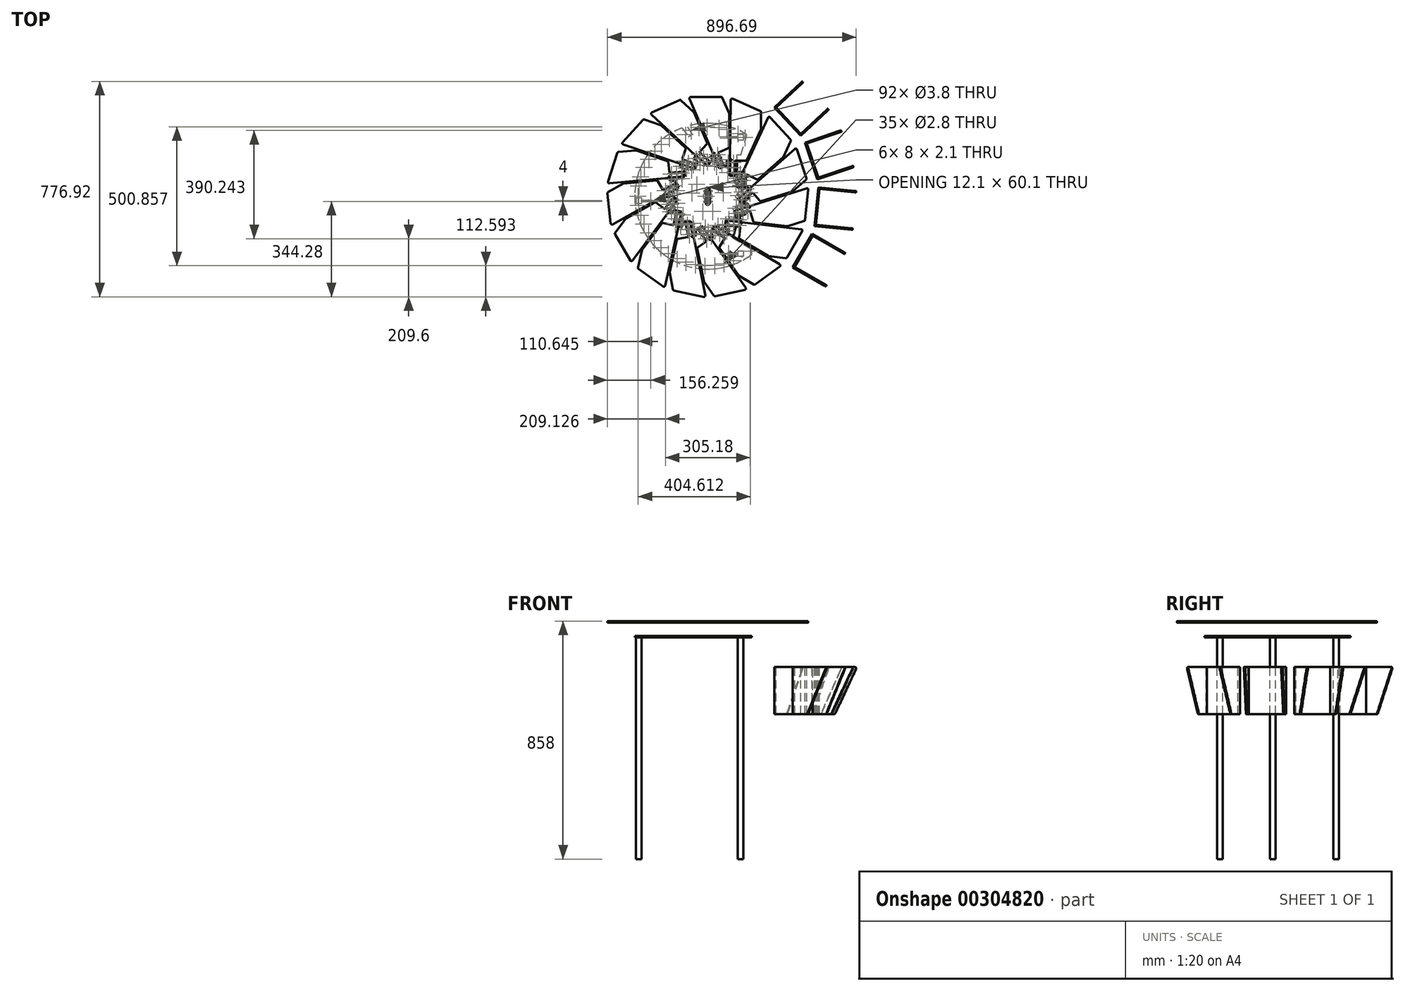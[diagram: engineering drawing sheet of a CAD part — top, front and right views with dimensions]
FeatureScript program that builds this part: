
annotation { "Feature Type Name" : "Feature", "Feature Type Description" : "" }
export const myFeature = defineFeature(function(context is Context, id is Id, definition is map)
    precondition{}
    {
        {
            var Q0;
            Q0=qCreatedBy(makeId("Top.planeOp"),FACE);
            var sketch = newSketch(context, id + "F0", { "sketchPlane" : qUnion([Q0])});
            skLineSegment(sketch, "E0", {"start": v(-97.83, 116.22) * mm, "end": v(-45.75, 98.54) * mm});
            skLineSegment(sketch, "E1", {"start": v(-80.98, 175.1) * mm, "end": v(-168.37, 255.87) * mm});
            skLineSegment(sketch, "E2", {"start": v(-101.62, 117.5) * mm, "end": v(-304.66, 186.43) * mm});
            skLineSegment(sketch, "E3", {"start": v(-306.77, 194.5) * mm, "end": v(-234.03, 275.42) * mm});
            skLineSegment(sketch, "E4", {"start": v(-43.7, 117.06) * mm, "end": v(-89.14, 132.49) * mm});
            skLineSegment(sketch, "E5", {"start": v(-91.02, 136.3) * mm, "end": v(-79.64, 169.81) * mm});
            skLineSegment(sketch, "E6.bottom", {"start": v(4.05, -30.05) * mm, "end": v(-4.05, -30.05) * mm});
            skLineSegment(sketch, "E6.top", {"start": v(4.05, 30.05) * mm, "end": v(-4.05, 30.05) * mm});
            skLineSegment(sketch, "E6.left", {"start": v(6.05, -28.05) * mm, "end": v(6.05, 28.05) * mm});
            skLineSegment(sketch, "E6.right", {"start": v(-6.05, -28.05) * mm, "end": v(-6.05, 28.05) * mm});
            skPoint(sketch, "E6.middle", {"position": v(0, 0) * mm});
            skPoint(sketch, "E7.visualSharp", {"position": v(-6.05, 30.05) * mm});
            skArc(sketch, "E7.filletArc", {"start": v(-4.05, 30.05) * mm, "mid": v(-5.46, 29.46) * mm, "end": v(-6.05, 28.05) * mm});
            skPoint(sketch, "E8.visualSharp", {"position": v(6.05, 30.05) * mm});
            skArc(sketch, "E8.filletArc", {"start": v(6.05, 28.05) * mm, "mid": v(5.46, 29.46) * mm, "end": v(4.05, 30.05) * mm});
            skPoint(sketch, "E9.visualSharp", {"position": v(-6.05, -30.05) * mm});
            skArc(sketch, "E9.filletArc", {"start": v(-6.05, -28.05) * mm, "mid": v(-5.46, -29.46) * mm, "end": v(-4.05, -30.05) * mm});
            skPoint(sketch, "E10.visualSharp", {"position": v(6.05, -30.05) * mm});
            skArc(sketch, "E10.filletArc", {"start": v(4.05, -30.05) * mm, "mid": v(5.46, -29.46) * mm, "end": v(6.05, -28.05) * mm});
            skLineSegment(sketch, "E11.bottom", {"start": v(-101.63, 105.04) * mm, "end": v(-91.98, 133.45) * mm});
            skLineSegment(sketch, "E11.top", {"start": v(-53.33, 88.65) * mm, "end": v(-43.7, 117.06) * mm});
            skLineSegment(sketch, "E11.left", {"start": v(-101.63, 105.04) * mm, "end": v(-53.33, 88.65) * mm});
            skLineSegment(sketch, "E11.right", {"start": v(-91.98, 133.45) * mm, "end": v(-43.7, 117.06) * mm});
            skCircle(sketch, "E12", {"center": v(-51.93, 114.57) * mm, "radius": 1.9 * mm});
            skCircle(sketch, "E13", {"center": v(-86.96, 126.47) * mm, "radius": 1.9 * mm});
            skCircle(sketch, "E14", {"center": v(-93.4, 107.53) * mm, "radius": 1.9 * mm});
            skCircle(sketch, "E15", {"center": v(-58.36, 95.64) * mm, "radius": 1.9 * mm});
            skPoint(sketch, "E16", {"position": v(-77.48, 96.85) * mm});
            skLineSegment(sketch, "E17.left", {"start": v(-97.51, 117.17) * mm, "end": v(-49.22, 100.77) * mm});
            skLineSegment(sketch, "E17.right", {"start": v(-96.1, 121.33) * mm, "end": v(-47.8, 104.94) * mm});
            skLineSegment(sketch, "E18.0", {"start": v(-58.36, 95.64) * mm, "end": v(-51.93, 114.57) * mm, "construction": true});
            skLineSegment(sketch, "E19.0", {"start": v(-93.4, 107.53) * mm, "end": v(-86.96, 126.47) * mm, "construction": true});
            skLineSegment(sketch, "E20.0", {"start": v(-58.36, 95.64) * mm, "end": v(-93.4, 107.53) * mm, "construction": true});
            skLineSegment(sketch, "E21.0", {"start": v(-51.93, 114.57) * mm, "end": v(-86.96, 126.47) * mm, "construction": true});
            skPoint(sketch, "E22", {"position": v(-96.8, 119.25) * mm});
            skCircle(sketch, "E23", {"center": v(-75.87, 101.58) * mm, "radius": 1.9 * mm});
            skCircle(sketch, "E24", {"center": v(-69.45, 120.52) * mm, "radius": 1.9 * mm});
            skCircle(sketch, "E25.1.0", {"center": v(-130.88, 80.16) * mm, "radius": 1.9 * mm});
            skLineSegment(sketch, "E25.1.1", {"start": v(-92.2, 63.63) * mm, "end": v(-94.04, 83.55) * mm, "construction": true});
            skCircle(sketch, "E25.1.2", {"center": v(-112.46, 81.86) * mm, "radius": 1.9 * mm});
            skLineSegment(sketch, "E25.1.3", {"start": v(-92.2, 63.63) * mm, "end": v(-129.05, 60.25) * mm, "construction": true});
            skCircle(sketch, "E25.1.4", {"center": v(-110.63, 61.94) * mm, "radius": 1.9 * mm});
            skCircle(sketch, "E25.1.5", {"center": v(-92.2, 63.63) * mm, "radius": 1.9 * mm});
            skLineSegment(sketch, "E25.1.6", {"start": v(-135.57, 54.63) * mm, "end": v(-84.78, 59.3) * mm});
            skLineSegment(sketch, "E25.1.7", {"start": v(-135.57, 54.63) * mm, "end": v(-138.31, 84.5) * mm});
            skPoint(sketch, "E25.1.8", {"position": v(-136.94, 69.56) * mm});
            skLineSegment(sketch, "E25.1.9", {"start": v(-94.04, 83.55) * mm, "end": v(-130.88, 80.16) * mm, "construction": true});
            skLineSegment(sketch, "E25.1.10", {"start": v(-84.78, 59.3) * mm, "end": v(-87.53, 89.17) * mm});
            skCircle(sketch, "E25.1.11", {"center": v(-129.05, 60.25) * mm, "radius": 1.9 * mm});
            skLineSegment(sketch, "E25.1.12", {"start": v(-129.05, 60.25) * mm, "end": v(-130.88, 80.16) * mm, "construction": true});
            skPoint(sketch, "E25.1.13", {"position": v(-110.17, 56.96) * mm});
            skCircle(sketch, "E25.1.14", {"center": v(-94.04, 83.55) * mm, "radius": 1.9 * mm});
            skLineSegment(sketch, "E25.1.16", {"start": v(-136.74, 67.37) * mm, "end": v(-85.95, 72.04) * mm});
            skLineSegment(sketch, "E25.1.17", {"start": v(-137.14, 71.75) * mm, "end": v(-86.35, 76.42) * mm});
            skCircle(sketch, "E25.2.0", {"center": v(-152.17, 20) * mm, "radius": 1.9 * mm});
            skLineSegment(sketch, "E25.2.1", {"start": v(-110.12, 20.63) * mm, "end": v(-119.9, 38.08) * mm, "construction": true});
            skCircle(sketch, "E25.2.2", {"center": v(-136.03, 29.04) * mm, "radius": 1.9 * mm});
            skLineSegment(sketch, "E25.2.3", {"start": v(-110.12, 20.63) * mm, "end": v(-142.4, 2.55) * mm, "construction": true});
            skCircle(sketch, "E25.2.4", {"center": v(-126.26, 11.59) * mm, "radius": 1.9 * mm});
            skCircle(sketch, "E25.2.5", {"center": v(-110.12, 20.63) * mm, "radius": 1.9 * mm});
            skLineSegment(sketch, "E25.2.6", {"start": v(-146.07, -5.24) * mm, "end": v(-101.57, 19.68) * mm});
            skLineSegment(sketch, "E25.2.7", {"start": v(-146.07, -5.24) * mm, "end": v(-160.72, 20.94) * mm});
            skPoint(sketch, "E25.2.8", {"position": v(-153.4, 7.85) * mm});
            skLineSegment(sketch, "E25.2.9", {"start": v(-119.9, 38.08) * mm, "end": v(-152.17, 20) * mm, "construction": true});
            skLineSegment(sketch, "E25.2.10", {"start": v(-101.57, 19.68) * mm, "end": v(-116.23, 45.86) * mm});
            skCircle(sketch, "E25.2.11", {"center": v(-142.4, 2.55) * mm, "radius": 1.9 * mm});
            skLineSegment(sketch, "E25.2.12", {"start": v(-142.4, 2.55) * mm, "end": v(-152.17, 20) * mm, "construction": true});
            skPoint(sketch, "E25.2.13", {"position": v(-123.82, 7.22) * mm});
            skCircle(sketch, "E25.2.14", {"center": v(-119.9, 38.08) * mm, "radius": 1.9 * mm});
            skLineSegment(sketch, "E25.2.16", {"start": v(-152.32, 5.93) * mm, "end": v(-107.82, 30.85) * mm});
            skLineSegment(sketch, "E25.2.17", {"start": v(-154.47, 9.77) * mm, "end": v(-109.97, 34.7) * mm});
            skCircle(sketch, "E25.3.0", {"center": v(-147.15, -43.63) * mm, "radius": 1.9 * mm});
            skLineSegment(sketch, "E25.3.1", {"start": v(-108.99, -25.95) * mm, "end": v(-125.01, -13.98) * mm, "construction": true});
            skCircle(sketch, "E25.3.2", {"center": v(-136.08, -28.8) * mm, "radius": 1.9 * mm});
            skLineSegment(sketch, "E25.3.3", {"start": v(-108.99, -25.95) * mm, "end": v(-131.13, -55.6) * mm, "construction": true});
            skCircle(sketch, "E25.3.4", {"center": v(-120.06, -40.77) * mm, "radius": 1.9 * mm});
            skCircle(sketch, "E25.3.5", {"center": v(-108.99, -25.95) * mm, "radius": 1.9 * mm});
            skLineSegment(sketch, "E25.3.6", {"start": v(-131.3, -64.2) * mm, "end": v(-100.8, -23.33) * mm});
            skLineSegment(sketch, "E25.3.7", {"start": v(-131.3, -64.2) * mm, "end": v(-155.35, -46.24) * mm});
            skPoint(sketch, "E25.3.8", {"position": v(-143.33, -55.22) * mm});
            skLineSegment(sketch, "E25.3.9", {"start": v(-125.01, -13.98) * mm, "end": v(-147.15, -43.63) * mm, "construction": true});
            skLineSegment(sketch, "E25.3.10", {"start": v(-100.8, -23.33) * mm, "end": v(-124.83, -5.38) * mm});
            skCircle(sketch, "E25.3.11", {"center": v(-131.13, -55.6) * mm, "radius": 1.9 * mm});
            skLineSegment(sketch, "E25.3.12", {"start": v(-131.13, -55.6) * mm, "end": v(-147.15, -43.63) * mm, "construction": true});
            skPoint(sketch, "E25.3.13", {"position": v(-116.05, -43.76) * mm});
            skCircle(sketch, "E25.3.14", {"center": v(-125.01, -13.98) * mm, "radius": 1.9 * mm});
            skLineSegment(sketch, "E25.3.16", {"start": v(-141.56, -56.53) * mm, "end": v(-111.05, -15.67) * mm});
            skLineSegment(sketch, "E25.3.17", {"start": v(-145.09, -53.9) * mm, "end": v(-114.57, -13.04) * mm});
            skCircle(sketch, "E25.4.0", {"center": v(-116.68, -99.7) * mm, "radius": 1.9 * mm});
            skLineSegment(sketch, "E25.4.1", {"start": v(-89.01, -68.03) * mm, "end": v(-108.52, -63.62) * mm, "construction": true});
            skCircle(sketch, "E25.4.2", {"center": v(-112.6, -81.66) * mm, "radius": 1.9 * mm});
            skLineSegment(sketch, "E25.4.3", {"start": v(-89.01, -68.03) * mm, "end": v(-97.18, -104.12) * mm, "construction": true});
            skCircle(sketch, "E25.4.4", {"center": v(-93.1, -86.08) * mm, "radius": 1.9 * mm});
            skCircle(sketch, "E25.4.5", {"center": v(-89.01, -68.03) * mm, "radius": 1.9 * mm});
            skLineSegment(sketch, "E25.4.6", {"start": v(-93.85, -112.05) * mm, "end": v(-82.6, -62.3) * mm});
            skLineSegment(sketch, "E25.4.7", {"start": v(-93.85, -112.05) * mm, "end": v(-123.1, -105.43) * mm});
            skPoint(sketch, "E25.4.8", {"position": v(-108.48, -108.74) * mm});
            skLineSegment(sketch, "E25.4.9", {"start": v(-108.52, -63.62) * mm, "end": v(-116.68, -99.7) * mm, "construction": true});
            skLineSegment(sketch, "E25.4.10", {"start": v(-82.6, -62.3) * mm, "end": v(-111.85, -55.69) * mm});
            skCircle(sketch, "E25.4.11", {"center": v(-97.18, -104.12) * mm, "radius": 1.9 * mm});
            skLineSegment(sketch, "E25.4.12", {"start": v(-97.18, -104.12) * mm, "end": v(-116.68, -99.7) * mm, "construction": true});
            skPoint(sketch, "E25.4.13", {"position": v(-88.22, -87.18) * mm});
            skCircle(sketch, "E25.4.14", {"center": v(-108.52, -63.62) * mm, "radius": 1.9 * mm});
            skLineSegment(sketch, "E25.4.16", {"start": v(-106.33, -109.23) * mm, "end": v(-95.07, -59.48) * mm});
            skLineSegment(sketch, "E25.4.17", {"start": v(-110.62, -108.26) * mm, "end": v(-99.37, -58.51) * mm});
            skCircle(sketch, "E25.5.0", {"center": v(-66.04, -138.55) * mm, "radius": 1.9 * mm});
            skLineSegment(sketch, "E25.5.1", {"start": v(-53.65, -98.36) * mm, "end": v(-73.26, -102.26) * mm, "construction": true});
            skCircle(sketch, "E25.5.2", {"center": v(-69.65, -120.4) * mm, "radius": 1.9 * mm});
            skLineSegment(sketch, "E25.5.3", {"start": v(-53.65, -98.36) * mm, "end": v(-46.43, -134.64) * mm, "construction": true});
            skCircle(sketch, "E25.5.4", {"center": v(-50.04, -116.5) * mm, "radius": 1.9 * mm});
            skCircle(sketch, "E25.5.5", {"center": v(-53.65, -98.36) * mm, "radius": 1.9 * mm});
            skLineSegment(sketch, "E25.5.6", {"start": v(-40.16, -140.53) * mm, "end": v(-50.1, -90.51) * mm});
            skLineSegment(sketch, "E25.5.7", {"start": v(-40.16, -140.53) * mm, "end": v(-69.58, -146.39) * mm});
            skPoint(sketch, "E25.5.8", {"position": v(-54.87, -143.46) * mm});
            skLineSegment(sketch, "E25.5.9", {"start": v(-73.26, -102.26) * mm, "end": v(-66.04, -138.55) * mm, "construction": true});
            skLineSegment(sketch, "E25.5.10", {"start": v(-50.1, -90.51) * mm, "end": v(-79.53, -96.37) * mm});
            skCircle(sketch, "E25.5.11", {"center": v(-46.43, -134.64) * mm, "radius": 1.9 * mm});
            skLineSegment(sketch, "E25.5.12", {"start": v(-46.43, -134.64) * mm, "end": v(-66.04, -138.55) * mm, "construction": true});
            skPoint(sketch, "E25.5.13", {"position": v(-45.13, -115.52) * mm});
            skCircle(sketch, "E25.5.14", {"center": v(-73.26, -102.26) * mm, "radius": 1.9 * mm});
            skLineSegment(sketch, "E25.5.16", {"start": v(-52.71, -143.03) * mm, "end": v(-62.66, -93.01) * mm});
            skLineSegment(sketch, "E25.5.17", {"start": v(-57.03, -143.9) * mm, "end": v(-66.98, -93.87) * mm});
            skCircle(sketch, "E25.6.0", {"center": v(-3.98, -153.43) * mm, "radius": 1.9 * mm});
            skLineSegment(sketch, "E25.6.1", {"start": v(-9, -111.67) * mm, "end": v(-25.34, -123.21) * mm, "construction": true});
            skCircle(sketch, "E25.6.2", {"center": v(-14.66, -138.32) * mm, "radius": 1.9 * mm});
            skLineSegment(sketch, "E25.6.3", {"start": v(-9, -111.67) * mm, "end": v(12.35, -141.89) * mm, "construction": true});
            skCircle(sketch, "E25.6.4", {"center": v(1.67, -126.78) * mm, "radius": 1.9 * mm});
            skCircle(sketch, "E25.6.5", {"center": v(-9, -111.67) * mm, "radius": 1.9 * mm});
            skLineSegment(sketch, "E25.6.6", {"start": v(20.48, -144.72) * mm, "end": v(-8.96, -103.07) * mm});
            skLineSegment(sketch, "E25.6.7", {"start": v(20.48, -144.72) * mm, "end": v(-4.02, -162.03) * mm});
            skPoint(sketch, "E25.6.8", {"position": v(8.23, -153.38) * mm});
            skLineSegment(sketch, "E25.6.9", {"start": v(-25.34, -123.21) * mm, "end": v(-3.98, -153.43) * mm, "construction": true});
            skLineSegment(sketch, "E25.6.10", {"start": v(-8.96, -103.07) * mm, "end": v(-33.46, -120.38) * mm});
            skCircle(sketch, "E25.6.11", {"center": v(12.35, -141.89) * mm, "radius": 1.9 * mm});
            skLineSegment(sketch, "E25.6.12", {"start": v(12.35, -141.89) * mm, "end": v(-3.98, -153.43) * mm, "construction": true});
            skPoint(sketch, "E25.6.13", {"position": v(5.76, -123.9) * mm});
            skCircle(sketch, "E25.6.14", {"center": v(-25.34, -123.21) * mm, "radius": 1.9 * mm});
            skLineSegment(sketch, "E25.6.15", {"start": v(-4.02, -162.03) * mm, "end": v(-33.46, -120.38) * mm});
            skLineSegment(sketch, "E25.6.16", {"start": v(10.02, -152.1) * mm, "end": v(-19.41, -110.46) * mm});
            skLineSegment(sketch, "E25.6.17", {"start": v(6.43, -154.65) * mm, "end": v(-23, -113) * mm});
            skCircle(sketch, "E25.7.0", {"center": v(58.77, -141.78) * mm, "radius": 1.9 * mm});
            skLineSegment(sketch, "E25.7.1", {"start": v(37.2, -105.68) * mm, "end": v(26.97, -122.87) * mm, "construction": true});
            skCircle(sketch, "E25.7.2", {"center": v(42.87, -132.33) * mm, "radius": 1.9 * mm});
            skLineSegment(sketch, "E25.7.3", {"start": v(37.2, -105.68) * mm, "end": v(69, -124.6) * mm, "construction": true});
            skCircle(sketch, "E25.7.4", {"center": v(53.1, -115.14) * mm, "radius": 1.9 * mm});
            skCircle(sketch, "E25.7.5", {"center": v(37.2, -105.68) * mm, "radius": 1.9 * mm});
            skLineSegment(sketch, "E25.7.6", {"start": v(77.57, -123.88) * mm, "end": v(33.74, -97.8) * mm});
            skLineSegment(sketch, "E25.7.7", {"start": v(77.57, -123.88) * mm, "end": v(62.23, -149.66) * mm});
            skPoint(sketch, "E25.7.8", {"position": v(69.9, -136.77) * mm});
            skLineSegment(sketch, "E25.7.9", {"start": v(26.97, -122.87) * mm, "end": v(58.77, -141.78) * mm, "construction": true});
            skLineSegment(sketch, "E25.7.10", {"start": v(33.74, -97.8) * mm, "end": v(18.4, -123.58) * mm});
            skCircle(sketch, "E25.7.11", {"center": v(69, -124.6) * mm, "radius": 1.9 * mm});
            skLineSegment(sketch, "E25.7.12", {"start": v(69, -124.6) * mm, "end": v(58.77, -141.78) * mm, "construction": true});
            skPoint(sketch, "E25.7.13", {"position": v(55.65, -110.84) * mm});
            skCircle(sketch, "E25.7.14", {"center": v(26.97, -122.87) * mm, "radius": 1.9 * mm});
            skLineSegment(sketch, "E25.7.16", {"start": v(71.02, -134.88) * mm, "end": v(27.2, -108.8) * mm});
            skLineSegment(sketch, "E25.7.17", {"start": v(68.77, -138.66) * mm, "end": v(24.94, -112.58) * mm});
            skCircle(sketch, "E25.8.0", {"center": v(111.36, -105.62) * mm, "radius": 1.9 * mm});
            skLineSegment(sketch, "E25.8.1", {"start": v(76.96, -81.41) * mm, "end": v(74.61, -101.27) * mm, "construction": true});
            skCircle(sketch, "E25.8.2", {"center": v(92.99, -103.45) * mm, "radius": 1.9 * mm});
            skLineSegment(sketch, "E25.8.3", {"start": v(76.96, -81.41) * mm, "end": v(113.7, -85.76) * mm, "construction": true});
            skCircle(sketch, "E25.8.4", {"center": v(95.34, -83.59) * mm, "radius": 1.9 * mm});
            skCircle(sketch, "E25.8.5", {"center": v(76.96, -81.41) * mm, "radius": 1.9 * mm});
            skLineSegment(sketch, "E25.8.6", {"start": v(121.25, -81.62) * mm, "end": v(70.6, -75.62) * mm});
            skLineSegment(sketch, "E25.8.7", {"start": v(121.25, -81.62) * mm, "end": v(117.72, -111.41) * mm});
            skPoint(sketch, "E25.8.8", {"position": v(119.48, -96.52) * mm});
            skLineSegment(sketch, "E25.8.9", {"start": v(74.61, -101.27) * mm, "end": v(111.36, -105.62) * mm, "construction": true});
            skLineSegment(sketch, "E25.8.10", {"start": v(70.6, -75.62) * mm, "end": v(67.07, -105.42) * mm});
            skCircle(sketch, "E25.8.11", {"center": v(113.7, -85.76) * mm, "radius": 1.9 * mm});
            skLineSegment(sketch, "E25.8.12", {"start": v(113.7, -85.76) * mm, "end": v(111.36, -105.62) * mm, "construction": true});
            skPoint(sketch, "E25.8.13", {"position": v(95.92, -78.62) * mm});
            skCircle(sketch, "E25.8.14", {"center": v(74.61, -101.27) * mm, "radius": 1.9 * mm});
            skLineSegment(sketch, "E25.8.16", {"start": v(119.74, -94.33) * mm, "end": v(69.1, -88.34) * mm});
            skLineSegment(sketch, "E25.8.17", {"start": v(119.23, -98.7) * mm, "end": v(68.58, -92.7) * mm});
            skCircle(sketch, "E25.9.0", {"center": v(144.7, -51.2) * mm, "radius": 1.9 * mm});
            skLineSegment(sketch, "E25.9.1", {"start": v(103.42, -43.07) * mm, "end": v(109.35, -62.17) * mm, "construction": true});
            skCircle(sketch, "E25.9.2", {"center": v(127.02, -56.68) * mm, "radius": 1.9 * mm});
            skLineSegment(sketch, "E25.9.3", {"start": v(103.42, -43.07) * mm, "end": v(138.76, -32.1) * mm, "construction": true});
            skCircle(sketch, "E25.9.4", {"center": v(121.1, -37.58) * mm, "radius": 1.9 * mm});
            skCircle(sketch, "E25.9.5", {"center": v(103.42, -43.07) * mm, "radius": 1.9 * mm});
            skLineSegment(sketch, "E25.9.6", {"start": v(143.96, -25.25) * mm, "end": v(95.26, -40.37) * mm});
            skLineSegment(sketch, "E25.9.7", {"start": v(143.96, -25.25) * mm, "end": v(152.86, -53.9) * mm});
            skPoint(sketch, "E25.9.8", {"position": v(148.41, -39.57) * mm});
            skLineSegment(sketch, "E25.9.9", {"start": v(109.35, -62.17) * mm, "end": v(144.7, -51.2) * mm, "construction": true});
            skLineSegment(sketch, "E25.9.10", {"start": v(95.26, -40.37) * mm, "end": v(104.15, -69.02) * mm});
            skCircle(sketch, "E25.9.11", {"center": v(138.76, -32.1) * mm, "radius": 1.9 * mm});
            skLineSegment(sketch, "E25.9.12", {"start": v(138.76, -32.1) * mm, "end": v(144.7, -51.2) * mm, "construction": true});
            skPoint(sketch, "E25.9.13", {"position": v(119.6, -32.8) * mm});
            skCircle(sketch, "E25.9.14", {"center": v(109.35, -62.17) * mm, "radius": 1.9 * mm});
            skLineSegment(sketch, "E25.9.15", {"start": v(152.86, -53.9) * mm, "end": v(104.15, -69.02) * mm});
            skLineSegment(sketch, "E25.9.16", {"start": v(147.76, -37.47) * mm, "end": v(99.05, -52.6) * mm});
            skLineSegment(sketch, "E25.9.17", {"start": v(149.06, -41.67) * mm, "end": v(100.36, -56.8) * mm});
            skCircle(sketch, "E25.10.0", {"center": v(153, 12.08) * mm, "radius": 1.9 * mm});
            skLineSegment(sketch, "E25.10.1", {"start": v(112, 2.72) * mm, "end": v(125.19, -12.32) * mm, "construction": true});
            skCircle(sketch, "E25.10.2", {"center": v(139.1, -0.12) * mm, "radius": 1.9 * mm});
            skLineSegment(sketch, "E25.10.3", {"start": v(112, 2.72) * mm, "end": v(139.82, 27.12) * mm, "construction": true});
            skCircle(sketch, "E25.10.4", {"center": v(125.9, 14.92) * mm, "radius": 1.9 * mm});
            skCircle(sketch, "E25.10.5", {"center": v(112, 2.72) * mm, "radius": 1.9 * mm});
            skLineSegment(sketch, "E25.10.6", {"start": v(141.79, 35.5) * mm, "end": v(103.44, 1.86) * mm});
            skLineSegment(sketch, "E25.10.7", {"start": v(141.79, 35.5) * mm, "end": v(161.57, 12.93) * mm});
            skLineSegment(sketch, "E25.10.9", {"start": v(125.19, -12.32) * mm, "end": v(153, 12.08) * mm, "construction": true});
            skLineSegment(sketch, "E25.10.10", {"start": v(103.44, 1.86) * mm, "end": v(123.22, -20.7) * mm});
            skCircle(sketch, "E25.10.11", {"center": v(139.82, 27.12) * mm, "radius": 1.9 * mm});
            skLineSegment(sketch, "E25.10.12", {"start": v(139.82, 27.12) * mm, "end": v(153, 12.08) * mm, "construction": true});
            skPoint(sketch, "E25.10.13", {"position": v(122.61, 18.68) * mm});
            skCircle(sketch, "E25.10.14", {"center": v(125.19, -12.32) * mm, "radius": 1.9 * mm});
            skLineSegment(sketch, "E25.10.16", {"start": v(150.22, 25.87) * mm, "end": v(111.88, -7.76) * mm});
            skLineSegment(sketch, "E25.10.17", {"start": v(153.13, 22.56) * mm, "end": v(114.78, -11.07) * mm});
            skCircle(sketch, "E25.11.0", {"center": v(134.86, 73.27) * mm, "radius": 1.9 * mm});
            skLineSegment(sketch, "E25.11.1", {"start": v(101.21, 48.04) * mm, "end": v(119.37, 39.67) * mm, "construction": true});
            skCircle(sketch, "E25.11.2", {"center": v(127.12, 56.47) * mm, "radius": 1.9 * mm});
            skLineSegment(sketch, "E25.11.3", {"start": v(101.21, 48.04) * mm, "end": v(116.7, 81.64) * mm, "construction": true});
            skCircle(sketch, "E25.11.4", {"center": v(108.96, 64.84) * mm, "radius": 1.9 * mm});
            skCircle(sketch, "E25.11.5", {"center": v(101.21, 48.04) * mm, "radius": 1.9 * mm});
            skLineSegment(sketch, "E25.11.6", {"start": v(115.1, 90.1) * mm, "end": v(93.74, 43.78) * mm});
            skLineSegment(sketch, "E25.11.7", {"start": v(115.1, 90.1) * mm, "end": v(142.34, 77.53) * mm});
            skPoint(sketch, "E25.11.8", {"position": v(128.71, 83.81) * mm});
            skLineSegment(sketch, "E25.11.9", {"start": v(119.37, 39.67) * mm, "end": v(134.86, 73.27) * mm, "construction": true});
            skLineSegment(sketch, "E25.11.10", {"start": v(93.74, 43.78) * mm, "end": v(120.98, 31.22) * mm});
            skCircle(sketch, "E25.11.11", {"center": v(116.7, 81.64) * mm, "radius": 1.9 * mm});
            skLineSegment(sketch, "E25.11.12", {"start": v(116.7, 81.64) * mm, "end": v(134.86, 73.27) * mm, "construction": true});
            skPoint(sketch, "E25.11.13", {"position": v(104.42, 66.93) * mm});
            skCircle(sketch, "E25.11.14", {"center": v(119.37, 39.67) * mm, "radius": 1.9 * mm});
            skLineSegment(sketch, "E25.11.16", {"start": v(126.72, 84.73) * mm, "end": v(105.36, 38.42) * mm});
            skLineSegment(sketch, "E25.11.17", {"start": v(130.71, 82.9) * mm, "end": v(109.36, 36.57) * mm});
            skCircle(sketch, "E25.12.0", {"center": v(93.4, 121.79) * mm, "radius": 1.9 * mm});
            skLineSegment(sketch, "E25.12.1", {"start": v(72.92, 85.05) * mm, "end": v(92.92, 84.8) * mm, "construction": true});
            skCircle(sketch, "E25.12.2", {"center": v(93.16, 103.29) * mm, "radius": 1.9 * mm});
            skLineSegment(sketch, "E25.12.3", {"start": v(72.92, 85.05) * mm, "end": v(73.4, 122.05) * mm, "construction": true});
            skCircle(sketch, "E25.12.4", {"center": v(73.16, 103.55) * mm, "radius": 1.9 * mm});
            skCircle(sketch, "E25.12.5", {"center": v(72.92, 85.05) * mm, "radius": 1.9 * mm});
            skLineSegment(sketch, "E25.12.6", {"start": v(68.5, 129.11) * mm, "end": v(67.83, 78.12) * mm});
            skLineSegment(sketch, "E25.12.7", {"start": v(68.5, 129.11) * mm, "end": v(98.5, 128.72) * mm});
            skPoint(sketch, "E25.12.8", {"position": v(83.5, 128.92) * mm});
            skLineSegment(sketch, "E25.12.9", {"start": v(92.92, 84.8) * mm, "end": v(93.4, 121.79) * mm, "construction": true});
            skLineSegment(sketch, "E25.12.10", {"start": v(67.83, 78.12) * mm, "end": v(97.83, 77.73) * mm});
            skCircle(sketch, "E25.12.11", {"center": v(73.4, 122.05) * mm, "radius": 1.9 * mm});
            skLineSegment(sketch, "E25.12.12", {"start": v(73.4, 122.05) * mm, "end": v(93.4, 121.79) * mm, "construction": true});
            skPoint(sketch, "E25.12.13", {"position": v(68.16, 103.62) * mm});
            skCircle(sketch, "E25.12.14", {"center": v(92.92, 84.8) * mm, "radius": 1.9 * mm});
            skLineSegment(sketch, "E25.12.15", {"start": v(98.5, 128.72) * mm, "end": v(97.83, 77.73) * mm});
            skLineSegment(sketch, "E25.12.16", {"start": v(81.3, 128.95) * mm, "end": v(80.63, 77.95) * mm});
            skLineSegment(sketch, "E25.12.17", {"start": v(85.7, 128.89) * mm, "end": v(85.03, 77.9) * mm});
            skCircle(sketch, "E25.13.0", {"center": v(35.8, 149.25) * mm, "radius": 1.9 * mm});
            skLineSegment(sketch, "E25.13.1", {"start": v(32.02, 107.36) * mm, "end": v(50.4, 115.25) * mm, "construction": true});
            skCircle(sketch, "E25.13.2", {"center": v(43.1, 132.25) * mm, "radius": 1.9 * mm});
            skLineSegment(sketch, "E25.13.3", {"start": v(32.02, 107.36) * mm, "end": v(17.42, 141.35) * mm, "construction": true});
            skCircle(sketch, "E25.13.4", {"center": v(24.72, 124.36) * mm, "radius": 1.9 * mm});
            skCircle(sketch, "E25.13.5", {"center": v(32.02, 107.36) * mm, "radius": 1.9 * mm});
            skLineSegment(sketch, "E25.13.6", {"start": v(10.06, 145.81) * mm, "end": v(30.2, 98.95) * mm});
            skLineSegment(sketch, "E25.13.7", {"start": v(10.06, 145.81) * mm, "end": v(37.62, 157.66) * mm});
            skPoint(sketch, "E25.13.8", {"position": v(23.84, 151.73) * mm});
            skLineSegment(sketch, "E25.13.9", {"start": v(50.4, 115.25) * mm, "end": v(35.8, 149.25) * mm, "construction": true});
            skLineSegment(sketch, "E25.13.10", {"start": v(30.2, 98.95) * mm, "end": v(57.76, 110.8) * mm});
            skCircle(sketch, "E25.13.11", {"center": v(17.42, 141.35) * mm, "radius": 1.9 * mm});
            skLineSegment(sketch, "E25.13.12", {"start": v(17.42, 141.35) * mm, "end": v(35.8, 149.25) * mm, "construction": true});
            skPoint(sketch, "E25.13.13", {"position": v(20.13, 122.38) * mm});
            skCircle(sketch, "E25.13.14", {"center": v(50.4, 115.25) * mm, "radius": 1.9 * mm});
            skLineSegment(sketch, "E25.13.15", {"start": v(37.62, 157.66) * mm, "end": v(57.76, 110.8) * mm});
            skLineSegment(sketch, "E25.13.16", {"start": v(21.82, 150.87) * mm, "end": v(41.95, 104) * mm});
            skLineSegment(sketch, "E25.13.17", {"start": v(25.86, 152.6) * mm, "end": v(46, 105.74) * mm});
            skCircle(sketch, "E25.14.0", {"center": v(-28, 150.9) * mm, "radius": 1.9 * mm});
            skLineSegment(sketch, "E25.14.1", {"start": v(-14.41, 111.1) * mm, "end": v(-0.84, 125.79) * mm, "construction": true});
            skCircle(sketch, "E25.14.2", {"center": v(-14.42, 138.35) * mm, "radius": 1.9 * mm});
            skLineSegment(sketch, "E25.14.3", {"start": v(-14.41, 111.1) * mm, "end": v(-41.58, 136.22) * mm, "construction": true});
            skCircle(sketch, "E25.14.4", {"center": v(-28, 123.66) * mm, "radius": 1.9 * mm});
            skCircle(sketch, "E25.14.5", {"center": v(-14.41, 111.1) * mm, "radius": 1.9 * mm});
            skLineSegment(sketch, "E25.14.6", {"start": v(-50.12, 137.3) * mm, "end": v(-12.67, 102.68) * mm});
            skLineSegment(sketch, "E25.14.7", {"start": v(-50.12, 137.3) * mm, "end": v(-29.75, 159.33) * mm});
            skPoint(sketch, "E25.14.8", {"position": v(-39.93, 148.31) * mm});
            skLineSegment(sketch, "E25.14.9", {"start": v(-0.84, 125.79) * mm, "end": v(-28, 150.9) * mm, "construction": true});
            skLineSegment(sketch, "E25.14.10", {"start": v(-12.67, 102.68) * mm, "end": v(7.7, 124.7) * mm});
            skCircle(sketch, "E25.14.11", {"center": v(-41.58, 136.22) * mm, "radius": 1.9 * mm});
            skLineSegment(sketch, "E25.14.12", {"start": v(-41.58, 136.22) * mm, "end": v(-28, 150.9) * mm, "construction": true});
            skPoint(sketch, "E25.14.13", {"position": v(-31.4, 119.99) * mm});
            skCircle(sketch, "E25.14.14", {"center": v(-0.84, 125.79) * mm, "radius": 1.9 * mm});
            skLineSegment(sketch, "E25.14.16", {"start": v(-41.43, 146.7) * mm, "end": v(-3.98, 112.08) * mm});
            skLineSegment(sketch, "E25.14.17", {"start": v(-38.44, 149.93) * mm, "end": v(-1, 115.31) * mm});
            skLineSegment(sketch, "E26", {"start": v(-101.62, 117.5) * mm, "end": v(-100.53, 120.72) * mm});
            skLineSegment(sketch, "E27", {"start": v(-96.72, 122.6) * mm, "end": v(-47.48, 105.89) * mm});
            skLineSegment(sketch, "E28", {"start": v(-47.48, 105.89) * mm, "end": v(-43.7, 117.06) * mm});
            skLineSegment(sketch, "E29", {"start": v(-43.7, 117.06) * mm, "end": v(-47.48, 105.89) * mm});
            skLineSegment(sketch, "E30", {"start": v(-97.83, 116.22) * mm, "end": v(-101.63, 105.04) * mm});
            skLineSegment(sketch, "E31", {"start": v(-45.75, 98.54) * mm, "end": v(-36.78, 124.97) * mm});
            skLineSegment(sketch, "E32", {"start": v(-36.78, 124.97) * mm, "end": v(-50.12, 137.3) * mm});
            skLineSegment(sketch, "E33.1.0", {"start": v(-81.88, 71.41) * mm, "end": v(-84.43, 99.2) * mm});
            skLineSegment(sketch, "E33.1.1", {"start": v(-136.65, 66.38) * mm, "end": v(-81.88, 71.41) * mm});
            skLineSegment(sketch, "E33.1.2", {"start": v(-136.65, 66.38) * mm, "end": v(-135.57, 54.63) * mm});
            skLineSegment(sketch, "E33.1.3", {"start": v(-84.43, 99.2) * mm, "end": v(-101.63, 105.04) * mm});
            skLineSegment(sketch, "E33.1.12", {"start": v(-87.53, 89.17) * mm, "end": v(-138.31, 84.5) * mm});
            skLineSegment(sketch, "E33.1.13", {"start": v(-87.53, 89.17) * mm, "end": v(-86.45, 77.42) * mm});
            skLineSegment(sketch, "E33.2.0", {"start": v(-103.84, 31.93) * mm, "end": v(-117.48, 56.29) * mm});
            skLineSegment(sketch, "E33.2.1", {"start": v(-151.83, 5.06) * mm, "end": v(-103.84, 31.93) * mm});
            skLineSegment(sketch, "E33.2.2", {"start": v(-151.83, 5.06) * mm, "end": v(-146.07, -5.24) * mm});
            skLineSegment(sketch, "E33.2.3", {"start": v(-117.48, 56.29) * mm, "end": v(-135.57, 54.63) * mm});
            skLineSegment(sketch, "E33.2.12", {"start": v(-116.23, 45.86) * mm, "end": v(-160.72, 20.94) * mm});
            skLineSegment(sketch, "E33.2.13", {"start": v(-116.23, 45.86) * mm, "end": v(-110.46, 35.56) * mm});
            skLineSegment(sketch, "E33.3.0", {"start": v(-107.85, -13.06) * mm, "end": v(-130.22, 3.64) * mm});
            skLineSegment(sketch, "E33.3.1", {"start": v(-140.76, -57.13) * mm, "end": v(-107.85, -13.06) * mm});
            skLineSegment(sketch, "E33.3.2", {"start": v(-140.76, -57.13) * mm, "end": v(-131.3, -64.2) * mm});
            skLineSegment(sketch, "E33.3.3", {"start": v(-130.22, 3.64) * mm, "end": v(-146.07, -5.24) * mm});
            skLineSegment(sketch, "E33.3.12", {"start": v(-124.83, -5.38) * mm, "end": v(-155.35, -46.24) * mm});
            skLineSegment(sketch, "E33.3.13", {"start": v(-124.83, -5.38) * mm, "end": v(-115.38, -12.44) * mm});
            skLineSegment(sketch, "E33.4.0", {"start": v(-93.22, -55.8) * mm, "end": v(-120.44, -49.64) * mm});
            skLineSegment(sketch, "E33.4.1", {"start": v(-105.36, -109.45) * mm, "end": v(-93.22, -55.8) * mm});
            skLineSegment(sketch, "E33.4.2", {"start": v(-105.36, -109.45) * mm, "end": v(-93.85, -112.05) * mm});
            skLineSegment(sketch, "E33.4.3", {"start": v(-120.44, -49.64) * mm, "end": v(-131.3, -64.2) * mm});
            skLineSegment(sketch, "E33.4.12", {"start": v(-111.85, -55.69) * mm, "end": v(-123.1, -105.43) * mm});
            skLineSegment(sketch, "E33.4.13", {"start": v(-111.85, -55.69) * mm, "end": v(-100.34, -58.3) * mm});
            skLineSegment(sketch, "E33.5.0", {"start": v(-62.46, -88.9) * mm, "end": v(-89.84, -94.34) * mm});
            skLineSegment(sketch, "E33.5.1", {"start": v(-51.73, -142.84) * mm, "end": v(-62.46, -88.9) * mm});
            skLineSegment(sketch, "E33.5.2", {"start": v(-51.73, -142.84) * mm, "end": v(-40.16, -140.53) * mm});
            skLineSegment(sketch, "E33.5.3", {"start": v(-89.84, -94.34) * mm, "end": v(-93.85, -112.05) * mm});
            skLineSegment(sketch, "E33.5.12", {"start": v(-79.53, -96.37) * mm, "end": v(-69.58, -146.39) * mm});
            skLineSegment(sketch, "E33.5.13", {"start": v(-79.53, -96.37) * mm, "end": v(-67.96, -94.07) * mm});
            skLineSegment(sketch, "E33.6.0", {"start": v(-20.9, -106.61) * mm, "end": v(-43.7, -122.72) * mm});
            skLineSegment(sketch, "E33.6.1", {"start": v(10.84, -151.53) * mm, "end": v(-20.9, -106.61) * mm});
            skLineSegment(sketch, "E33.6.2", {"start": v(10.84, -151.53) * mm, "end": v(20.48, -144.72) * mm});
            skLineSegment(sketch, "E33.6.3", {"start": v(-43.7, -122.72) * mm, "end": v(-40.16, -140.53) * mm});
            skLineSegment(sketch, "E33.6.13", {"start": v(-33.46, -120.38) * mm, "end": v(-23.82, -113.57) * mm});
            skLineSegment(sketch, "E33.7.0", {"start": v(24.27, -105.9) * mm, "end": v(10, -129.89) * mm});
            skLineSegment(sketch, "E33.7.1", {"start": v(71.53, -134.02) * mm, "end": v(24.27, -105.9) * mm});
            skLineSegment(sketch, "E33.7.2", {"start": v(71.53, -134.02) * mm, "end": v(77.57, -123.88) * mm});
            skLineSegment(sketch, "E33.7.3", {"start": v(10, -129.89) * mm, "end": v(20.48, -144.72) * mm});
            skLineSegment(sketch, "E33.7.12", {"start": v(18.4, -123.58) * mm, "end": v(62.23, -149.66) * mm});
            skLineSegment(sketch, "E33.7.13", {"start": v(18.4, -123.58) * mm, "end": v(24.43, -113.44) * mm});
            skLineSegment(sketch, "E33.8.0", {"start": v(65.24, -86.87) * mm, "end": v(61.96, -114.6) * mm});
            skLineSegment(sketch, "E33.8.1", {"start": v(119.86, -93.34) * mm, "end": v(65.24, -86.87) * mm});
            skLineSegment(sketch, "E33.8.2", {"start": v(119.86, -93.34) * mm, "end": v(121.25, -81.62) * mm});
            skLineSegment(sketch, "E33.8.3", {"start": v(61.96, -114.6) * mm, "end": v(77.57, -123.88) * mm});
            skLineSegment(sketch, "E33.8.12", {"start": v(67.07, -105.42) * mm, "end": v(117.72, -111.41) * mm});
            skLineSegment(sketch, "E33.8.13", {"start": v(67.07, -105.42) * mm, "end": v(68.46, -93.7) * mm});
            skLineSegment(sketch, "E33.9.0", {"start": v(94.94, -52.83) * mm, "end": v(103.21, -79.48) * mm});
            skLineSegment(sketch, "E33.9.1", {"start": v(147.46, -36.52) * mm, "end": v(94.94, -52.83) * mm});
            skLineSegment(sketch, "E33.9.2", {"start": v(147.46, -36.52) * mm, "end": v(143.96, -25.25) * mm});
            skLineSegment(sketch, "E33.9.3", {"start": v(103.21, -79.48) * mm, "end": v(121.25, -81.62) * mm});
            skLineSegment(sketch, "E33.9.13", {"start": v(104.15, -69.02) * mm, "end": v(100.65, -57.75) * mm});
            skLineSegment(sketch, "E33.10.0", {"start": v(108.21, -9.65) * mm, "end": v(126.62, -30.63) * mm});
            skLineSegment(sketch, "E33.10.1", {"start": v(149.57, 26.62) * mm, "end": v(108.21, -9.65) * mm});
            skLineSegment(sketch, "E33.10.2", {"start": v(149.57, 26.62) * mm, "end": v(141.79, 35.5) * mm});
            skLineSegment(sketch, "E33.10.3", {"start": v(126.62, -30.63) * mm, "end": v(143.96, -25.25) * mm});
            skLineSegment(sketch, "E33.10.12", {"start": v(123.22, -20.7) * mm, "end": v(161.57, 12.93) * mm});
            skLineSegment(sketch, "E33.10.13", {"start": v(123.22, -20.7) * mm, "end": v(115.44, -11.82) * mm});
            skLineSegment(sketch, "E33.11.0", {"start": v(102.78, 35.2) * mm, "end": v(128.13, 23.52) * mm});
            skLineSegment(sketch, "E33.11.1", {"start": v(125.8, 85.15) * mm, "end": v(102.78, 35.2) * mm});
            skLineSegment(sketch, "E33.11.2", {"start": v(125.8, 85.15) * mm, "end": v(115.1, 90.1) * mm});
            skLineSegment(sketch, "E33.11.3", {"start": v(128.13, 23.52) * mm, "end": v(141.79, 35.5) * mm});
            skLineSegment(sketch, "E33.11.12", {"start": v(120.98, 31.22) * mm, "end": v(142.34, 77.53) * mm});
            skLineSegment(sketch, "E33.11.13", {"start": v(120.98, 31.22) * mm, "end": v(110.27, 36.16) * mm});
            skLineSegment(sketch, "E33.12.0", {"start": v(79.58, 73.96) * mm, "end": v(107.49, 73.6) * mm});
            skLineSegment(sketch, "E33.12.1", {"start": v(80.3, 128.96) * mm, "end": v(79.58, 73.96) * mm});
            skLineSegment(sketch, "E33.12.2", {"start": v(80.3, 128.96) * mm, "end": v(68.5, 129.11) * mm});
            skLineSegment(sketch, "E33.12.3", {"start": v(107.49, 73.6) * mm, "end": v(115.1, 90.1) * mm});
            skLineSegment(sketch, "E33.12.13", {"start": v(97.83, 77.73) * mm, "end": v(86.03, 77.88) * mm});
            skLineSegment(sketch, "E33.13.0", {"start": v(42.61, 99.94) * mm, "end": v(68.26, 110.96) * mm});
            skLineSegment(sketch, "E33.13.1", {"start": v(20.9, 150.47) * mm, "end": v(42.61, 99.94) * mm});
            skLineSegment(sketch, "E33.13.2", {"start": v(20.9, 150.47) * mm, "end": v(10.06, 145.81) * mm});
            skLineSegment(sketch, "E33.13.3", {"start": v(68.26, 110.96) * mm, "end": v(68.5, 129.11) * mm});
            skLineSegment(sketch, "E33.13.13", {"start": v(57.76, 110.8) * mm, "end": v(46.91, 106.14) * mm});
            skLineSegment(sketch, "E33.14.0", {"start": v(-1.72, 108.63) * mm, "end": v(17.23, 129.13) * mm});
            skLineSegment(sketch, "E33.14.1", {"start": v(-42.1, 145.96) * mm, "end": v(-1.72, 108.63) * mm});
            skLineSegment(sketch, "E33.14.2", {"start": v(-42.1, 145.96) * mm, "end": v(-50.12, 137.3) * mm});
            skLineSegment(sketch, "E33.14.3", {"start": v(17.23, 129.13) * mm, "end": v(10.06, 145.81) * mm});
            skLineSegment(sketch, "E33.14.12", {"start": v(7.7, 124.7) * mm, "end": v(-29.75, 159.33) * mm});
            skLineSegment(sketch, "E33.14.13", {"start": v(7.7, 124.7) * mm, "end": v(-0.31, 116.04) * mm});
            skPoint(sketch, "E34", {"position": v(-165.85, 186.8) * mm});
            skLineSegment(sketch, "E35", {"start": v(-228.7, 276.8) * mm, "end": v(-170.15, 256.93) * mm});
            skPoint(sketch, "E36.visualSharp", {"position": v(-311.84, 188.86) * mm});
            skArc(sketch, "E36.filletArc", {"start": v(-306.77, 194.5) * mm, "mid": v(-307.9, 189.9) * mm, "end": v(-304.66, 186.43) * mm});
            skPoint(sketch, "E37.visualSharp", {"position": v(-231.83, 277.87) * mm});
            skArc(sketch, "E37.filletArc", {"start": v(-228.7, 276.8) * mm, "mid": v(-231.58, 276.91) * mm, "end": v(-234.03, 275.42) * mm});
            skPoint(sketch, "E38.visualSharp", {"position": v(-169.15, 256.6) * mm});
            skArc(sketch, "E38.filletArc", {"start": v(-168.37, 255.87) * mm, "mid": v(-169.2, 256.5) * mm, "end": v(-170.15, 256.93) * mm});
            skPoint(sketch, "E39.visualSharp", {"position": v(-78.6, 172.89) * mm});
            skArc(sketch, "E39.filletArc", {"start": v(-79.64, 169.81) * mm, "mid": v(-79.53, 172.65) * mm, "end": v(-80.98, 175.1) * mm});
            skPoint(sketch, "E40.visualSharp", {"position": v(-99.57, 123.56) * mm});
            skArc(sketch, "E40.filletArc", {"start": v(-96.72, 122.6) * mm, "mid": v(-99.02, 122.45) * mm, "end": v(-100.53, 120.72) * mm});
            skPoint(sketch, "E41.visualSharp", {"position": v(-91.98, 133.45) * mm});
            skArc(sketch, "E41.filletArc", {"start": v(-91.02, 136.3) * mm, "mid": v(-90.87, 134) * mm, "end": v(-89.14, 132.49) * mm});
            skLineSegment(sketch, "E42.1.0", {"start": v(-359.36, 52.91) * mm, "end": v(-325.82, 156.42) * mm});
            skLineSegment(sketch, "E42.1.1", {"start": v(-140.63, 66.01) * mm, "end": v(-354.15, 46.4) * mm});
            skLineSegment(sketch, "E42.1.2", {"start": v(-321.52, 159.85) * mm, "end": v(-259.95, 165.51) * mm});
            skPoint(sketch, "E42.1.3", {"position": v(-258.89, 165.6) * mm});
            skPoint(sketch, "E42.1.4", {"position": v(-324.8, 159.55) * mm});
            skLineSegment(sketch, "E42.1.5", {"start": v(-145.2, 127.02) * mm, "end": v(-257.88, 165.27) * mm});
            skPoint(sketch, "E42.1.6", {"position": v(-361.7, 45.7) * mm});
            skPoint(sketch, "E42.1.7", {"position": v(-227.5, 103.2) * mm});
            skArc(sketch, "E42.1.8", {"start": v(-359.36, 52.91) * mm, "mid": v(-358.5, 48.25) * mm, "end": v(-354.15, 46.4) * mm});
            skArc(sketch, "E42.1.9", {"start": v(-321.52, 159.85) * mm, "mid": v(-324.19, 158.78) * mm, "end": v(-325.82, 156.42) * mm});
            skArc(sketch, "E42.1.10", {"start": v(-257.88, 165.27) * mm, "mid": v(-258.9, 165.5) * mm, "end": v(-259.95, 165.51) * mm});
            skLineSegment(sketch, "E42.1.11", {"start": v(-138.59, 87.49) * mm, "end": v(-141.83, 122.74) * mm});
            skPoint(sketch, "E42.1.12", {"position": v(-142.12, 125.97) * mm});
            skArc(sketch, "E42.1.13", {"start": v(-141.83, 122.74) * mm, "mid": v(-142.88, 125.38) * mm, "end": v(-145.2, 127.02) * mm});
            skArc(sketch, "E42.1.14", {"start": v(-138.59, 87.49) * mm, "mid": v(-137.52, 85.46) * mm, "end": v(-135.32, 84.78) * mm});
            skLineSegment(sketch, "E42.1.15", {"start": v(-87.53, 89.17) * mm, "end": v(-135.32, 84.78) * mm});
            skLineSegment(sketch, "E42.1.16", {"start": v(-140.63, 66.01) * mm, "end": v(-140.94, 69.4) * mm});
            skArc(sketch, "E42.1.17", {"start": v(-138.23, 72.66) * mm, "mid": v(-140.26, 71.6) * mm, "end": v(-140.94, 69.4) * mm});
            skLineSegment(sketch, "E42.1.18", {"start": v(-138.23, 72.66) * mm, "end": v(-86.45, 77.42) * mm});
            skLineSegment(sketch, "E42.2.0", {"start": v(-349.81, -97.83) * mm, "end": v(-361.27, 10.37) * mm});
            skLineSegment(sketch, "E42.2.1", {"start": v(-155.32, 3.1) * mm, "end": v(-342.4, -101.66) * mm});
            skLineSegment(sketch, "E42.2.2", {"start": v(-358.74, 15.26) * mm, "end": v(-304.8, 45.47) * mm});
            skPoint(sketch, "E42.2.3", {"position": v(-303.87, 46) * mm});
            skPoint(sketch, "E42.2.4", {"position": v(-361.62, 13.65) * mm});
            skLineSegment(sketch, "E42.2.5", {"start": v(-184.3, 56.98) * mm, "end": v(-302.8, 46.09) * mm});
            skPoint(sketch, "E42.2.6", {"position": v(-349.02, -105.37) * mm});
            skPoint(sketch, "E42.2.7", {"position": v(-249.8, 1.75) * mm});
            skArc(sketch, "E42.2.8", {"start": v(-349.81, -97.83) * mm, "mid": v(-347.14, -101.74) * mm, "end": v(-342.4, -101.66) * mm});
            skArc(sketch, "E42.2.9", {"start": v(-358.74, 15.26) * mm, "mid": v(-360.74, 13.2) * mm, "end": v(-361.27, 10.37) * mm});
            skArc(sketch, "E42.2.10", {"start": v(-302.8, 46.09) * mm, "mid": v(-303.83, 45.88) * mm, "end": v(-304.8, 45.47) * mm});
            skLineSegment(sketch, "E42.2.11", {"start": v(-162.2, 23.56) * mm, "end": v(-179.49, 54.44) * mm});
            skPoint(sketch, "E42.2.12", {"position": v(-181.07, 57.27) * mm});
            skArc(sketch, "E42.2.13", {"start": v(-179.49, 54.44) * mm, "mid": v(-181.52, 56.42) * mm, "end": v(-184.3, 56.98) * mm});
            skArc(sketch, "E42.2.14", {"start": v(-162.2, 23.56) * mm, "mid": v(-160.39, 22.14) * mm, "end": v(-158.1, 22.4) * mm});
            skLineSegment(sketch, "E42.2.15", {"start": v(-116.23, 45.86) * mm, "end": v(-158.1, 22.4) * mm});
            skLineSegment(sketch, "E42.2.16", {"start": v(-155.32, 3.1) * mm, "end": v(-156.98, 6.07) * mm});
            skArc(sketch, "E42.2.17", {"start": v(-155.83, 10.15) * mm, "mid": v(-157.25, 8.35) * mm, "end": v(-156.98, 6.07) * mm});
            skLineSegment(sketch, "E42.2.18", {"start": v(-155.83, 10.15) * mm, "end": v(-110.46, 35.56) * mm});
            skLineSegment(sketch, "E42.3.0", {"start": v(-279.78, -231.65) * mm, "end": v(-334.26, -137.47) * mm});
            skLineSegment(sketch, "E42.3.1", {"start": v(-143.16, -60.34) * mm, "end": v(-271.45, -232.14) * mm});
            skLineSegment(sketch, "E42.3.2", {"start": v(-333.93, -131.97) * mm, "end": v(-296.94, -82.43) * mm});
            skPoint(sketch, "E42.3.3", {"position": v(-296.3, -81.58) * mm});
            skPoint(sketch, "E42.3.4", {"position": v(-335.9, -134.62) * mm});
            skLineSegment(sketch, "E42.3.5", {"start": v(-191.55, -22.91) * mm, "end": v(-295.37, -81.06) * mm});
            skPoint(sketch, "E42.3.6", {"position": v(-275.98, -238.22) * mm});
            skPoint(sketch, "E42.3.7", {"position": v(-228.91, -100) * mm});
            skArc(sketch, "E42.3.8", {"start": v(-279.78, -231.65) * mm, "mid": v(-275.75, -234.14) * mm, "end": v(-271.45, -232.14) * mm});
            skArc(sketch, "E42.3.9", {"start": v(-333.93, -131.97) * mm, "mid": v(-334.92, -134.67) * mm, "end": v(-334.26, -137.47) * mm});
            skArc(sketch, "E42.3.10", {"start": v(-295.37, -81.06) * mm, "mid": v(-296.23, -81.66) * mm, "end": v(-296.94, -82.43) * mm});
            skLineSegment(sketch, "E42.3.11", {"start": v(-157.75, -44.45) * mm, "end": v(-186.11, -23.27) * mm});
            skPoint(sketch, "E42.3.12", {"position": v(-188.71, -21.33) * mm});
            skArc(sketch, "E42.3.13", {"start": v(-186.11, -23.27) * mm, "mid": v(-188.78, -22.29) * mm, "end": v(-191.55, -22.91) * mm});
            skArc(sketch, "E42.3.14", {"start": v(-157.75, -44.45) * mm, "mid": v(-155.52, -45.01) * mm, "end": v(-153.55, -43.84) * mm});
            skLineSegment(sketch, "E42.3.15", {"start": v(-124.83, -5.38) * mm, "end": v(-153.55, -43.84) * mm});
            skLineSegment(sketch, "E42.3.16", {"start": v(-143.16, -60.34) * mm, "end": v(-145.88, -58.3) * mm});
            skArc(sketch, "E42.3.17", {"start": v(-146.49, -54.1) * mm, "mid": v(-147.05, -56.33) * mm, "end": v(-145.88, -58.3) * mm});
            skLineSegment(sketch, "E42.3.18", {"start": v(-146.49, -54.1) * mm, "end": v(-115.38, -12.44) * mm});
            skLineSegment(sketch, "E42.4.0", {"start": v(-161.37, -325.42) * mm, "end": v(-249.44, -261.54) * mm});
            skLineSegment(sketch, "E42.4.1", {"start": v(-106.24, -113.35) * mm, "end": v(-153.56, -322.48) * mm});
            skLineSegment(sketch, "E42.4.2", {"start": v(-251.39, -256.39) * mm, "end": v(-237.74, -196.08) * mm});
            skPoint(sketch, "E42.4.3", {"position": v(-237.5, -195.04) * mm});
            skPoint(sketch, "E42.4.4", {"position": v(-252.11, -259.6) * mm});
            skLineSegment(sketch, "E42.4.5", {"start": v(-165.67, -98.84) * mm, "end": v(-236.87, -194.2) * mm});
            skPoint(sketch, "E42.4.6", {"position": v(-155.23, -329.87) * mm});
            skPoint(sketch, "E42.4.7", {"position": v(-168.44, -184.47) * mm});
            skArc(sketch, "E42.4.8", {"start": v(-161.37, -325.42) * mm, "mid": v(-156.67, -326.05) * mm, "end": v(-153.56, -322.48) * mm});
            skArc(sketch, "E42.4.9", {"start": v(-251.39, -256.39) * mm, "mid": v(-251.19, -259.25) * mm, "end": v(-249.44, -261.54) * mm});
            skArc(sketch, "E42.4.10", {"start": v(-236.87, -194.2) * mm, "mid": v(-237.4, -195.09) * mm, "end": v(-237.74, -196.08) * mm});
            skLineSegment(sketch, "E42.4.11", {"start": v(-126.03, -104.77) * mm, "end": v(-160.56, -96.96) * mm});
            skPoint(sketch, "E42.4.12", {"position": v(-163.72, -96.24) * mm});
            skArc(sketch, "E42.4.13", {"start": v(-160.56, -96.96) * mm, "mid": v(-163.4, -97.14) * mm, "end": v(-165.67, -98.84) * mm});
            skArc(sketch, "E42.4.14", {"start": v(-126.03, -104.77) * mm, "mid": v(-123.77, -104.38) * mm, "end": v(-122.44, -102.5) * mm});
            skLineSegment(sketch, "E42.4.15", {"start": v(-111.85, -55.69) * mm, "end": v(-122.44, -102.5) * mm});
            skLineSegment(sketch, "E42.4.16", {"start": v(-106.24, -113.35) * mm, "end": v(-109.55, -112.6) * mm});
            skArc(sketch, "E42.4.17", {"start": v(-111.82, -109.01) * mm, "mid": v(-111.43, -111.27) * mm, "end": v(-109.55, -112.6) * mm});
            skLineSegment(sketch, "E42.4.18", {"start": v(-111.82, -109.01) * mm, "end": v(-100.34, -58.3) * mm});
            skLineSegment(sketch, "E42.5.0", {"start": v(-15.06, -362.92) * mm, "end": v(-121.5, -340.39) * mm});
            skLineSegment(sketch, "E42.5.1", {"start": v(-50.95, -146.76) * mm, "end": v(-9.12, -357.06) * mm});
            skLineSegment(sketch, "E42.5.2", {"start": v(-125.37, -336.47) * mm, "end": v(-137.43, -275.82) * mm});
            skPoint(sketch, "E42.5.3", {"position": v(-137.64, -274.78) * mm});
            skPoint(sketch, "E42.5.4", {"position": v(-124.73, -339.7) * mm});
            skLineSegment(sketch, "E42.5.5", {"start": v(-111.14, -157.68) * mm, "end": v(-137.4, -273.75) * mm});
            skPoint(sketch, "E42.5.6", {"position": v(-7.64, -364.5) * mm});
            skPoint(sketch, "E42.5.7", {"position": v(-78.85, -237.03) * mm});
            skArc(sketch, "E42.5.8", {"start": v(-15.06, -362.92) * mm, "mid": v(-10.5, -361.59) * mm, "end": v(-9.12, -357.06) * mm});
            skArc(sketch, "E42.5.9", {"start": v(-125.37, -336.47) * mm, "mid": v(-124.02, -339) * mm, "end": v(-121.5, -340.39) * mm});
            skArc(sketch, "E42.5.10", {"start": v(-137.4, -273.75) * mm, "mid": v(-137.53, -274.78) * mm, "end": v(-137.43, -275.82) * mm});
            skLineSegment(sketch, "E42.5.11", {"start": v(-72.52, -146.97) * mm, "end": v(-107.24, -153.88) * mm});
            skPoint(sketch, "E42.5.12", {"position": v(-110.43, -154.51) * mm});
            skArc(sketch, "E42.5.13", {"start": v(-107.24, -153.88) * mm, "mid": v(-109.75, -155.2) * mm, "end": v(-111.14, -157.68) * mm});
            skArc(sketch, "E42.5.14", {"start": v(-72.52, -146.97) * mm, "mid": v(-70.61, -145.7) * mm, "end": v(-70.17, -143.44) * mm});
            skLineSegment(sketch, "E42.5.15", {"start": v(-79.53, -96.37) * mm, "end": v(-70.17, -143.44) * mm});
            skLineSegment(sketch, "E42.5.16", {"start": v(-50.95, -146.76) * mm, "end": v(-54.28, -147.42) * mm});
            skArc(sketch, "E42.5.17", {"start": v(-57.81, -145.07) * mm, "mid": v(-56.54, -146.98) * mm, "end": v(-54.28, -147.42) * mm});
            skLineSegment(sketch, "E42.5.18", {"start": v(-57.81, -145.07) * mm, "end": v(-67.96, -94.07) * mm});
            skLineSegment(sketch, "E42.6.0", {"start": v(133.86, -337.67) * mm, "end": v(27.45, -360.38) * mm});
            skLineSegment(sketch, "E42.6.1", {"start": v(13.15, -154.8) * mm, "end": v(136.9, -329.9) * mm});
            skLineSegment(sketch, "E42.6.2", {"start": v(22.32, -358.37) * mm, "end": v(-13.36, -307.88) * mm});
            skPoint(sketch, "E42.6.3", {"position": v(-13.98, -307) * mm});
            skPoint(sketch, "E42.6.4", {"position": v(24.23, -361.06) * mm});
            skLineSegment(sketch, "E42.6.5", {"start": v(-37.4, -189.25) * mm, "end": v(-14.18, -305.97) * mm});
            skPoint(sketch, "E42.6.6", {"position": v(141.27, -336.09) * mm});
            skPoint(sketch, "E42.6.7", {"position": v(24.38, -248.61) * mm});
            skArc(sketch, "E42.6.8", {"start": v(133.86, -337.67) * mm, "mid": v(137.47, -334.6) * mm, "end": v(136.9, -329.9) * mm});
            skArc(sketch, "E42.6.9", {"start": v(22.32, -358.37) * mm, "mid": v(24.59, -360.14) * mm, "end": v(27.45, -360.38) * mm});
            skArc(sketch, "E42.6.10", {"start": v(-14.18, -305.97) * mm, "mid": v(-13.87, -306.96) * mm, "end": v(-13.36, -307.88) * mm});
            skLineSegment(sketch, "E42.6.11", {"start": v(-6.47, -163.76) * mm, "end": v(-35.38, -184.2) * mm});
            skPoint(sketch, "E42.6.12", {"position": v(-38.03, -186.07) * mm});
            skArc(sketch, "E42.6.13", {"start": v(-35.38, -184.2) * mm, "mid": v(-37.14, -186.42) * mm, "end": v(-37.4, -189.25) * mm});
            skArc(sketch, "E42.6.14", {"start": v(-6.47, -163.76) * mm, "mid": v(-5.25, -161.82) * mm, "end": v(-5.76, -159.58) * mm});
            skLineSegment(sketch, "E42.6.15", {"start": v(-33.46, -120.38) * mm, "end": v(-5.76, -159.58) * mm});
            skLineSegment(sketch, "E42.6.16", {"start": v(13.15, -154.8) * mm, "end": v(10.37, -156.76) * mm});
            skArc(sketch, "E42.6.17", {"start": v(6.19, -156.04) * mm, "mid": v(8.13, -157.26) * mm, "end": v(10.37, -156.76) * mm});
            skLineSegment(sketch, "E42.6.18", {"start": v(6.19, -156.04) * mm, "end": v(-23.82, -113.57) * mm});
            skLineSegment(sketch, "E42.7.0", {"start": v(259.63, -254.03) * mm, "end": v(171.66, -318.06) * mm});
            skLineSegment(sketch, "E42.7.1", {"start": v(74.97, -136.06) * mm, "end": v(259.24, -245.7) * mm});
            skLineSegment(sketch, "E42.7.2", {"start": v(166.16, -318.3) * mm, "end": v(113.02, -286.7) * mm});
            skPoint(sketch, "E42.7.3", {"position": v(112.1, -286.15) * mm});
            skPoint(sketch, "E42.7.4", {"position": v(168.99, -320) * mm});
            skLineSegment(sketch, "E42.7.5", {"start": v(42.8, -188.1) * mm, "end": v(111.5, -285.28) * mm});
            skPoint(sketch, "E42.7.6", {"position": v(265.76, -249.57) * mm});
            skPoint(sketch, "E42.7.7", {"position": v(123.39, -217.2) * mm});
            skArc(sketch, "E42.7.8", {"start": v(259.63, -254.03) * mm, "mid": v(261.68, -249.76) * mm, "end": v(259.24, -245.7) * mm});
            skArc(sketch, "E42.7.9", {"start": v(166.16, -318.3) * mm, "mid": v(168.94, -319) * mm, "end": v(171.66, -318.06) * mm});
            skArc(sketch, "E42.7.10", {"start": v(111.5, -285.28) * mm, "mid": v(112.18, -286.07) * mm, "end": v(113.02, -286.7) * mm});
            skLineSegment(sketch, "E42.7.11", {"start": v(60.7, -152.24) * mm, "end": v(42.6, -182.66) * mm});
            skPoint(sketch, "E42.7.12", {"position": v(40.94, -185.45) * mm});
            skArc(sketch, "E42.7.13", {"start": v(42.6, -182.66) * mm, "mid": v(41.9, -185.41) * mm, "end": v(42.8, -188.1) * mm});
            skArc(sketch, "E42.7.14", {"start": v(60.7, -152.24) * mm, "mid": v(61.02, -149.97) * mm, "end": v(59.65, -148.13) * mm});
            skLineSegment(sketch, "E42.7.15", {"start": v(18.4, -123.58) * mm, "end": v(59.65, -148.13) * mm});
            skLineSegment(sketch, "E42.7.16", {"start": v(74.97, -136.06) * mm, "end": v(73.23, -138.99) * mm});
            skArc(sketch, "E42.7.17", {"start": v(69.12, -140.03) * mm, "mid": v(71.4, -140.36) * mm, "end": v(73.23, -138.99) * mm});
            skLineSegment(sketch, "E42.7.18", {"start": v(69.12, -140.03) * mm, "end": v(24.43, -113.44) * mm});
            skLineSegment(sketch, "E42.8.0", {"start": v(340.5, -126.47) * mm, "end": v(286.18, -220.74) * mm});
            skLineSegment(sketch, "E42.8.1", {"start": v(123.83, -93.8) * mm, "end": v(336.76, -119) * mm});
            skLineSegment(sketch, "E42.8.2", {"start": v(281.26, -223.2) * mm, "end": v(219.86, -215.94) * mm});
            skPoint(sketch, "E42.8.3", {"position": v(218.8, -215.82) * mm});
            skPoint(sketch, "E42.8.4", {"position": v(284.53, -223.6) * mm});
            skLineSegment(sketch, "E42.8.5", {"start": v(115.62, -154.43) * mm, "end": v(217.89, -215.27) * mm});
            skPoint(sketch, "E42.8.6", {"position": v(344.3, -119.9) * mm});
            skPoint(sketch, "E42.8.7", {"position": v(201.06, -148.24) * mm});
            skArc(sketch, "E42.8.8", {"start": v(340.5, -126.47) * mm, "mid": v(340.64, -121.73) * mm, "end": v(336.76, -119) * mm});
            skArc(sketch, "E42.8.9", {"start": v(281.26, -223.2) * mm, "mid": v(284.09, -222.71) * mm, "end": v(286.18, -220.74) * mm});
            skArc(sketch, "E42.8.10", {"start": v(217.89, -215.27) * mm, "mid": v(218.84, -215.7) * mm, "end": v(219.86, -215.94) * mm});
            skLineSegment(sketch, "E42.8.11", {"start": v(117.37, -114.4) * mm, "end": v(113.2, -149.54) * mm});
            skPoint(sketch, "E42.8.12", {"position": v(112.83, -152.77) * mm});
            skArc(sketch, "E42.8.13", {"start": v(113.2, -149.54) * mm, "mid": v(113.69, -152.34) * mm, "end": v(115.62, -154.43) * mm});
            skArc(sketch, "E42.8.14", {"start": v(117.37, -114.4) * mm, "mid": v(116.75, -112.18) * mm, "end": v(114.74, -111.06) * mm});
            skLineSegment(sketch, "E42.8.15", {"start": v(67.07, -105.42) * mm, "end": v(114.74, -111.06) * mm});
            skLineSegment(sketch, "E42.8.16", {"start": v(123.83, -93.8) * mm, "end": v(123.43, -97.18) * mm});
            skArc(sketch, "E42.8.17", {"start": v(120.1, -99.81) * mm, "mid": v(122.31, -99.19) * mm, "end": v(123.43, -97.18) * mm});
            skLineSegment(sketch, "E42.8.18", {"start": v(120.1, -99.81) * mm, "end": v(68.46, -93.7) * mm});
            skLineSegment(sketch, "E42.9.0", {"start": v(362.5, 22.96) * mm, "end": v(351.22, -85.26) * mm});
            skLineSegment(sketch, "E42.9.1", {"start": v(151.28, -35.33) * mm, "end": v(356.05, 28.25) * mm});
            skLineSegment(sketch, "E42.9.2", {"start": v(347.73, -89.51) * mm, "end": v(288.68, -107.85) * mm});
            skPoint(sketch, "E42.9.3", {"position": v(287.66, -108.16) * mm});
            skPoint(sketch, "E42.9.4", {"position": v(350.88, -88.53) * mm});
            skLineSegment(sketch, "E42.9.5", {"start": v(168.43, -94.05) * mm, "end": v(286.6, -108.04) * mm});
            skPoint(sketch, "E42.9.6", {"position": v(363.3, 30.5) * mm});
            skPoint(sketch, "E42.9.7", {"position": v(243.98, -53.64) * mm});
            skArc(sketch, "E42.9.8", {"start": v(362.5, 22.96) * mm, "mid": v(360.7, 27.34) * mm, "end": v(356.05, 28.25) * mm});
            skArc(sketch, "E42.9.9", {"start": v(347.73, -89.51) * mm, "mid": v(350.11, -87.9) * mm, "end": v(351.22, -85.26) * mm});
            skArc(sketch, "E42.9.10", {"start": v(286.6, -108.04) * mm, "mid": v(287.65, -108.05) * mm, "end": v(288.68, -107.85) * mm});
            skLineSegment(sketch, "E42.9.11", {"start": v(153.75, -56.76) * mm, "end": v(164.25, -90.57) * mm});
            skPoint(sketch, "E42.9.12", {"position": v(165.2, -93.67) * mm});
            skArc(sketch, "E42.9.13", {"start": v(164.25, -90.57) * mm, "mid": v(165.82, -92.93) * mm, "end": v(168.43, -94.05) * mm});
            skArc(sketch, "E42.9.14", {"start": v(153.75, -56.76) * mm, "mid": v(152.28, -55) * mm, "end": v(150, -54.79) * mm});
            skLineSegment(sketch, "E42.9.15", {"start": v(104.15, -69.02) * mm, "end": v(150, -54.79) * mm});
            skLineSegment(sketch, "E42.9.16", {"start": v(151.28, -35.33) * mm, "end": v(152.29, -38.58) * mm});
            skArc(sketch, "E42.9.17", {"start": v(150.31, -42.33) * mm, "mid": v(152.08, -40.86) * mm, "end": v(152.29, -38.58) * mm});
            skLineSegment(sketch, "E42.9.18", {"start": v(150.31, -42.33) * mm, "end": v(100.65, -57.75) * mm});
            skLineSegment(sketch, "E42.10.0", {"start": v(321.83, 168.42) * mm, "end": v(355.53, 64.97) * mm});
            skLineSegment(sketch, "E42.10.1", {"start": v(152.57, 29.26) * mm, "end": v(313.78, 170.63) * mm});
            skLineSegment(sketch, "E42.10.2", {"start": v(354.08, 59.66) * mm, "end": v(307.59, 18.9) * mm});
            skPoint(sketch, "E42.10.3", {"position": v(306.79, 18.2) * mm});
            skPoint(sketch, "E42.10.4", {"position": v(356.55, 61.83) * mm});
            skLineSegment(sketch, "E42.10.5", {"start": v(192.13, -17.41) * mm, "end": v(305.77, 17.88) * mm});
            skPoint(sketch, "E42.10.6", {"position": v(319.48, 175.63) * mm});
            skPoint(sketch, "E42.10.7", {"position": v(244.7, 50.23) * mm});
            skArc(sketch, "E42.10.8", {"start": v(321.83, 168.42) * mm, "mid": v(318.4, 171.7) * mm, "end": v(313.78, 170.63) * mm});
            skArc(sketch, "E42.10.9", {"start": v(354.08, 59.66) * mm, "mid": v(355.6, 62.1) * mm, "end": v(355.53, 64.97) * mm});
            skArc(sketch, "E42.10.10", {"start": v(305.77, 17.88) * mm, "mid": v(306.73, 18.29) * mm, "end": v(307.59, 18.9) * mm});
            skLineSegment(sketch, "E42.10.11", {"start": v(163.54, 10.68) * mm, "end": v(186.88, -15.93) * mm});
            skPoint(sketch, "E42.10.12", {"position": v(189.02, -18.38) * mm});
            skArc(sketch, "E42.10.13", {"start": v(186.88, -15.93) * mm, "mid": v(189.29, -17.45) * mm, "end": v(192.13, -17.41) * mm});
            skArc(sketch, "E42.10.14", {"start": v(163.54, 10.68) * mm, "mid": v(161.48, 11.7) * mm, "end": v(159.31, 10.96) * mm});
            skLineSegment(sketch, "E42.10.15", {"start": v(123.22, -20.7) * mm, "end": v(159.31, 10.96) * mm});
            skLineSegment(sketch, "E42.10.16", {"start": v(152.57, 29.26) * mm, "end": v(154.81, 26.7) * mm});
            skArc(sketch, "E42.10.17", {"start": v(154.54, 22.47) * mm, "mid": v(155.55, 24.53) * mm, "end": v(154.81, 26.7) * mm});
            skLineSegment(sketch, "E42.10.18", {"start": v(154.54, 22.47) * mm, "end": v(115.44, -11.82) * mm});
            skLineSegment(sketch, "E42.11.0", {"start": v(225.5, 284.76) * mm, "end": v(298.37, 203.96) * mm});
            skLineSegment(sketch, "E42.11.1", {"start": v(127.48, 88.78) * mm, "end": v(217.25, 283.5) * mm});
            skLineSegment(sketch, "E42.11.2", {"start": v(299.2, 198.52) * mm, "end": v(273.31, 142.37) * mm});
            skPoint(sketch, "E42.11.3", {"position": v(272.87, 141.4) * mm});
            skPoint(sketch, "E42.11.4", {"position": v(300.58, 201.51) * mm});
            skLineSegment(sketch, "E42.11.5", {"start": v(182.6, 62.24) * mm, "end": v(272.07, 140.7) * mm});
            skPoint(sketch, "E42.11.6", {"position": v(220.43, 290.4) * mm});
            skPoint(sketch, "E42.11.7", {"position": v(203.12, 145.42) * mm});
            skArc(sketch, "E42.11.8", {"start": v(225.5, 284.76) * mm, "mid": v(221.04, 286.35) * mm, "end": v(217.25, 283.5) * mm});
            skArc(sketch, "E42.11.9", {"start": v(299.2, 198.52) * mm, "mid": v(299.6, 201.36) * mm, "end": v(298.37, 203.96) * mm});
            skArc(sketch, "E42.11.10", {"start": v(272.07, 140.7) * mm, "mid": v(272.78, 141.47) * mm, "end": v(273.31, 142.37) * mm});
            skLineSegment(sketch, "E42.11.11", {"start": v(145.06, 76.28) * mm, "end": v(177.2, 61.46) * mm});
            skPoint(sketch, "E42.11.12", {"position": v(180.16, 60.1) * mm});
            skArc(sketch, "E42.11.13", {"start": v(177.2, 61.46) * mm, "mid": v(180.02, 61.05) * mm, "end": v(182.6, 62.24) * mm});
            skArc(sketch, "E42.11.14", {"start": v(145.06, 76.28) * mm, "mid": v(142.77, 76.37) * mm, "end": v(141.08, 74.8) * mm});
            skLineSegment(sketch, "E42.11.15", {"start": v(120.98, 31.22) * mm, "end": v(141.08, 74.8) * mm});
            skLineSegment(sketch, "E42.11.16", {"start": v(127.48, 88.78) * mm, "end": v(130.57, 87.36) * mm});
            skArc(sketch, "E42.11.17", {"start": v(132.04, 83.38) * mm, "mid": v(132.13, 85.67) * mm, "end": v(130.57, 87.36) * mm});
            skLineSegment(sketch, "E42.11.18", {"start": v(132.04, 83.38) * mm, "end": v(110.27, 36.16) * mm});
            skLineSegment(sketch, "E42.12.0", {"start": v(90.19, 351.86) * mm, "end": v(189.62, 307.69) * mm});
            skLineSegment(sketch, "E42.12.1", {"start": v(80.35, 132.96) * mm, "end": v(83.16, 347.36) * mm});
            skLineSegment(sketch, "E42.12.2", {"start": v(192.59, 303.05) * mm, "end": v(191.78, 241.22) * mm});
            skPoint(sketch, "E42.12.3", {"position": v(191.76, 240.16) * mm});
            skPoint(sketch, "E42.12.4", {"position": v(192.63, 306.35) * mm});
            skLineSegment(sketch, "E42.12.5", {"start": v(141.5, 131.13) * mm, "end": v(191.32, 239.2) * mm});
            skPoint(sketch, "E42.12.6", {"position": v(83.26, 354.94) * mm});
            skPoint(sketch, "E42.12.7", {"position": v(126.41, 215.46) * mm});
            skArc(sketch, "E42.12.8", {"start": v(90.19, 351.86) * mm, "mid": v(85.46, 351.5) * mm, "end": v(83.16, 347.36) * mm});
            skArc(sketch, "E42.12.9", {"start": v(192.59, 303.05) * mm, "mid": v(191.8, 305.81) * mm, "end": v(189.62, 307.69) * mm});
            skArc(sketch, "E42.12.10", {"start": v(191.32, 239.2) * mm, "mid": v(191.65, 240.18) * mm, "end": v(191.78, 241.22) * mm});
            skLineSegment(sketch, "E42.12.11", {"start": v(101.5, 128.68) * mm, "end": v(136.9, 128.22) * mm});
            skPoint(sketch, "E42.12.12", {"position": v(140.14, 128.18) * mm});
            skArc(sketch, "E42.12.13", {"start": v(136.9, 128.22) * mm, "mid": v(139.62, 129) * mm, "end": v(141.5, 131.13) * mm});
            skArc(sketch, "E42.12.14", {"start": v(101.5, 128.68) * mm, "mid": v(99.36, 127.83) * mm, "end": v(98.46, 125.72) * mm});
            skLineSegment(sketch, "E42.12.15", {"start": v(97.83, 77.73) * mm, "end": v(98.46, 125.72) * mm});
            skLineSegment(sketch, "E42.12.16", {"start": v(80.35, 132.96) * mm, "end": v(83.75, 132.92) * mm});
            skArc(sketch, "E42.12.17", {"start": v(86.7, 129.88) * mm, "mid": v(85.86, 132) * mm, "end": v(83.75, 132.92) * mm});
            skLineSegment(sketch, "E42.12.18", {"start": v(86.7, 129.88) * mm, "end": v(86.03, 77.88) * mm});
            skLineSegment(sketch, "E42.13.0", {"start": v(-60.73, 358.12) * mm, "end": v(48.08, 358.2) * mm});
            skLineSegment(sketch, "E42.13.1", {"start": v(19.32, 154.15) * mm, "end": v(-65.32, 351.15) * mm});
            skLineSegment(sketch, "E42.13.2", {"start": v(52.67, 355.18) * mm, "end": v(77.08, 298.37) * mm});
            skPoint(sketch, "E42.13.3", {"position": v(77.5, 297.4) * mm});
            skPoint(sketch, "E42.13.4", {"position": v(51.37, 358.21) * mm});
            skLineSegment(sketch, "E42.13.5", {"start": v(75.93, 177.34) * mm, "end": v(77.49, 296.33) * mm});
            skPoint(sketch, "E42.13.6", {"position": v(-68.3, 358.12) * mm});
            skPoint(sketch, "E42.13.7", {"position": v(27.85, 248.25) * mm});
            skArc(sketch, "E42.13.8", {"start": v(-60.73, 358.12) * mm, "mid": v(-64.9, 355.87) * mm, "end": v(-65.32, 351.15) * mm});
            skArc(sketch, "E42.13.9", {"start": v(52.67, 355.18) * mm, "mid": v(50.83, 357.39) * mm, "end": v(48.08, 358.2) * mm});
            skArc(sketch, "E42.13.10", {"start": v(77.49, 296.33) * mm, "mid": v(77.4, 297.37) * mm, "end": v(77.08, 298.37) * mm});
            skLineSegment(sketch, "E42.13.11", {"start": v(40.38, 158.84) * mm, "end": v(72.9, 172.81) * mm});
            skPoint(sketch, "E42.13.12", {"position": v(75.89, 174.1) * mm});
            skArc(sketch, "E42.13.13", {"start": v(72.9, 172.81) * mm, "mid": v(75.09, 174.63) * mm, "end": v(75.93, 177.34) * mm});
            skArc(sketch, "E42.13.14", {"start": v(40.38, 158.84) * mm, "mid": v(38.78, 157.2) * mm, "end": v(38.8, 154.9) * mm});
            skLineSegment(sketch, "E42.13.15", {"start": v(57.76, 110.8) * mm, "end": v(38.8, 154.9) * mm});
            skLineSegment(sketch, "E42.13.16", {"start": v(19.32, 154.15) * mm, "end": v(22.45, 155.49) * mm});
            skArc(sketch, "E42.13.17", {"start": v(26.39, 153.92) * mm, "mid": v(24.74, 155.52) * mm, "end": v(22.45, 155.49) * mm});
            skLineSegment(sketch, "E42.13.18", {"start": v(26.39, 153.92) * mm, "end": v(46.91, 106.14) * mm});
            skLineSegment(sketch, "E42.14.0", {"start": v(-201.14, 302.46) * mm, "end": v(-101.78, 346.8) * mm});
            skLineSegment(sketch, "E42.14.1", {"start": v(-45.04, 148.68) * mm, "end": v(-202.5, 294.22) * mm});
            skLineSegment(sketch, "E42.14.2", {"start": v(-96.35, 345.9) * mm, "end": v(-50.94, 303.93) * mm});
            skPoint(sketch, "E42.14.3", {"position": v(-50.16, 303.2) * mm});
            skPoint(sketch, "E42.14.4", {"position": v(-98.77, 348.14) * mm});
            skLineSegment(sketch, "E42.14.5", {"start": v(-2.77, 192.9) * mm, "end": v(-49.74, 302.23) * mm});
            skPoint(sketch, "E42.14.6", {"position": v(-208.06, 299.37) * mm});
            skPoint(sketch, "E42.14.7", {"position": v(-75.53, 238.11) * mm});
            skArc(sketch, "E42.14.8", {"start": v(-201.14, 302.46) * mm, "mid": v(-204.03, 298.7) * mm, "end": v(-202.5, 294.22) * mm});
            skArc(sketch, "E42.14.9", {"start": v(-96.35, 345.9) * mm, "mid": v(-98.93, 347.16) * mm, "end": v(-101.78, 346.8) * mm});
            skArc(sketch, "E42.14.10", {"start": v(-49.74, 302.23) * mm, "mid": v(-50.25, 303.14) * mm, "end": v(-50.94, 303.93) * mm});
            skLineSegment(sketch, "E42.14.11", {"start": v(-27.72, 161.53) * mm, "end": v(-3.69, 187.53) * mm});
            skPoint(sketch, "E42.14.12", {"position": v(-1.48, 189.9) * mm});
            skArc(sketch, "E42.14.13", {"start": v(-3.69, 187.53) * mm, "mid": v(-2.43, 190.07) * mm, "end": v(-2.77, 192.9) * mm});
            skArc(sketch, "E42.14.14", {"start": v(-27.72, 161.53) * mm, "mid": v(-28.51, 159.38) * mm, "end": v(-27.55, 157.3) * mm});
            skLineSegment(sketch, "E42.14.15", {"start": v(7.7, 124.7) * mm, "end": v(-27.55, 157.3) * mm});
            skLineSegment(sketch, "E42.14.16", {"start": v(-45.04, 148.68) * mm, "end": v(-42.74, 151.18) * mm});
            skArc(sketch, "E42.14.17", {"start": v(-38.5, 151.34) * mm, "mid": v(-40.65, 152.14) * mm, "end": v(-42.74, 151.18) * mm});
            skLineSegment(sketch, "E42.14.18", {"start": v(-38.5, 151.34) * mm, "end": v(-0.31, 116.04) * mm});
            skSolve(sketch);
        }
        {
            var Q0;
            Q0=qCreatedBy(makeId("Top.planeOp"),FACE);
            cPlane(context, id + "F1", {"entities" : qUnion([Q0]), "cplaneType" : CPlaneType.OFFSET, "offset" : 53 * mm, "oppositeDirection" : true, "width" : 150 * mm, "height" : 150 * mm});
        }
        {
            var Q0;
            Q0=qCreatedBy(id+"F1.planeOp",FACE);
            var sketch = newSketch(context, id + "F2", { "sketchPlane" : qUnion([Q0])});
            skPoint(sketch, "E43", {"position": v(0, 0) * mm});
            skPoint(sketch, "E44.2.0", {"position": v(138.9, -207.87) * mm});
            skCircle(sketch, "E44.2.1", {"center": v(153.96, -197.8) * mm, "radius": 1.4 * mm});
            skCircle(sketch, "E44.2.2", {"center": v(123.83, -217.93) * mm, "radius": 1.4 * mm});
            skPoint(sketch, "E44.9.0", {"position": v(-75.53, 238.11) * mm});
            skLineSegment(sketch, "E45", {"start": v(-69.94, 214.6) * mm, "end": v(-55.24, 225) * mm});
            skLineSegment(sketch, "E46", {"start": v(-55.24, 225) * mm, "end": v(-74.52, 252.27) * mm});
            skLineSegment(sketch, "E47", {"start": v(-92.34, 246.3) * mm, "end": v(-69.94, 214.6) * mm});
            skCircle(sketch, "E48", {"center": v(-59.3, 236.81) * mm, "radius": 1.9 * mm});
            skCircle(sketch, "E49", {"center": v(-79.72, 222.38) * mm, "radius": 1.9 * mm});
            skPoint(sketch, "E50.center", {"position": v(0, -0.01) * mm});
            skLineSegment(sketch, "E51.bottom", {"start": v(-15, 22) * mm, "end": v(-10, 22) * mm});
            skLineSegment(sketch, "E51.top", {"start": v(-15, 17) * mm, "end": v(-10, 17) * mm});
            skLineSegment(sketch, "E51.left", {"start": v(-15, 22) * mm, "end": v(-15, 17) * mm});
            skLineSegment(sketch, "E51.right", {"start": v(-10, 22) * mm, "end": v(-10, 17) * mm});
            skLineSegment(sketch, "E52.bottom", {"start": v(10, 22) * mm, "end": v(15, 22) * mm});
            skLineSegment(sketch, "E52.top", {"start": v(10, 17) * mm, "end": v(15, 17) * mm});
            skLineSegment(sketch, "E52.left", {"start": v(10, 22) * mm, "end": v(10, 17) * mm});
            skLineSegment(sketch, "E52.right", {"start": v(15, 22) * mm, "end": v(15, 17) * mm});
            skLineSegment(sketch, "E53.bottom", {"start": v(-15, -17) * mm, "end": v(-10, -17) * mm});
            skLineSegment(sketch, "E53.top", {"start": v(-15, -22) * mm, "end": v(-10, -22) * mm});
            skLineSegment(sketch, "E53.left", {"start": v(-15, -17) * mm, "end": v(-15, -22) * mm});
            skLineSegment(sketch, "E53.right", {"start": v(-10, -17) * mm, "end": v(-10, -22) * mm});
            skLineSegment(sketch, "E54.bottom", {"start": v(10, -17) * mm, "end": v(15, -17) * mm});
            skLineSegment(sketch, "E54.top", {"start": v(10, -22) * mm, "end": v(15, -22) * mm});
            skLineSegment(sketch, "E54.left", {"start": v(10, -17) * mm, "end": v(10, -22) * mm});
            skLineSegment(sketch, "E54.right", {"start": v(15, -17) * mm, "end": v(15, -22) * mm});
            skCircle(sketch, "E55", {"center": v(0, 0) * mm, "radius": 16 * mm});
            skCircle(sketch, "E56", {"center": v(18.3, -55) * mm, "radius": 1.4 * mm});
            skCircle(sketch, "E57.MirrorC", {"center": v(-17.94, -55) * mm, "radius": 1.4 * mm});
            skPoint(sketch, "E58.13.0", {"position": v(0, -55) * mm});
            skLineSegment(sketch, "E59.0", {"start": v(-17.94, -55) * mm, "end": v(18.3, -55) * mm, "construction": true});
            skLineSegment(sketch, "E60.0", {"start": v(-10, -22) * mm, "end": v(15, -22) * mm, "construction": true});
            skLineSegment(sketch, "E61.0", {"start": v(-10, 17) * mm, "end": v(15, 17) * mm, "construction": true});
            skLineSegment(sketch, "E62.0", {"start": v(-10, 22) * mm, "end": v(10, 22) * mm, "construction": true});
            skLineSegment(sketch, "E63.0", {"start": v(-10, -17) * mm, "end": v(10, -17) * mm, "construction": true});
            skLineSegment(sketch, "E64.0", {"start": v(15, -22) * mm, "end": v(15, 17) * mm, "construction": true});
            skLineSegment(sketch, "E65.0", {"start": v(10, -17) * mm, "end": v(10, 17) * mm, "construction": true});
            skLineSegment(sketch, "E66.0", {"start": v(-15, -17) * mm, "end": v(-15, 17) * mm, "construction": true});
            skLineSegment(sketch, "E67.0", {"start": v(-10, -22) * mm, "end": v(-10, 17) * mm, "construction": true});
            skCircle(sketch, "E68.1.0", {"center": v(56.6, 11.96) * mm, "radius": 1.4 * mm});
            skLineSegment(sketch, "E68.1.1", {"start": v(56.6, 11.96) * mm, "end": v(38.49, 43.34) * mm, "construction": true});
            skPoint(sketch, "E68.1.2", {"position": v(47.63, 27.5) * mm});
            skCircle(sketch, "E68.1.3", {"center": v(38.49, 43.34) * mm, "radius": 1.4 * mm});
            skCircle(sketch, "E68.2.0", {"center": v(-38.66, 43.04) * mm, "radius": 1.4 * mm});
            skLineSegment(sketch, "E68.2.1", {"start": v(-38.66, 43.04) * mm, "end": v(-56.78, 11.66) * mm, "construction": true});
            skPoint(sketch, "E68.2.2", {"position": v(-47.63, 27.5) * mm});
            skCircle(sketch, "E68.2.3", {"center": v(-56.78, 11.66) * mm, "radius": 1.4 * mm});
            skLineSegment(sketch, "E69", {"start": v(119.48, 150) * mm, "end": v(141.55, 221.71) * mm});
            skLineSegment(sketch, "E70", {"start": v(90, -150) * mm, "end": v(158.96, -191.03) * mm});
            skLineSegment(sketch, "E71.left", {"start": v(874.64, -335.26) * mm, "end": v(846.64, -335.26) * mm});
            skLineSegment(sketch, "E71.right", {"start": v(882.69, -279.76) * mm, "end": v(838.59, -279.76) * mm});
            skCircle(sketch, "E72", {"center": v(865.64, -282.76) * mm, "radius": 1.4 * mm});
            skCircle(sketch, "E73", {"center": v(865.64, -330.76) * mm, "radius": 1.4 * mm});
            skLineSegment(sketch, "E74.top", {"start": v(871.64, -286.26) * mm, "end": v(871.64, -327.26) * mm});
            skPoint(sketch, "E75", {"position": v(860.64, -296.76) * mm});
            skCircle(sketch, "E76.MirrorC", {"center": v(855.64, -330.76) * mm, "radius": 1.4 * mm});
            skCircle(sketch, "E77.MirrorC", {"center": v(855.64, -282.76) * mm, "radius": 1.4 * mm});
            skLineSegment(sketch, "E78.MirrorCS", {"start": v(849.64, -286.26) * mm, "end": v(849.64, -327.26) * mm});
            skLineSegment(sketch, "E79", {"start": v(871.64, -327.26) * mm, "end": v(849.64, -327.26) * mm});
            skLineSegment(sketch, "E80", {"start": v(871.64, -286.26) * mm, "end": v(849.64, -286.26) * mm});
            skPoint(sketch, "E81", {"position": v(860.64, -286.26) * mm});
            skLineSegment(sketch, "E82.top", {"start": v(838.59, -301.76) * mm, "end": v(843.59, -301.76) * mm});
            skLineSegment(sketch, "E82.right", {"start": v(843.59, -296.76) * mm, "end": v(843.59, -301.76) * mm});
            skPoint(sketch, "E83", {"position": v(871.64, -306.76) * mm});
            skLineSegment(sketch, "E84", {"start": v(829.64, -261.76) * mm, "end": v(904.33, -261.76) * mm});
            skLineSegment(sketch, "E85.1.0", {"start": v(135.63, 58.7) * mm, "end": v(133.55, 54.04) * mm});
            skLineSegment(sketch, "E85.1.1", {"start": v(129.45, 64.74) * mm, "end": v(139.59, 60.22) * mm});
            skLineSegment(sketch, "E85.1.2", {"start": v(113.34, 28.56) * mm, "end": v(129.45, 64.74) * mm});
            skLineSegment(sketch, "E85.1.3", {"start": v(130.97, 60.77) * mm, "end": v(135.63, 58.7) * mm});
            skLineSegment(sketch, "E85.1.4", {"start": v(130.97, 60.77) * mm, "end": v(128.9, 56.12) * mm});
            skLineSegment(sketch, "E85.1.5", {"start": v(128.9, 56.12) * mm, "end": v(133.55, 54.04) * mm});
            skLineSegment(sketch, "E85.1.6", {"start": v(89.59, 39.13) * mm, "end": v(113.34, 28.56) * mm});
            skLineSegment(sketch, "E85.1.8", {"start": v(97.07, 75.86) * mm, "end": v(95, 71.2) * mm});
            skLineSegment(sketch, "E85.1.9", {"start": v(101.73, 73.8) * mm, "end": v(97.07, 75.86) * mm});
            skLineSegment(sketch, "E85.1.10", {"start": v(99.66, 69.13) * mm, "end": v(95, 71.2) * mm});
            skLineSegment(sketch, "E85.1.11", {"start": v(105.7, 75.31) * mm, "end": v(89.59, 39.13) * mm});
            skLineSegment(sketch, "E85.1.12", {"start": v(101.73, 73.8) * mm, "end": v(99.66, 69.13) * mm});
            skLineSegment(sketch, "E85.2.0", {"start": v(147.78, -1.54) * mm, "end": v(143.99, -4.95) * mm});
            skLineSegment(sketch, "E85.2.1", {"start": v(144.55, 6.46) * mm, "end": v(152.01, -1.76) * mm});
            skLineSegment(sketch, "E85.2.2", {"start": v(115.16, -20) * mm, "end": v(144.55, 6.46) * mm});
            skLineSegment(sketch, "E85.2.3", {"start": v(144.36, 2.25) * mm, "end": v(147.78, -1.54) * mm});
            skLineSegment(sketch, "E85.2.4", {"start": v(144.36, 2.25) * mm, "end": v(140.57, -1.16) * mm});
            skLineSegment(sketch, "E85.2.5", {"start": v(140.57, -1.16) * mm, "end": v(143.99, -4.95) * mm});
            skLineSegment(sketch, "E85.2.6", {"start": v(97.76, -0.69) * mm, "end": v(115.16, -20) * mm});
            skLineSegment(sketch, "E85.2.8", {"start": v(119.54, 29.82) * mm, "end": v(115.75, 26.41) * mm});
            skLineSegment(sketch, "E85.2.9", {"start": v(122.95, 26.03) * mm, "end": v(119.54, 29.82) * mm});
            skLineSegment(sketch, "E85.2.10", {"start": v(119.16, 22.62) * mm, "end": v(115.75, 26.41) * mm});
            skLineSegment(sketch, "E85.2.11", {"start": v(127.19, 25.81) * mm, "end": v(97.76, -0.69) * mm});
            skLineSegment(sketch, "E85.2.12", {"start": v(122.95, 26.03) * mm, "end": v(119.16, 22.62) * mm});
            skLineSegment(sketch, "E85.3.0", {"start": v(134.21, -61.68) * mm, "end": v(129.36, -63.26) * mm});
            skLineSegment(sketch, "E85.3.1", {"start": v(134.65, -52.64) * mm, "end": v(138.15, -63.44) * mm});
            skLineSegment(sketch, "E85.3.2", {"start": v(97.02, -64.86) * mm, "end": v(134.65, -52.64) * mm});
            skLineSegment(sketch, "E85.3.3", {"start": v(132.63, -56.83) * mm, "end": v(134.21, -61.68) * mm});
            skLineSegment(sketch, "E85.3.4", {"start": v(132.63, -56.83) * mm, "end": v(127.78, -58.4) * mm});
            skLineSegment(sketch, "E85.3.5", {"start": v(127.78, -58.4) * mm, "end": v(129.36, -63.26) * mm});
            skLineSegment(sketch, "E85.3.6", {"start": v(89, -40.16) * mm, "end": v(97.02, -64.86) * mm});
            skLineSegment(sketch, "E85.3.8", {"start": v(121.17, -21.55) * mm, "end": v(116.32, -23.12) * mm});
            skLineSegment(sketch, "E85.3.9", {"start": v(122.75, -26.4) * mm, "end": v(121.17, -21.55) * mm});
            skLineSegment(sketch, "E85.3.10", {"start": v(117.9, -27.97) * mm, "end": v(116.32, -23.12) * mm});
            skLineSegment(sketch, "E85.3.11", {"start": v(126.54, -27.95) * mm, "end": v(89, -40.16) * mm});
            skLineSegment(sketch, "E85.3.12", {"start": v(122.75, -26.4) * mm, "end": v(117.9, -27.97) * mm});
            skLineSegment(sketch, "E86", {"start": v(127.19, 25.81) * mm, "end": v(139.59, 60.22) * mm});
            skLineSegment(sketch, "E87", {"start": v(126.54, -27.95) * mm, "end": v(152.01, -1.76) * mm});
            skLineSegment(sketch, "E88", {"start": v(860.64, -286.26) * mm, "end": v(860.64, -329.43) * mm});
            skPoint(sketch, "E88.endSnap0", {"position": v(860.64, -327.26) * mm});
            skLineSegment(sketch, "E89", {"start": v(838.59, -301.76) * mm, "end": v(838.59, -279.76) * mm});
            skLineSegment(sketch, "E90", {"start": v(843.59, -296.76) * mm, "end": v(846.64, -296.76) * mm});
            skLineSegment(sketch, "E91", {"start": v(846.64, -296.76) * mm, "end": v(846.64, -335.26) * mm});
            skLineSegment(sketch, "E92", {"start": v(882.69, -301.76) * mm, "end": v(882.69, -279.76) * mm});
            skLineSegment(sketch, "E93", {"start": v(882.69, -301.76) * mm, "end": v(877.69, -301.76) * mm});
            skLineSegment(sketch, "E94", {"start": v(877.69, -301.76) * mm, "end": v(877.69, -296.76) * mm});
            skLineSegment(sketch, "E95", {"start": v(877.69, -296.76) * mm, "end": v(874.64, -296.76) * mm});
            skLineSegment(sketch, "E96", {"start": v(874.64, -296.76) * mm, "end": v(874.64, -335.26) * mm});
            skLineSegment(sketch, "E97.bottom", {"start": v(502.55, 357.04) * mm, "end": v(452.58, 357.04) * mm});
            skLineSegment(sketch, "E97.top", {"start": v(502.55, 369.04) * mm, "end": v(452.58, 369.04) * mm});
            skPoint(sketch, "E98.visualSharp", {"position": v(447.55, 369.04) * mm});
            skPoint(sketch, "E99.visualSharp", {"position": v(447.55, 357.04) * mm});
            skPoint(sketch, "E100.visualSharp", {"position": v(507.55, 357.04) * mm});
            skPoint(sketch, "E101.visualSharp", {"position": v(507.55, 369.04) * mm});
            skPoint(sketch, "E102", {"position": v(477.55, 363.04) * mm});
            skArc(sketch, "E103", {"start": v(476.13, 364.41) * mm, "mid": v(477.55, 361.06) * mm, "end": v(478.97, 364.41) * mm});
            skLineSegment(sketch, "E104", {"start": v(476.13, 364.41) * mm, "end": v(478.97, 364.41) * mm});
            skPoint(sketch, "E105.middle", {"position": v(543.86, -319.04) * mm});
            skPoint(sketch, "E106", {"position": v(543.86, -327.54) * mm});
            skPoint(sketch, "E107", {"position": v(543.86, -310.54) * mm});
            skCircle(sketch, "E108", {"center": v(543.86, -310.54) * mm, "radius": 2 * mm});
            skCircle(sketch, "E109", {"center": v(543.86, -327.54) * mm, "radius": 2 * mm});
            skCircle(sketch, "E110", {"center": v(543.86, -319.04) * mm, "radius": 5.5 * mm});
            skLineSegment(sketch, "E111.bottom", {"start": v(561.86, -344.04) * mm, "end": v(525.86, -344.04) * mm});
            skLineSegment(sketch, "E111.top", {"start": v(561.86, -294.04) * mm, "end": v(525.86, -294.04) * mm});
            skLineSegment(sketch, "E111.left", {"start": v(561.86, -344.04) * mm, "end": v(561.86, -340.04) * mm});
            skLineSegment(sketch, "E111.right", {"start": v(525.86, -344.04) * mm, "end": v(525.86, -340.04) * mm});
            skLineSegment(sketch, "E112.bottom", {"start": v(528.81, -297.04) * mm, "end": v(533.91, -297.04) * mm});
            skLineSegment(sketch, "E112.top", {"start": v(528.81, -302.14) * mm, "end": v(533.91, -302.14) * mm});
            skLineSegment(sketch, "E112.left", {"start": v(528.81, -297.04) * mm, "end": v(528.81, -302.14) * mm});
            skLineSegment(sketch, "E112.right", {"start": v(533.91, -297.04) * mm, "end": v(533.91, -302.14) * mm});
            skLineSegment(sketch, "E113.bottom", {"start": v(553.81, -297.04) * mm, "end": v(558.91, -297.04) * mm});
            skLineSegment(sketch, "E113.top", {"start": v(553.81, -302.14) * mm, "end": v(558.91, -302.14) * mm});
            skLineSegment(sketch, "E113.left", {"start": v(553.81, -297.04) * mm, "end": v(553.81, -302.14) * mm});
            skLineSegment(sketch, "E113.right", {"start": v(558.91, -297.04) * mm, "end": v(558.91, -302.14) * mm});
            skLineSegment(sketch, "E114.bottom", {"start": v(528.81, -335.94) * mm, "end": v(533.91, -335.94) * mm});
            skLineSegment(sketch, "E114.top", {"start": v(528.81, -341.04) * mm, "end": v(533.91, -341.04) * mm});
            skLineSegment(sketch, "E114.left", {"start": v(528.81, -335.94) * mm, "end": v(528.81, -341.04) * mm});
            skLineSegment(sketch, "E114.right", {"start": v(533.91, -335.94) * mm, "end": v(533.91, -341.04) * mm});
            skLineSegment(sketch, "E115.bottom", {"start": v(553.81, -335.94) * mm, "end": v(558.91, -335.94) * mm});
            skLineSegment(sketch, "E115.top", {"start": v(553.81, -341.04) * mm, "end": v(558.91, -341.04) * mm});
            skLineSegment(sketch, "E115.left", {"start": v(553.81, -335.94) * mm, "end": v(553.81, -341.04) * mm});
            skLineSegment(sketch, "E115.right", {"start": v(558.91, -335.94) * mm, "end": v(558.91, -341.04) * mm});
            skPoint(sketch, "E116", {"position": v(561.86, -319.04) * mm});
            skLineSegment(sketch, "E117", {"start": v(564.86, -312.04) * mm, "end": v(569.86, -312.04) * mm});
            skLineSegment(sketch, "E118", {"start": v(569.86, -312.04) * mm, "end": v(569.86, -317.04) * mm});
            skLineSegment(sketch, "E119", {"start": v(569.86, -317.04) * mm, "end": v(589.86, -317.04) * mm});
            skLineSegment(sketch, "E120", {"start": v(589.86, -317.04) * mm, "end": v(589.86, -312.04) * mm});
            skLineSegment(sketch, "E121", {"start": v(589.86, -312.04) * mm, "end": v(594.86, -312.04) * mm});
            skLineSegment(sketch, "E122", {"start": v(594.86, -312.04) * mm, "end": v(594.86, -317.04) * mm});
            skLineSegment(sketch, "E123", {"start": v(594.86, -317.04) * mm, "end": v(597.86, -317.04) * mm});
            skLineSegment(sketch, "E124", {"start": v(597.86, -317.04) * mm, "end": v(597.86, -340.04) * mm});
            skLineSegment(sketch, "E125", {"start": v(561.86, -340.04) * mm, "end": v(561.86, -317.04) * mm});
            skLineSegment(sketch, "E126", {"start": v(561.86, -317.04) * mm, "end": v(564.86, -317.04) * mm});
            skLineSegment(sketch, "E127", {"start": v(564.86, -317.04) * mm, "end": v(564.86, -312.04) * mm});
            skLineSegment(sketch, "E128", {"start": v(597.86, -340.04) * mm, "end": v(594.86, -340.04) * mm});
            skLineSegment(sketch, "E129", {"start": v(594.86, -340.04) * mm, "end": v(594.86, -345.04) * mm});
            skLineSegment(sketch, "E130", {"start": v(594.86, -345.04) * mm, "end": v(589.86, -345.04) * mm});
            skLineSegment(sketch, "E131", {"start": v(589.86, -345.04) * mm, "end": v(589.86, -340.04) * mm});
            skLineSegment(sketch, "E132", {"start": v(589.86, -340.04) * mm, "end": v(569.86, -340.04) * mm});
            skLineSegment(sketch, "E133", {"start": v(569.86, -340.04) * mm, "end": v(569.86, -345.04) * mm});
            skLineSegment(sketch, "E134", {"start": v(569.86, -345.04) * mm, "end": v(564.86, -345.04) * mm});
            skLineSegment(sketch, "E135", {"start": v(564.86, -345.04) * mm, "end": v(564.86, -340.04) * mm});
            skLineSegment(sketch, "E136", {"start": v(564.86, -340.04) * mm, "end": v(561.86, -340.04) * mm});
            skPoint(sketch, "E137", {"position": v(579.86, -317.04) * mm});
            skLineSegment(sketch, "E138", {"start": v(492.86, -312.04) * mm, "end": v(497.86, -312.04) * mm});
            skLineSegment(sketch, "E139", {"start": v(497.86, -312.04) * mm, "end": v(497.86, -317.04) * mm});
            skLineSegment(sketch, "E140", {"start": v(497.86, -317.04) * mm, "end": v(517.86, -317.04) * mm});
            skLineSegment(sketch, "E141", {"start": v(517.86, -317.04) * mm, "end": v(517.86, -312.04) * mm});
            skLineSegment(sketch, "E142", {"start": v(517.86, -312.04) * mm, "end": v(522.86, -312.04) * mm});
            skLineSegment(sketch, "E143", {"start": v(522.86, -312.04) * mm, "end": v(522.86, -317.04) * mm});
            skLineSegment(sketch, "E144", {"start": v(522.86, -317.04) * mm, "end": v(525.86, -317.04) * mm});
            skLineSegment(sketch, "E145", {"start": v(525.86, -317.04) * mm, "end": v(525.86, -340.04) * mm});
            skLineSegment(sketch, "E146", {"start": v(489.86, -340.04) * mm, "end": v(489.86, -317.04) * mm});
            skLineSegment(sketch, "E147", {"start": v(489.86, -317.04) * mm, "end": v(492.86, -317.04) * mm});
            skLineSegment(sketch, "E148", {"start": v(492.86, -317.04) * mm, "end": v(492.86, -312.04) * mm});
            skLineSegment(sketch, "E149", {"start": v(525.86, -340.04) * mm, "end": v(522.86, -340.04) * mm});
            skLineSegment(sketch, "E150", {"start": v(522.86, -340.04) * mm, "end": v(522.86, -345.04) * mm});
            skLineSegment(sketch, "E151", {"start": v(522.86, -345.04) * mm, "end": v(517.86, -345.04) * mm});
            skLineSegment(sketch, "E152", {"start": v(517.86, -345.04) * mm, "end": v(517.86, -340.04) * mm});
            skLineSegment(sketch, "E153", {"start": v(517.86, -340.04) * mm, "end": v(497.86, -340.04) * mm});
            skLineSegment(sketch, "E154", {"start": v(497.86, -340.04) * mm, "end": v(497.86, -345.04) * mm});
            skLineSegment(sketch, "E155", {"start": v(497.86, -345.04) * mm, "end": v(492.86, -345.04) * mm});
            skLineSegment(sketch, "E156", {"start": v(492.86, -345.04) * mm, "end": v(492.86, -340.04) * mm});
            skLineSegment(sketch, "E157", {"start": v(492.86, -340.04) * mm, "end": v(489.86, -340.04) * mm});
            skPoint(sketch, "E158", {"position": v(507.86, -317.04) * mm});
            skLineSegment(sketch, "E159.trimOffspring", {"start": v(561.86, -317.04) * mm, "end": v(561.86, -294.04) * mm});
            skLineSegment(sketch, "E160.trimOffspring", {"start": v(525.86, -317.04) * mm, "end": v(525.86, -294.04) * mm});
            skLineSegment(sketch, "E161", {"start": v(447.58, 364.05) * mm, "end": v(447.58, 362.05) * mm});
            skLineSegment(sketch, "E162", {"start": v(507.55, 364.04) * mm, "end": v(507.55, 362.04) * mm});
            skArc(sketch, "E163.filletArc", {"start": v(452.58, 369.04) * mm, "mid": v(449.05, 367.58) * mm, "end": v(447.58, 364.05) * mm});
            skPoint(sketch, "E164.newPointA", {"position": v(447.55, 352.22) * mm});
            skArc(sketch, "E164.filletArc", {"start": v(447.58, 362.05) * mm, "mid": v(449.04, 358.5) * mm, "end": v(452.58, 357.04) * mm});
            skArc(sketch, "E165.filletArc", {"start": v(507.55, 364.04) * mm, "mid": v(506.09, 367.57) * mm, "end": v(502.55, 369.04) * mm});
            skArc(sketch, "E166.filletArc", {"start": v(502.55, 357.04) * mm, "mid": v(506.09, 358.5) * mm, "end": v(507.55, 362.04) * mm});
            skLineSegment(sketch, "E167", {"start": v(158.96, -209.58) * mm, "end": v(158.96, -191.03) * mm});
            skLineSegment(sketch, "E168.1.0", {"start": v(104.23, -77) * mm, "end": v(138.15, -63.44) * mm});
            skLineSegment(sketch, "E168.1.1", {"start": v(101.93, -68.97) * mm, "end": v(96.86, -68.44) * mm});
            skLineSegment(sketch, "E168.1.2", {"start": v(101.4, -74.04) * mm, "end": v(101.93, -68.97) * mm});
            skLineSegment(sketch, "E168.1.3", {"start": v(104.23, -77) * mm, "end": v(64.97, -72.88) * mm});
            skLineSegment(sketch, "E168.1.4", {"start": v(101.4, -74.04) * mm, "end": v(96.32, -73.5) * mm});
            skLineSegment(sketch, "E168.1.5", {"start": v(96.32, -73.5) * mm, "end": v(96.86, -68.44) * mm});
            skLineSegment(sketch, "E168.1.6", {"start": v(64.97, -72.88) * mm, "end": v(62.25, -98.72) * mm});
            skLineSegment(sketch, "E168.1.7", {"start": v(101.6, -102.85) * mm, "end": v(100.4, -114.15) * mm});
            skLineSegment(sketch, "E168.1.8", {"start": v(62.25, -98.72) * mm, "end": v(101.6, -102.85) * mm});
            skLineSegment(sketch, "E168.1.9", {"start": v(98.05, -105.87) * mm, "end": v(97.52, -110.94) * mm});
            skLineSegment(sketch, "E168.1.10", {"start": v(98.05, -105.87) * mm, "end": v(92.98, -105.33) * mm});
            skLineSegment(sketch, "E168.1.11", {"start": v(92.98, -105.33) * mm, "end": v(92.45, -110.4) * mm});
            skLineSegment(sketch, "E168.1.12", {"start": v(97.52, -110.94) * mm, "end": v(92.45, -110.4) * mm});
            skLineSegment(sketch, "E169", {"start": v(105.7, 75.31) * mm, "end": v(105.7, 150) * mm});
            skPoint(sketch, "E170.orphan", {"position": v(105.7, 150) * mm});
            skLineSegment(sketch, "E171", {"start": v(100.4, -114.15) * mm, "end": v(90, -150) * mm});
            skLineSegment(sketch, "E172", {"start": v(615.16, -166) * mm, "end": v(615.16, -163) * mm});
            skLineSegment(sketch, "E173.top", {"start": v(615.16, -163) * mm, "end": v(611.66, -163) * mm});
            skLineSegment(sketch, "E173.right", {"start": v(611.66, -166) * mm, "end": v(611.66, -163) * mm});
            skPoint(sketch, "E174", {"position": v(611.66, -166) * mm});
            skLineSegment(sketch, "E175", {"start": v(616.77, -120.1) * mm, "end": v(642.65, -141.8) * mm});
            skLineSegment(sketch, "E176", {"start": v(618.7, -117.8) * mm, "end": v(644.58, -139.5) * mm});
            skPoint(sketch, "E177", {"position": v(621, -119.72) * mm});
            skLineSegment(sketch, "E178", {"start": v(616.77, -120.1) * mm, "end": v(618.7, -117.8) * mm});
            skLineSegment(sketch, "E179", {"start": v(615.16, -166) * mm, "end": v(634.93, -166) * mm});
            skLineSegment(sketch, "E180", {"start": v(615.16, -163) * mm, "end": v(634.93, -163) * mm});
            skLineSegment(sketch, "E181.bottom", {"start": v(615.16, -166) * mm, "end": v(611.66, -166) * mm});
            skArc(sketch, "E182.filletArc", {"start": v(634.93, -163) * mm, "mid": v(646.21, -155.1) * mm, "end": v(642.65, -141.8) * mm});
            skArc(sketch, "E183", {"start": v(634.93, -166) * mm, "mid": v(649.03, -156.13) * mm, "end": v(644.58, -139.5) * mm});
            skPoint(sketch, "E184", {"position": v(640.92, -136.43) * mm});
            skPoint(sketch, "E185", {"position": v(864.13, -283.72) * mm});
            skLineSegment(sketch, "E186", {"start": v(860.27, -282.69) * mm, "end": v(864.35, -267.47) * mm});
            skLineSegment(sketch, "E187", {"start": v(868, -284.76) * mm, "end": v(870.75, -274.47) * mm});
            skLineSegment(sketch, "E188", {"start": v(875.58, -270.76) * mm, "end": v(955.73, -270.76) * mm});
            skArc(sketch, "E189", {"start": v(860.27, -282.69) * mm, "mid": v(863.1, -287.59) * mm, "end": v(868, -284.76) * mm});
            skPoint(sketch, "E190.visualSharp", {"position": v(865.34, -263.76) * mm});
            skArc(sketch, "E190.filletArc", {"start": v(869.18, -263.76) * mm, "mid": v(866.13, -264.8) * mm, "end": v(864.35, -267.47) * mm});
            skPoint(sketch, "E191.visualSharp", {"position": v(871.75, -270.76) * mm});
            skArc(sketch, "E191.filletArc", {"start": v(875.58, -270.76) * mm, "mid": v(872.54, -271.8) * mm, "end": v(870.75, -274.47) * mm});
            skLineSegment(sketch, "E192", {"start": v(955.73, -263.76) * mm, "end": v(955.73, -270.76) * mm});
            skLineSegment(sketch, "E193", {"start": v(864.13, -283.72) * mm, "end": v(860.64, -296.76) * mm});
            skLineSegment(sketch, "E194", {"start": v(864.13, -283.72) * mm, "end": v(866.46, -275.03) * mm});
            skPoint(sketch, "E195", {"position": v(866.46, -275.03) * mm});
            skCircle(sketch, "E196", {"center": v(864.13, -283.72) * mm, "radius": 1.2 * mm});
            skCircle(sketch, "E197", {"center": v(866.46, -275.03) * mm, "radius": 1.2 * mm});
            skLineSegment(sketch, "E198", {"start": v(869.18, -263.76) * mm, "end": v(888.95, -263.76) * mm});
            skLineSegment(sketch, "E199", {"start": v(888.95, -263.76) * mm, "end": v(921.95, -263.76) * mm});
            skLineSegment(sketch, "E200", {"start": v(921.95, -263.76) * mm, "end": v(955.73, -263.76) * mm});
            skPoint(sketch, "E201", {"position": v(905.45, -263.76) * mm});
            skCircle(sketch, "E202", {"center": v(952.73, -267.26) * mm, "radius": 0.95 * mm});
            skPoint(sketch, "E202.centerSnap0", {"position": v(955.73, -267.26) * mm});
            skCircle(sketch, "E203", {"center": v(926.73, -267.26) * mm, "radius": 0.95 * mm});
            skLineSegment(sketch, "E204", {"start": v(116.35, 67.28) * mm, "end": v(124.9, 86.47) * mm});
            skLineSegment(sketch, "E205", {"start": v(128.08, 85.05) * mm, "end": v(129.3, 87.79) * mm});
            skLineSegment(sketch, "E206.top", {"start": v(129.3, 87.79) * mm, "end": v(126.11, 89.2) * mm});
            skLineSegment(sketch, "E206.right", {"start": v(124.9, 86.47) * mm, "end": v(126.11, 89.2) * mm});
            skPoint(sketch, "E207", {"position": v(124.9, 86.47) * mm});
            skLineSegment(sketch, "E208", {"start": v(148.23, 126.32) * mm, "end": v(163.04, 95.97) * mm});
            skLineSegment(sketch, "E209", {"start": v(150.93, 127.64) * mm, "end": v(165.73, 97.28) * mm});
            skPoint(sketch, "E210", {"position": v(152.24, 124.94) * mm});
            skLineSegment(sketch, "E211", {"start": v(148.23, 126.32) * mm, "end": v(150.93, 127.64) * mm});
            skLineSegment(sketch, "E212", {"start": v(128.08, 85.05) * mm, "end": v(146.15, 77) * mm});
            skLineSegment(sketch, "E213", {"start": v(129.3, 87.79) * mm, "end": v(147.37, 79.74) * mm});
            skLineSegment(sketch, "E214.bottom", {"start": v(128.08, 85.05) * mm, "end": v(124.9, 86.47) * mm});
            skArc(sketch, "E215.filletArc", {"start": v(147.37, 79.74) * mm, "mid": v(160.88, 82.37) * mm, "end": v(163.04, 95.97) * mm});
            skArc(sketch, "E216", {"start": v(146.15, 77) * mm, "mid": v(163.04, 80.29) * mm, "end": v(165.73, 97.28) * mm});
            skPoint(sketch, "E217", {"position": v(163.64, 101.57) * mm});
            skLineSegment(sketch, "E218.0", {"start": v(126.11, 89.2) * mm, "end": v(129.3, 87.79) * mm, "construction": true});
            skPoint(sketch, "E219.8.0", {"position": v(121.6, 218.42) * mm});
            skCircle(sketch, "E219.8.1", {"center": v(108.92, 225.47) * mm, "radius": 1.4 * mm});
            skCircle(sketch, "E219.8.2", {"center": v(134.27, 211.38) * mm, "radius": 1.4 * mm});
            skLineSegment(sketch, "E220", {"start": v(108.92, 225.47) * mm, "end": v(134.27, 211.38) * mm});
            skPoint(sketch, "E221.center", {"position": v(326.1, 140.14) * mm});
            skLineSegment(sketch, "E222", {"start": v(105.43, 227.41) * mm, "end": v(137.77, 209.43) * mm});
            skPoint(sketch, "E223", {"position": v(0, 0.02) * mm});
            skPoint(sketch, "E224.8.0", {"position": v(-16.98, 249.43) * mm});
            skCircle(sketch, "E224.8.1", {"center": v(-31.45, 248.43) * mm, "radius": 1.4 * mm});
            skCircle(sketch, "E224.8.2", {"center": v(-2.52, 250.42) * mm, "radius": 1.4 * mm});
            skPoint(sketch, "E225.1.0", {"position": v(54.56, 243.98) * mm});
            skCircle(sketch, "E225.1.1", {"center": v(68.71, 240.82) * mm, "radius": 1.4 * mm});
            skCircle(sketch, "E225.1.2", {"center": v(40.4, 247.13) * mm, "radius": 1.4 * mm});
            skLineSegment(sketch, "E225.anchor1", {"start": v(0, 0) * mm, "end": v(-31.45, 248.43) * mm, "construction": true});
            skLineSegment(sketch, "E225.anchor2", {"start": v(0, 0) * mm, "end": v(40.4, 247.13) * mm, "construction": true});
            skPoint(sketch, "E226.1.0", {"position": v(76.22, -238.1) * mm});
            skCircle(sketch, "E226.1.1", {"center": v(58.96, -243.62) * mm, "radius": 1.4 * mm});
            skCircle(sketch, "E226.1.2", {"center": v(93.47, -232.58) * mm, "radius": 1.4 * mm});
            skPoint(sketch, "E226.2.0", {"position": v(7.63, -249.88) * mm});
            skCircle(sketch, "E226.2.1", {"center": v(-10.47, -250.44) * mm, "radius": 1.4 * mm});
            skCircle(sketch, "E226.2.2", {"center": v(25.74, -249.33) * mm, "radius": 1.4 * mm});
            skPoint(sketch, "E226.3.0", {"position": v(-61.54, -242.3) * mm});
            skCircle(sketch, "E226.3.1", {"center": v(-79.1, -237.85) * mm, "radius": 1.4 * mm});
            skCircle(sketch, "E226.3.2", {"center": v(-43.98, -246.77) * mm, "radius": 1.4 * mm});
            skPoint(sketch, "E226.4.0", {"position": v(-125.94, -215.96) * mm});
            skCircle(sketch, "E226.4.1", {"center": v(-141.6, -206.83) * mm, "radius": 1.4 * mm});
            skCircle(sketch, "E226.4.2", {"center": v(-110.3, -225.09) * mm, "radius": 1.4 * mm});
            skPoint(sketch, "E226.5.0", {"position": v(-180.6, -172.88) * mm});
            skCircle(sketch, "E226.5.1", {"center": v(-193.12, -159.8) * mm, "radius": 1.4 * mm});
            skCircle(sketch, "E226.5.2", {"center": v(-168.06, -185.97) * mm, "radius": 1.4 * mm});
            skPoint(sketch, "E226.6.0", {"position": v(-221.25, -116.4) * mm});
            skCircle(sketch, "E226.6.1", {"center": v(-229.68, -100.37) * mm, "radius": 1.4 * mm});
            skCircle(sketch, "E226.6.2", {"center": v(-212.81, -132.44) * mm, "radius": 1.4 * mm});
            skPoint(sketch, "E226.7.0", {"position": v(-244.76, -50.91) * mm});
            skCircle(sketch, "E226.7.1", {"center": v(-248.45, -33.17) * mm, "radius": 1.4 * mm});
            skCircle(sketch, "E226.7.2", {"center": v(-241.07, -68.65) * mm, "radius": 1.4 * mm});
            skPoint(sketch, "E226.8.0", {"position": v(-249.31, 18.53) * mm});
            skCircle(sketch, "E226.8.1", {"center": v(-247.97, 36.6) * mm, "radius": 1.4 * mm});
            skCircle(sketch, "E226.8.2", {"center": v(-250.66, 0.46) * mm, "radius": 1.4 * mm});
            skPoint(sketch, "E226.9.0", {"position": v(-234.55, 86.53) * mm});
            skCircle(sketch, "E226.9.1", {"center": v(-228.28, 103.53) * mm, "radius": 1.4 * mm});
            skCircle(sketch, "E226.9.2", {"center": v(-240.82, 69.53) * mm, "radius": 1.4 * mm});
            skPoint(sketch, "E226.10.0", {"position": v(-201.61, 147.83) * mm});
            skCircle(sketch, "E226.10.1", {"center": v(-190.9, 162.44) * mm, "radius": 1.4 * mm});
            skCircle(sketch, "E226.10.2", {"center": v(-212.32, 133.22) * mm, "radius": 1.4 * mm});
            skPoint(sketch, "E226.11.0", {"position": v(-153.05, 197.67) * mm});
            skCircle(sketch, "E226.11.1", {"center": v(-138.73, 208.76) * mm, "radius": 1.4 * mm});
            skCircle(sketch, "E226.11.2", {"center": v(-167.38, 186.58) * mm, "radius": 1.4 * mm});
            skLineSegment(sketch, "E226.anchor1", {"start": v(0, 0) * mm, "end": v(123.83, -217.93) * mm, "construction": true});
            skLineSegment(sketch, "E226.anchor2", {"start": v(0, 0) * mm, "end": v(-138.73, 208.76) * mm, "construction": true});
            skLineSegment(sketch, "E227", {"start": v(105.7, 150) * mm, "end": v(119.48, 150) * mm});
            skArc(sketch, "E228", {"start": v(141.55, 221.71) * mm, "mid": v(36.83, 260.45) * mm, "end": v(-74.52, 252.27) * mm});
            skArc(sketch, "E229.trimOffspring", {"start": v(-92.34, 246.3) * mm, "mid": v(-230.36, -126.98) * mm, "end": v(158.96, -209.58) * mm});
            skCircle(sketch, "E230", {"center": v(829.68, 115.9) * mm, "radius": 3 * mm});
            skPoint(sketch, "E230.centerSnap0", {"position": v(829.68, 140.4) * mm});
            skLineSegment(sketch, "E231.top", {"start": v(826.63, 120.4) * mm, "end": v(828.73, 120.4) * mm});
            skLineSegment(sketch, "E231.left", {"start": v(826.63, 140.4) * mm, "end": v(826.63, 120.4) * mm});
            skLineSegment(sketch, "E231.right", {"start": v(828.73, 140.4) * mm, "end": v(828.73, 120.4) * mm});
            skLineSegment(sketch, "E232.bottom", {"start": v(826.63, 110.9) * mm, "end": v(828.73, 110.9) * mm});
            skLineSegment(sketch, "E232.top", {"start": v(826.63, 102.9) * mm, "end": v(828.73, 102.9) * mm});
            skLineSegment(sketch, "E232.left", {"start": v(826.63, 110.9) * mm, "end": v(826.63, 102.9) * mm});
            skLineSegment(sketch, "E232.right", {"start": v(828.73, 110.9) * mm, "end": v(828.73, 102.9) * mm});
            skLineSegment(sketch, "E233.trimOffspring", {"start": v(828.73, 140.4) * mm, "end": v(830.63, 140.4) * mm});
            skLineSegment(sketch, "E234.MirrorCS", {"start": v(832.73, 102.9) * mm, "end": v(830.63, 102.9) * mm});
            skLineSegment(sketch, "E235.MirrorCS", {"start": v(832.73, 110.9) * mm, "end": v(830.63, 110.9) * mm});
            skLineSegment(sketch, "E236.MirrorCS", {"start": v(830.63, 140.4) * mm, "end": v(830.63, 120.4) * mm});
            skLineSegment(sketch, "E237.MirrorCS", {"start": v(832.73, 120.4) * mm, "end": v(830.63, 120.4) * mm});
            skLineSegment(sketch, "E238.MirrorCS", {"start": v(832.73, 110.9) * mm, "end": v(832.73, 102.9) * mm});
            skLineSegment(sketch, "E239.MirrorCS", {"start": v(830.63, 110.9) * mm, "end": v(830.63, 102.9) * mm});
            skLineSegment(sketch, "E240.MirrorCS", {"start": v(832.73, 140.4) * mm, "end": v(832.73, 120.4) * mm});
            skLineSegment(sketch, "E241.bottom", {"start": v(839.68, 160.4) * mm, "end": v(819.68, 160.4) * mm});
            skLineSegment(sketch, "E241.top", {"start": v(839.68, 140.4) * mm, "end": v(819.68, 140.4) * mm});
            skLineSegment(sketch, "E241.left", {"start": v(839.68, 160.4) * mm, "end": v(839.68, 140.4) * mm});
            skLineSegment(sketch, "E241.right", {"start": v(819.68, 160.4) * mm, "end": v(819.68, 140.4) * mm});
            skPoint(sketch, "E241.middle", {"position": v(829.68, 150.4) * mm});
            skCircle(sketch, "E242", {"center": v(-214.04, -16.75) * mm, "radius": 3 * mm});
            skPoint(sketch, "E242.centerSnap0", {"position": v(-238.54, -16.75) * mm});
            skLineSegment(sketch, "E243.top", {"start": v(-218.54, -19.8) * mm, "end": v(-218.54, -17.7) * mm});
            skLineSegment(sketch, "E243.left", {"start": v(-238.54, -19.8) * mm, "end": v(-218.54, -19.8) * mm});
            skLineSegment(sketch, "E243.right", {"start": v(-238.54, -17.7) * mm, "end": v(-218.54, -17.7) * mm});
            skLineSegment(sketch, "E244.bottom", {"start": v(-209.04, -19.8) * mm, "end": v(-209.04, -17.7) * mm});
            skLineSegment(sketch, "E244.top", {"start": v(-201.04, -19.8) * mm, "end": v(-201.04, -17.7) * mm});
            skLineSegment(sketch, "E244.left", {"start": v(-209.04, -19.8) * mm, "end": v(-201.04, -19.8) * mm});
            skLineSegment(sketch, "E244.right", {"start": v(-209.04, -17.7) * mm, "end": v(-201.04, -17.7) * mm});
            skLineSegment(sketch, "E245.MirrorCS", {"start": v(-201.04, -13.7) * mm, "end": v(-201.04, -15.8) * mm});
            skLineSegment(sketch, "E246.MirrorCS", {"start": v(-209.04, -13.7) * mm, "end": v(-209.04, -15.8) * mm});
            skLineSegment(sketch, "E247.MirrorCS", {"start": v(-238.54, -15.8) * mm, "end": v(-218.54, -15.8) * mm});
            skLineSegment(sketch, "E248.MirrorCS", {"start": v(-218.54, -13.7) * mm, "end": v(-218.54, -15.8) * mm});
            skLineSegment(sketch, "E249.MirrorCS", {"start": v(-209.04, -13.7) * mm, "end": v(-201.04, -13.7) * mm});
            skLineSegment(sketch, "E250.MirrorCS", {"start": v(-209.04, -15.8) * mm, "end": v(-201.04, -15.8) * mm});
            skLineSegment(sketch, "E251.MirrorCS", {"start": v(-238.54, -13.7) * mm, "end": v(-218.54, -13.7) * mm});
            skPoint(sketch, "E252.middle", {"position": v(-248.54, -16.75) * mm});
            skLineSegment(sketch, "E253", {"start": v(-238.54, -19.8) * mm, "end": v(-238.54, -17.7) * mm});
            skLineSegment(sketch, "E254", {"start": v(-238.54, -15.8) * mm, "end": v(-238.54, -13.7) * mm});
            skCircle(sketch, "E255", {"center": v(83.76, 211.9) * mm, "radius": 3 * mm});
            skPoint(sketch, "E255.centerSnap0", {"position": v(108.26, 211.9) * mm});
            skLineSegment(sketch, "E256.top", {"start": v(88.26, 214.95) * mm, "end": v(88.26, 212.85) * mm});
            skLineSegment(sketch, "E256.left", {"start": v(108.26, 214.95) * mm, "end": v(88.26, 214.95) * mm});
            skLineSegment(sketch, "E256.right", {"start": v(108.26, 212.85) * mm, "end": v(88.26, 212.85) * mm});
            skLineSegment(sketch, "E257.bottom", {"start": v(78.76, 214.95) * mm, "end": v(78.76, 212.85) * mm});
            skLineSegment(sketch, "E257.top", {"start": v(70.76, 214.95) * mm, "end": v(70.76, 212.85) * mm});
            skLineSegment(sketch, "E257.left", {"start": v(78.76, 214.95) * mm, "end": v(70.76, 214.95) * mm});
            skLineSegment(sketch, "E257.right", {"start": v(78.76, 212.85) * mm, "end": v(70.76, 212.85) * mm});
            skLineSegment(sketch, "E258.MirrorCS", {"start": v(70.76, 208.85) * mm, "end": v(70.76, 210.95) * mm});
            skLineSegment(sketch, "E259.MirrorCS", {"start": v(78.76, 208.85) * mm, "end": v(78.76, 210.95) * mm});
            skLineSegment(sketch, "E260.MirrorCS", {"start": v(108.26, 210.95) * mm, "end": v(88.26, 210.95) * mm});
            skLineSegment(sketch, "E261.MirrorCS", {"start": v(88.26, 208.85) * mm, "end": v(88.26, 210.95) * mm});
            skLineSegment(sketch, "E262.MirrorCS", {"start": v(78.76, 208.85) * mm, "end": v(70.76, 208.85) * mm});
            skLineSegment(sketch, "E263.MirrorCS", {"start": v(78.76, 210.95) * mm, "end": v(70.76, 210.95) * mm});
            skLineSegment(sketch, "E264.MirrorCS", {"start": v(108.26, 208.85) * mm, "end": v(88.26, 208.85) * mm});
            skPoint(sketch, "E265.middle", {"position": v(118.26, 211.9) * mm});
            skLineSegment(sketch, "E266", {"start": v(108.26, 208.85) * mm, "end": v(108.26, 210.95) * mm});
            skLineSegment(sketch, "E267", {"start": v(108.26, 212.85) * mm, "end": v(108.26, 214.95) * mm});
            skCircle(sketch, "E268", {"center": v(83.76, -207.83) * mm, "radius": 3 * mm});
            skPoint(sketch, "E268.centerSnap0", {"position": v(108.26, -207.83) * mm});
            skLineSegment(sketch, "E269.top", {"start": v(88.26, -204.78) * mm, "end": v(88.26, -206.88) * mm});
            skLineSegment(sketch, "E269.left", {"start": v(108.26, -204.78) * mm, "end": v(88.26, -204.78) * mm});
            skLineSegment(sketch, "E269.right", {"start": v(108.26, -206.88) * mm, "end": v(88.26, -206.88) * mm});
            skLineSegment(sketch, "E270.bottom", {"start": v(78.76, -204.78) * mm, "end": v(78.76, -206.88) * mm});
            skLineSegment(sketch, "E270.top", {"start": v(70.76, -204.78) * mm, "end": v(70.76, -206.88) * mm});
            skLineSegment(sketch, "E270.left", {"start": v(78.76, -204.78) * mm, "end": v(70.76, -204.78) * mm});
            skLineSegment(sketch, "E270.right", {"start": v(78.76, -206.88) * mm, "end": v(70.76, -206.88) * mm});
            skLineSegment(sketch, "E271.MirrorCS", {"start": v(70.76, -210.88) * mm, "end": v(70.76, -208.78) * mm});
            skLineSegment(sketch, "E272.MirrorCS", {"start": v(78.76, -210.88) * mm, "end": v(78.76, -208.78) * mm});
            skLineSegment(sketch, "E273.MirrorCS", {"start": v(108.26, -208.78) * mm, "end": v(88.26, -208.78) * mm});
            skLineSegment(sketch, "E274.MirrorCS", {"start": v(88.26, -210.88) * mm, "end": v(88.26, -208.78) * mm});
            skLineSegment(sketch, "E275.MirrorCS", {"start": v(78.76, -210.88) * mm, "end": v(70.76, -210.88) * mm});
            skLineSegment(sketch, "E276.MirrorCS", {"start": v(78.76, -208.78) * mm, "end": v(70.76, -208.78) * mm});
            skLineSegment(sketch, "E277.MirrorCS", {"start": v(108.26, -210.88) * mm, "end": v(88.26, -210.88) * mm});
            skPoint(sketch, "E278.middle", {"position": v(118.26, -207.83) * mm});
            skLineSegment(sketch, "E279", {"start": v(108.26, -210.88) * mm, "end": v(108.26, -208.78) * mm});
            skLineSegment(sketch, "E280", {"start": v(108.26, -206.88) * mm, "end": v(108.26, -204.78) * mm});
            skSolve(sketch);
        }
        {
            var Q0;
            Q0=qCreatedBy(makeId("Top.planeOp"),FACE);
            cPlane(context, id + "F3", {"entities" : qUnion([Q0]), "cplaneType" : CPlaneType.OFFSET, "offset" : 160 * mm, "oppositeDirection" : true, "width" : 150 * mm, "height" : 150 * mm});
        }
        {
            var Q0;
            Q0=qCreatedBy(id+"F3.planeOp",FACE);
            var sketch = newSketch(context, id + "F4", { "sketchPlane" : qUnion([Q0])});
            skLineSegment(sketch, "E281.10.0", {"start": v(173.26, 47.4) * mm, "end": v(180.86, 54.06) * mm});
            skLineSegment(sketch, "E281.11.1", {"start": v(169.97, 51.16) * mm, "end": v(177.56, 57.82) * mm});
            skPoint(sketch, "E282", {"position": v(0, 0) * mm});
            skArc(sketch, "E283", {"start": v(316.37, -244.77) * mm, "mid": v(347.3, -198.46) * mm, "end": v(371.5, -148.3) * mm});
            skLineSegment(sketch, "E284.bottom", {"start": v(128.26, 221.9) * mm, "end": v(108.26, 221.9) * mm});
            skLineSegment(sketch, "E284.top", {"start": v(128.26, 201.9) * mm, "end": v(108.26, 201.9) * mm});
            skLineSegment(sketch, "E284.left", {"start": v(128.26, 221.9) * mm, "end": v(128.26, 201.9) * mm});
            skLineSegment(sketch, "E284.right", {"start": v(108.26, 221.9) * mm, "end": v(108.26, 201.9) * mm});
            skPoint(sketch, "E284.middle", {"position": v(118.26, 211.9) * mm});
            skLineSegment(sketch, "E285.bottom", {"start": v(128.26, -197.83) * mm, "end": v(108.26, -197.83) * mm});
            skLineSegment(sketch, "E285.top", {"start": v(128.26, -217.83) * mm, "end": v(108.26, -217.83) * mm});
            skLineSegment(sketch, "E285.left", {"start": v(128.26, -197.83) * mm, "end": v(128.26, -217.83) * mm});
            skLineSegment(sketch, "E285.right", {"start": v(108.26, -197.83) * mm, "end": v(108.26, -217.83) * mm});
            skPoint(sketch, "E285.middle", {"position": v(118.26, -207.83) * mm});
            skLineSegment(sketch, "E286", {"start": v(101.26, -195.83) * mm, "end": v(146.1, -195.83) * mm});
            skLineSegment(sketch, "E287", {"start": v(101.26, -195.83) * mm, "end": v(101.26, -217.83) * mm});
            skPoint(sketch, "E288", {"position": v(91.26, -207.83) * mm});
            skPoint(sketch, "E288.positionSnap0", {"position": v(108.26, -207.83) * mm});
            skCircle(sketch, "E289", {"center": v(91.26, -207.83) * mm, "radius": 1.45 * mm});
            skLineSegment(sketch, "E290", {"start": v(101.26, -217.83) * mm, "end": v(79.26, -217.83) * mm});
            skLineSegment(sketch, "E291", {"start": v(79.26, -217.83) * mm, "end": v(79.26, 221.9) * mm});
            skPoint(sketch, "E292", {"position": v(91.26, 211.9) * mm});
            skPoint(sketch, "E292.positionSnap0", {"position": v(108.26, 211.9) * mm});
            skLineSegment(sketch, "E293", {"start": v(79.26, 221.9) * mm, "end": v(101.26, 221.9) * mm});
            skLineSegment(sketch, "E294", {"start": v(101.26, 221.9) * mm, "end": v(101.26, 199.9) * mm});
            skLineSegment(sketch, "E295", {"start": v(101.26, 199.9) * mm, "end": v(156.69, 199.9) * mm});
            skLineSegment(sketch, "E296", {"start": v(263.33, -265.58) * mm, "end": v(271.78, -265.58) * mm});
            skLineSegment(sketch, "E297", {"start": v(156.69, 199.9) * mm, "end": v(210.4, 316.43) * mm});
            skLineSegment(sketch, "E298.trimOffspring", {"start": v(146.1, -195.83) * mm, "end": v(263.33, -265.58) * mm});
            skLineSegment(sketch, "E299", {"start": v(237.7, 110.57) * mm, "end": v(241, 106.8) * mm});
            skLineSegment(sketch, "E300", {"start": v(169.97, 51.16) * mm, "end": v(173.26, 47.4) * mm});
            skLineSegment(sketch, "E301", {"start": v(177.56, 57.82) * mm, "end": v(180.86, 54.06) * mm});
            skLineSegment(sketch, "E302", {"start": v(230.11, 103.9) * mm, "end": v(233.41, 100.15) * mm});
            skLineSegment(sketch, "E303.trimOffspring", {"start": v(233.41, 100.15) * mm, "end": v(241, 106.8) * mm});
            skLineSegment(sketch, "E304.trimOffspring", {"start": v(230.11, 103.9) * mm, "end": v(237.7, 110.57) * mm});
            skLineSegment(sketch, "E305.10.0", {"start": v(131.68, 121.77) * mm, "end": v(135.9, 130.94) * mm});
            skLineSegment(sketch, "E305.11.1", {"start": v(127.14, 123.86) * mm, "end": v(131.37, 133.04) * mm});
            skLineSegment(sketch, "E306", {"start": v(164.86, 205.69) * mm, "end": v(169.4, 203.6) * mm});
            skLineSegment(sketch, "E307", {"start": v(127.14, 123.86) * mm, "end": v(131.68, 121.77) * mm});
            skLineSegment(sketch, "E308", {"start": v(131.37, 133.04) * mm, "end": v(135.9, 130.94) * mm});
            skLineSegment(sketch, "E309", {"start": v(160.63, 196.52) * mm, "end": v(165.17, 194.42) * mm});
            skLineSegment(sketch, "E310.trimOffspring", {"start": v(165.17, 194.42) * mm, "end": v(169.4, 203.6) * mm});
            skLineSegment(sketch, "E311.trimOffspring", {"start": v(160.63, 196.52) * mm, "end": v(164.86, 205.69) * mm});
            skLineSegment(sketch, "E312.10.0", {"start": v(177.56, -27.17) * mm, "end": v(187.21, -24.17) * mm});
            skLineSegment(sketch, "E312.11.1", {"start": v(176.08, -22.4) * mm, "end": v(185.73, -19.4) * mm});
            skLineSegment(sketch, "E313", {"start": v(262.13, 4.32) * mm, "end": v(263.61, -0.45) * mm});
            skLineSegment(sketch, "E314", {"start": v(176.08, -22.4) * mm, "end": v(177.56, -27.17) * mm});
            skLineSegment(sketch, "E315", {"start": v(185.73, -19.4) * mm, "end": v(187.21, -24.17) * mm});
            skLineSegment(sketch, "E316", {"start": v(252.48, 1.33) * mm, "end": v(253.97, -3.45) * mm});
            skLineSegment(sketch, "E317.trimOffspring", {"start": v(253.97, -3.45) * mm, "end": v(263.61, -0.45) * mm});
            skLineSegment(sketch, "E318.trimOffspring", {"start": v(252.48, 1.33) * mm, "end": v(262.13, 4.32) * mm});
            skLineSegment(sketch, "E319.10.0", {"start": v(151.16, -97.04) * mm, "end": v(161.2, -98.23) * mm});
            skLineSegment(sketch, "E319.11.1", {"start": v(151.75, -92.08) * mm, "end": v(161.78, -93.26) * mm});
            skLineSegment(sketch, "E320", {"start": v(241.23, -102.67) * mm, "end": v(240.64, -107.63) * mm});
            skLineSegment(sketch, "E321", {"start": v(151.75, -92.08) * mm, "end": v(151.16, -97.04) * mm});
            skLineSegment(sketch, "E322", {"start": v(161.78, -93.26) * mm, "end": v(161.2, -98.23) * mm});
            skLineSegment(sketch, "E323", {"start": v(231.2, -101.48) * mm, "end": v(230.6, -106.45) * mm});
            skLineSegment(sketch, "E324.trimOffspring", {"start": v(230.6, -106.45) * mm, "end": v(240.64, -107.63) * mm});
            skLineSegment(sketch, "E325.trimOffspring", {"start": v(231.2, -101.48) * mm, "end": v(241.23, -102.67) * mm});
            skLineSegment(sketch, "E326.bottom", {"start": v(660.02, -36.45) * mm, "end": v(750.02, -36.45) * mm});
            skLineSegment(sketch, "E326.top", {"start": v(670.02, -86.45) * mm, "end": v(740.02, -86.45) * mm});
            skLineSegment(sketch, "E326.left", {"start": v(660.02, -36.45) * mm, "end": v(660.02, -86.45) * mm});
            skLineSegment(sketch, "E326.right", {"start": v(750.02, -36.45) * mm, "end": v(750.02, -86.45) * mm});
            skLineSegment(sketch, "E327", {"start": v(660.02, -86.45) * mm, "end": v(660.02, -91.45) * mm});
            skLineSegment(sketch, "E328", {"start": v(660.02, -91.45) * mm, "end": v(670.02, -91.45) * mm});
            skLineSegment(sketch, "E329", {"start": v(670.02, -91.45) * mm, "end": v(670.02, -86.45) * mm});
            skLineSegment(sketch, "E330", {"start": v(750.02, -86.45) * mm, "end": v(750.02, -91.45) * mm});
            skLineSegment(sketch, "E331", {"start": v(750.02, -91.45) * mm, "end": v(740.02, -91.45) * mm});
            skLineSegment(sketch, "E332", {"start": v(740.02, -91.45) * mm, "end": v(740.02, -86.45) * mm});
            skLineSegment(sketch, "E333.10.0", {"start": v(89.26, -156.2) * mm, "end": v(97.94, -161.37) * mm});
            skLineSegment(sketch, "E333.11.1", {"start": v(91.82, -151.9) * mm, "end": v(100.5, -157.07) * mm});
            skLineSegment(sketch, "E334", {"start": v(169.25, -197.97) * mm, "end": v(166.7, -202.27) * mm});
            skLineSegment(sketch, "E335", {"start": v(91.82, -151.9) * mm, "end": v(89.26, -156.2) * mm});
            skLineSegment(sketch, "E336", {"start": v(100.5, -157.07) * mm, "end": v(97.94, -161.37) * mm});
            skLineSegment(sketch, "E337", {"start": v(160.57, -192.8) * mm, "end": v(158.02, -197.1) * mm});
            skLineSegment(sketch, "E338.trimOffspring", {"start": v(158.02, -197.1) * mm, "end": v(166.7, -202.27) * mm});
            skLineSegment(sketch, "E339.trimOffspring", {"start": v(160.57, -192.8) * mm, "end": v(169.25, -197.97) * mm});
            skArc(sketch, "E340", {"start": v(247.15, 288.65) * mm, "mid": v(-378.14, -37.51) * mm, "end": v(299.04, -234.46) * mm});
            skLineSegment(sketch, "E341", {"start": v(247.15, 288.65) * mm, "end": v(255.84, 307.49) * mm});
            skLineSegment(sketch, "E342", {"start": v(315.4, 211.95) * mm, "end": v(330.55, 225.24) * mm});
            skLineSegment(sketch, "E343.1.0", {"start": v(343.19, 163.17) * mm, "end": v(358.78, 176.85) * mm});
            skLineSegment(sketch, "E343.1.1", {"start": v(374.34, 65.34) * mm, "end": v(393.6, 71.32) * mm});
            skLineSegment(sketch, "E343.2.0", {"start": v(379.88, 9.47) * mm, "end": v(399.7, 15.63) * mm});
            skLineSegment(sketch, "E343.2.1", {"start": v(368.55, -92.56) * mm, "end": v(388.57, -94.93) * mm});
            skLineSegment(sketch, "E343.3.0", {"start": v(350.9, -145.86) * mm, "end": v(371.5, -148.3) * mm});
            skLineSegment(sketch, "E343.3.1", {"start": v(299.04, -234.46) * mm, "end": v(316.37, -244.77) * mm});
            skLineSegment(sketch, "E343.anchor1", {"start": v(0, 0) * mm, "end": v(315.4, 211.95) * mm, "construction": true});
            skLineSegment(sketch, "E343.anchor2", {"start": v(0, 0) * mm, "end": v(299.04, -234.46) * mm, "construction": true});
            skArc(sketch, "E344.trimOffspring", {"start": v(330.55, 225.24) * mm, "mid": v(296.06, 268.97) * mm, "end": v(255.84, 307.49) * mm});
            skArc(sketch, "E345.trimOffspring", {"start": v(393.6, 71.32) * mm, "mid": v(379.87, 125.3) * mm, "end": v(358.78, 176.85) * mm});
            skArc(sketch, "E346.trimOffspring", {"start": v(388.57, -94.93) * mm, "mid": v(398, -40.04) * mm, "end": v(399.7, 15.63) * mm});
            skArc(sketch, "E347.trimOffspring", {"start": v(343.19, 163.17) * mm, "mid": v(330.2, 188.07) * mm, "end": v(315.4, 211.95) * mm});
            skArc(sketch, "E348.trimOffspring", {"start": v(379.88, 9.47) * mm, "mid": v(378.14, 37.51) * mm, "end": v(374.34, 65.34) * mm});
            skArc(sketch, "E349.trimOffspring", {"start": v(350.9, -145.86) * mm, "mid": v(360.7, -119.54) * mm, "end": v(368.55, -92.56) * mm});
            skSolve(sketch);
        }
        {
            var Q0;
            Q0=makeQuery(id+"F4.imprint","IMPRINT",FACE,{"disambiguationData":[TD([[makeQuery(id+"F4.imprint","IMPRINT",EDGE,{"derivedFrom":sQuery(id+"F4.wireOp",EDGE,"E284.bottom")}),1.0]])]});
            var Q1;
            Q1=makeQuery(id+"F4.imprint","IMPRINT",FACE,{"disambiguationData":[TD([[makeQuery(id+"F4.imprint","IMPRINT",EDGE,{"derivedFrom":sQuery(id+"F4.wireOp",EDGE,"E285.bottom")}),1.0]])]});
            var Q2;
            Q2=makeQuery(id+"F4.imprint","IMPRINT",FACE,{"disambiguationData":[TD([[makeQuery(id+"F4.imprint","IMPRINT",EDGE,{"derivedFrom":sQuery(id+"F4.wireOp",EDGE,"E281.10.0")}),-1.0]])]});
            extrude(context, id + "F5", {"entities" : qUnion([Q0, Q1, Q2]), "oppositeDirection" : true, "depth" : 3 * mm});
        }
        {
            var Q0;
            {var subQ0=sQuery(id+"F4.wireOp",EDGE,"0fee2d9d-80bf-450c-bdaf-01117a341cef");var subQ1=sQuery(id+"F4.wireOp",EDGE,"E281.8.0");var subQ2=makeQuery(id+"F4.imprint","INTERSECT",VERTEX,{"derivedFrom":[subQ1,subQ0]});Q0=makeQuery(id+"F4.imprint","IMPRINT",FACE,{"disambiguationData":[TD([[makeQuery(id+"F4.imprint","IMPRINT",EDGE,{"disambiguationData":[TD([[subQ2,1.0]])],"derivedFrom":subQ1}),-1.0]])]});}
            var Q1;
            {var subQ0=sQuery(id+"F4.wireOp",EDGE,"0fee2d9d-80bf-450c-bdaf-01117a341cef");var subQ1=sQuery(id+"F4.wireOp",EDGE,"E281.9.0");var subQ2=makeQuery(id+"F4.imprint","INTERSECT",VERTEX,{"derivedFrom":[subQ1,subQ0]});Q1=makeQuery(id+"F4.imprint","IMPRINT",FACE,{"disambiguationData":[TD([[makeQuery(id+"F4.imprint","IMPRINT",EDGE,{"disambiguationData":[TD([[subQ2,1.0]])],"derivedFrom":subQ1}),-1.0]])]});}
            var Q2;
            {var subQ0=sQuery(id+"F4.wireOp",EDGE,"0fee2d9d-80bf-450c-bdaf-01117a341cef");var subQ1=sQuery(id+"F4.wireOp",EDGE,"E281.10.0");var subQ2=makeQuery(id+"F4.imprint","INTERSECT",VERTEX,{"derivedFrom":[subQ1,subQ0]});Q2=makeQuery(id+"F4.imprint","IMPRINT",FACE,{"disambiguationData":[TD([[makeQuery(id+"F4.imprint","IMPRINT",EDGE,{"disambiguationData":[TD([[subQ2,1.0]])],"derivedFrom":subQ1}),-1.0]])]});}
            var Q3;
            {var subQ0=sQuery(id+"F4.wireOp",EDGE,"0fee2d9d-80bf-450c-bdaf-01117a341cef");var subQ5=sQuery(id+"F4.wireOp",EDGE,"E281.11.1");var subQ7=makeQuery(id+"F4.imprint","INTERSECT",VERTEX,{"derivedFrom":[subQ5,subQ0]});Q3=makeQuery(id+"F4.imprint","IMPRINT",FACE,{"disambiguationData":[TD([[makeQuery(id+"F4.imprint","IMPRINT",EDGE,{"disambiguationData":[TD([[subQ7,1.0]])],"derivedFrom":subQ5}),1.0]])]});}
            extrude(context, id + "F6", {"entities" : qUnion([Q0, Q1, Q2, Q3]), "operationType" : NewBodyOperationType.REMOVE, "oppositeDirection" : true, "depth" : 35 * mm});
        }
        {
            var Q0;
            Q0=makeQuery(id+"F2.imprint","IMPRINT",FACE,{"disambiguationData":[TD([[makeQuery(id+"F2.imprint","IMPRINT",EDGE,{"derivedFrom":sQuery(id+"F2.wireOp",EDGE,"E44.2.1")}),-1.0]])]});
            var Q1;
            Q1=makeQuery(id+"F2.imprint","IMPRINT",FACE,{"disambiguationData":[TD([[makeQuery(id+"F2.imprint","IMPRINT",EDGE,{"derivedFrom":sQuery(id+"F2.wireOp",EDGE,"e8fc542b-362e-4a05-8d7d-844c32473c59.0")}),1.0]])]});
            var Q2;
            Q2=makeQuery(id+"F2.imprint","IMPRINT",FACE,{"disambiguationData":[TD([[makeQuery(id+"F2.imprint","IMPRINT",EDGE,{"derivedFrom":sQuery(id+"F2.wireOp",EDGE,"E45")}),-1.0]])]});
            var Q3;
            Q3=makeQuery(id+"F2.imprint","IMPRINT",FACE,{"disambiguationData":[TD([[makeQuery(id+"F2.imprint","IMPRINT",EDGE,{"derivedFrom":sQuery(id+"F2.wireOp",EDGE,"E51.bottom")}),1.0]])]});
            extrude(context, id + "F7", {"entities" : qUnion([Q0, Q1, Q2, Q3]), "depth" : 5 * mm});
        }
        {
            var Q0;
            Q0=qCreatedBy(id+"F1.planeOp",FACE);
            var sketch = newSketch(context, id + "F8", { "sketchPlane" : qUnion([Q0])});
            skLineSegment(sketch, "E350.bottom", {"start": v(-238.54, -6.75) * mm, "end": v(-258.54, -6.75) * mm});
            skLineSegment(sketch, "E350.top", {"start": v(-238.54, -26.75) * mm, "end": v(-258.54, -26.75) * mm});
            skLineSegment(sketch, "E350.left", {"start": v(-238.54, -6.75) * mm, "end": v(-238.54, -26.75) * mm});
            skLineSegment(sketch, "E350.right", {"start": v(-258.54, -6.75) * mm, "end": v(-258.54, -26.75) * mm});
            skPoint(sketch, "E350.middle", {"position": v(-248.54, -16.75) * mm});
            skLineSegment(sketch, "E351.bottom", {"start": v(128.26, 221.9) * mm, "end": v(108.26, 221.9) * mm});
            skLineSegment(sketch, "E351.top", {"start": v(128.26, 201.9) * mm, "end": v(108.26, 201.9) * mm});
            skLineSegment(sketch, "E351.left", {"start": v(128.26, 221.9) * mm, "end": v(128.26, 201.9) * mm});
            skLineSegment(sketch, "E351.right", {"start": v(108.26, 221.9) * mm, "end": v(108.26, 201.9) * mm});
            skPoint(sketch, "E351.middle", {"position": v(118.26, 211.9) * mm});
            skLineSegment(sketch, "E352.bottom", {"start": v(128.26, -197.83) * mm, "end": v(108.26, -197.83) * mm});
            skLineSegment(sketch, "E352.top", {"start": v(128.26, -217.83) * mm, "end": v(108.26, -217.83) * mm});
            skLineSegment(sketch, "E352.left", {"start": v(128.26, -197.83) * mm, "end": v(128.26, -217.83) * mm});
            skLineSegment(sketch, "E352.right", {"start": v(108.26, -197.83) * mm, "end": v(108.26, -217.83) * mm});
            skPoint(sketch, "E352.middle", {"position": v(118.26, -207.83) * mm});
            skPoint(sketch, "E353", {"position": v(0, 0) * mm});
            skSolve(sketch);
        }
        {
            var Q0;
            Q0 = qSketchRegion(id + "F8", true);
            extrude(context, id + "F9", {"entities" : qUnion([Q0]), "operationType" : NewBodyOperationType.ADD, "oppositeDirection" : true, "depth" : 800 * mm});
        }
        {
            var Q0;
            Q0=makeQuery(id+"F0.imprint","IMPRINT",FACE,{"disambiguationData":[TD([[makeQuery(id+"F0.imprint","IMPRINT",EDGE,{"derivedFrom":sQuery(id+"F0.wireOp",EDGE,"E1")}),1.0]])]});
            var Q1;
            {var subQ0=sQuery(id+"F0.wireOp",EDGE,"E33.1.12");Q1=makeQuery(id+"F0.imprint","IMPRINT",FACE,{"disambiguationData":[TD([[makeQuery(id+"F0.imprint","IMPRINT",EDGE,{"derivedFrom":subQ0}),-1.0]])]});}
            var Q2;
            {var subQ0=sQuery(id+"F0.wireOp",EDGE,"E33.2.12");Q2=makeQuery(id+"F0.imprint","IMPRINT",FACE,{"disambiguationData":[TD([[makeQuery(id+"F0.imprint","IMPRINT",EDGE,{"derivedFrom":subQ0}),-1.0]])]});}
            var Q3;
            {var subQ0=sQuery(id+"F0.wireOp",EDGE,"E33.3.12");Q3=makeQuery(id+"F0.imprint","IMPRINT",FACE,{"disambiguationData":[TD([[makeQuery(id+"F0.imprint","IMPRINT",EDGE,{"derivedFrom":subQ0}),-1.0]])]});}
            var Q4;
            {var subQ0=sQuery(id+"F0.wireOp",EDGE,"E33.4.12");Q4=makeQuery(id+"F0.imprint","IMPRINT",FACE,{"disambiguationData":[TD([[makeQuery(id+"F0.imprint","IMPRINT",EDGE,{"derivedFrom":subQ0}),-1.0]])]});}
            var Q5;
            {var subQ0=sQuery(id+"F0.wireOp",EDGE,"E33.5.12");Q5=makeQuery(id+"F0.imprint","IMPRINT",FACE,{"disambiguationData":[TD([[makeQuery(id+"F0.imprint","IMPRINT",EDGE,{"derivedFrom":subQ0}),-1.0]])]});}
            var Q6;
            {var subQ0=sQuery(id+"F0.wireOp",EDGE,"E25.6.15");Q6=makeQuery(id+"F0.imprint","IMPRINT",FACE,{"disambiguationData":[TD([[makeQuery(id+"F0.imprint","IMPRINT",EDGE,{"derivedFrom":subQ0}),1.0]])]});}
            var Q7;
            {var subQ0=sQuery(id+"F0.wireOp",EDGE,"E33.7.12");Q7=makeQuery(id+"F0.imprint","IMPRINT",FACE,{"disambiguationData":[TD([[makeQuery(id+"F0.imprint","IMPRINT",EDGE,{"derivedFrom":subQ0}),-1.0]])]});}
            var Q8;
            {var subQ0=sQuery(id+"F0.wireOp",EDGE,"E33.8.12");Q8=makeQuery(id+"F0.imprint","IMPRINT",FACE,{"disambiguationData":[TD([[makeQuery(id+"F0.imprint","IMPRINT",EDGE,{"derivedFrom":subQ0}),-1.0]])]});}
            var Q9;
            {var subQ0=sQuery(id+"F0.wireOp",EDGE,"E25.9.15");Q9=makeQuery(id+"F0.imprint","IMPRINT",FACE,{"disambiguationData":[TD([[makeQuery(id+"F0.imprint","IMPRINT",EDGE,{"derivedFrom":subQ0}),1.0]])]});}
            var Q10;
            {var subQ0=sQuery(id+"F0.wireOp",EDGE,"E33.10.12");Q10=makeQuery(id+"F0.imprint","IMPRINT",FACE,{"disambiguationData":[TD([[makeQuery(id+"F0.imprint","IMPRINT",EDGE,{"derivedFrom":subQ0}),-1.0]])]});}
            var Q11;
            {var subQ0=sQuery(id+"F0.wireOp",EDGE,"E33.11.12");Q11=makeQuery(id+"F0.imprint","IMPRINT",FACE,{"disambiguationData":[TD([[makeQuery(id+"F0.imprint","IMPRINT",EDGE,{"derivedFrom":subQ0}),-1.0]])]});}
            var Q12;
            {var subQ0=sQuery(id+"F0.wireOp",EDGE,"E25.12.15");Q12=makeQuery(id+"F0.imprint","IMPRINT",FACE,{"disambiguationData":[TD([[makeQuery(id+"F0.imprint","IMPRINT",EDGE,{"derivedFrom":subQ0}),1.0]])]});}
            var Q13;
            {var subQ0=sQuery(id+"F0.wireOp",EDGE,"E25.13.15");Q13=makeQuery(id+"F0.imprint","IMPRINT",FACE,{"disambiguationData":[TD([[makeQuery(id+"F0.imprint","IMPRINT",EDGE,{"derivedFrom":subQ0}),1.0]])]});}
            var Q14;
            {var subQ0=sQuery(id+"F0.wireOp",EDGE,"E33.14.12");Q14=makeQuery(id+"F0.imprint","IMPRINT",FACE,{"disambiguationData":[TD([[makeQuery(id+"F0.imprint","IMPRINT",EDGE,{"derivedFrom":subQ0}),-1.0]])]});}
            var Q15;
            {var subQ0=sQuery(id+"F0.wireOp",EDGE,"E17.left");Q15=makeQuery(id+"F0.imprint","IMPRINT",FACE,{"disambiguationData":[TD([[makeQuery(id+"F0.imprint","IMPRINT",EDGE,{"derivedFrom":subQ0}),1.0]])]});}
            var Q16;
            {var subQ0=sQuery(id+"F0.wireOp",EDGE,"E17.right");Q16=makeQuery(id+"F0.imprint","IMPRINT",FACE,{"disambiguationData":[TD([[makeQuery(id+"F0.imprint","IMPRINT",EDGE,{"derivedFrom":subQ0}),1.0]])]});}
            var Q17;
            {var subQ0=sQuery(id+"F0.wireOp",EDGE,"E25.1.16");Q17=makeQuery(id+"F0.imprint","IMPRINT",FACE,{"disambiguationData":[TD([[makeQuery(id+"F0.imprint","IMPRINT",EDGE,{"derivedFrom":subQ0}),1.0]])]});}
            var Q18;
            {var subQ0=sQuery(id+"F0.wireOp",EDGE,"E25.1.17");Q18=makeQuery(id+"F0.imprint","IMPRINT",FACE,{"disambiguationData":[TD([[makeQuery(id+"F0.imprint","IMPRINT",EDGE,{"derivedFrom":subQ0}),1.0]])]});}
            var Q19;
            {var subQ0=sQuery(id+"F0.wireOp",EDGE,"E25.2.16");Q19=makeQuery(id+"F0.imprint","IMPRINT",FACE,{"disambiguationData":[TD([[makeQuery(id+"F0.imprint","IMPRINT",EDGE,{"derivedFrom":subQ0}),1.0]])]});}
            var Q20;
            {var subQ0=sQuery(id+"F0.wireOp",EDGE,"E25.2.17");Q20=makeQuery(id+"F0.imprint","IMPRINT",FACE,{"disambiguationData":[TD([[makeQuery(id+"F0.imprint","IMPRINT",EDGE,{"derivedFrom":subQ0}),1.0]])]});}
            var Q21;
            {var subQ0=sQuery(id+"F0.wireOp",EDGE,"E25.3.16");Q21=makeQuery(id+"F0.imprint","IMPRINT",FACE,{"disambiguationData":[TD([[makeQuery(id+"F0.imprint","IMPRINT",EDGE,{"derivedFrom":subQ0}),1.0]])]});}
            var Q22;
            {var subQ0=sQuery(id+"F0.wireOp",EDGE,"E25.3.17");Q22=makeQuery(id+"F0.imprint","IMPRINT",FACE,{"disambiguationData":[TD([[makeQuery(id+"F0.imprint","IMPRINT",EDGE,{"derivedFrom":subQ0}),1.0]])]});}
            var Q23;
            {var subQ0=sQuery(id+"F0.wireOp",EDGE,"E25.4.16");Q23=makeQuery(id+"F0.imprint","IMPRINT",FACE,{"disambiguationData":[TD([[makeQuery(id+"F0.imprint","IMPRINT",EDGE,{"derivedFrom":subQ0}),1.0]])]});}
            var Q24;
            {var subQ0=sQuery(id+"F0.wireOp",EDGE,"E25.4.17");Q24=makeQuery(id+"F0.imprint","IMPRINT",FACE,{"disambiguationData":[TD([[makeQuery(id+"F0.imprint","IMPRINT",EDGE,{"derivedFrom":subQ0}),1.0]])]});}
            var Q25;
            {var subQ0=sQuery(id+"F0.wireOp",EDGE,"E25.5.16");Q25=makeQuery(id+"F0.imprint","IMPRINT",FACE,{"disambiguationData":[TD([[makeQuery(id+"F0.imprint","IMPRINT",EDGE,{"derivedFrom":subQ0}),1.0]])]});}
            var Q26;
            {var subQ0=sQuery(id+"F0.wireOp",EDGE,"E25.5.17");Q26=makeQuery(id+"F0.imprint","IMPRINT",FACE,{"disambiguationData":[TD([[makeQuery(id+"F0.imprint","IMPRINT",EDGE,{"derivedFrom":subQ0}),1.0]])]});}
            var Q27;
            {var subQ0=sQuery(id+"F0.wireOp",EDGE,"E25.6.16");Q27=makeQuery(id+"F0.imprint","IMPRINT",FACE,{"disambiguationData":[TD([[makeQuery(id+"F0.imprint","IMPRINT",EDGE,{"derivedFrom":subQ0}),1.0]])]});}
            var Q28;
            {var subQ0=sQuery(id+"F0.wireOp",EDGE,"E25.6.17");Q28=makeQuery(id+"F0.imprint","IMPRINT",FACE,{"disambiguationData":[TD([[makeQuery(id+"F0.imprint","IMPRINT",EDGE,{"derivedFrom":subQ0}),1.0]])]});}
            var Q29;
            {var subQ0=sQuery(id+"F0.wireOp",EDGE,"E25.7.16");Q29=makeQuery(id+"F0.imprint","IMPRINT",FACE,{"disambiguationData":[TD([[makeQuery(id+"F0.imprint","IMPRINT",EDGE,{"derivedFrom":subQ0}),1.0]])]});}
            var Q30;
            {var subQ0=sQuery(id+"F0.wireOp",EDGE,"E25.7.17");Q30=makeQuery(id+"F0.imprint","IMPRINT",FACE,{"disambiguationData":[TD([[makeQuery(id+"F0.imprint","IMPRINT",EDGE,{"derivedFrom":subQ0}),1.0]])]});}
            var Q31;
            {var subQ0=sQuery(id+"F0.wireOp",EDGE,"E25.8.16");Q31=makeQuery(id+"F0.imprint","IMPRINT",FACE,{"disambiguationData":[TD([[makeQuery(id+"F0.imprint","IMPRINT",EDGE,{"derivedFrom":subQ0}),1.0]])]});}
            var Q32;
            {var subQ0=sQuery(id+"F0.wireOp",EDGE,"E25.8.17");Q32=makeQuery(id+"F0.imprint","IMPRINT",FACE,{"disambiguationData":[TD([[makeQuery(id+"F0.imprint","IMPRINT",EDGE,{"derivedFrom":subQ0}),1.0]])]});}
            var Q33;
            {var subQ0=sQuery(id+"F0.wireOp",EDGE,"E25.9.16");Q33=makeQuery(id+"F0.imprint","IMPRINT",FACE,{"disambiguationData":[TD([[makeQuery(id+"F0.imprint","IMPRINT",EDGE,{"derivedFrom":subQ0}),1.0]])]});}
            var Q34;
            {var subQ0=sQuery(id+"F0.wireOp",EDGE,"E25.9.17");Q34=makeQuery(id+"F0.imprint","IMPRINT",FACE,{"disambiguationData":[TD([[makeQuery(id+"F0.imprint","IMPRINT",EDGE,{"derivedFrom":subQ0}),1.0]])]});}
            var Q35;
            {var subQ0=sQuery(id+"F0.wireOp",EDGE,"E25.10.16");Q35=makeQuery(id+"F0.imprint","IMPRINT",FACE,{"disambiguationData":[TD([[makeQuery(id+"F0.imprint","IMPRINT",EDGE,{"derivedFrom":subQ0}),1.0]])]});}
            var Q36;
            {var subQ0=sQuery(id+"F0.wireOp",EDGE,"E25.10.17");Q36=makeQuery(id+"F0.imprint","IMPRINT",FACE,{"disambiguationData":[TD([[makeQuery(id+"F0.imprint","IMPRINT",EDGE,{"derivedFrom":subQ0}),1.0]])]});}
            var Q37;
            {var subQ0=sQuery(id+"F0.wireOp",EDGE,"E25.11.16");Q37=makeQuery(id+"F0.imprint","IMPRINT",FACE,{"disambiguationData":[TD([[makeQuery(id+"F0.imprint","IMPRINT",EDGE,{"derivedFrom":subQ0}),1.0]])]});}
            var Q38;
            {var subQ0=sQuery(id+"F0.wireOp",EDGE,"E25.11.17");Q38=makeQuery(id+"F0.imprint","IMPRINT",FACE,{"disambiguationData":[TD([[makeQuery(id+"F0.imprint","IMPRINT",EDGE,{"derivedFrom":subQ0}),1.0]])]});}
            var Q39;
            {var subQ0=sQuery(id+"F0.wireOp",EDGE,"E25.12.16");Q39=makeQuery(id+"F0.imprint","IMPRINT",FACE,{"disambiguationData":[TD([[makeQuery(id+"F0.imprint","IMPRINT",EDGE,{"derivedFrom":subQ0}),1.0]])]});}
            var Q40;
            {var subQ0=sQuery(id+"F0.wireOp",EDGE,"E25.12.17");Q40=makeQuery(id+"F0.imprint","IMPRINT",FACE,{"disambiguationData":[TD([[makeQuery(id+"F0.imprint","IMPRINT",EDGE,{"derivedFrom":subQ0}),1.0]])]});}
            var Q41;
            {var subQ0=sQuery(id+"F0.wireOp",EDGE,"E25.13.16");Q41=makeQuery(id+"F0.imprint","IMPRINT",FACE,{"disambiguationData":[TD([[makeQuery(id+"F0.imprint","IMPRINT",EDGE,{"derivedFrom":subQ0}),1.0]])]});}
            var Q42;
            {var subQ0=sQuery(id+"F0.wireOp",EDGE,"E25.13.17");Q42=makeQuery(id+"F0.imprint","IMPRINT",FACE,{"disambiguationData":[TD([[makeQuery(id+"F0.imprint","IMPRINT",EDGE,{"derivedFrom":subQ0}),1.0]])]});}
            var Q43;
            {var subQ0=sQuery(id+"F0.wireOp",EDGE,"E25.14.16");Q43=makeQuery(id+"F0.imprint","IMPRINT",FACE,{"disambiguationData":[TD([[makeQuery(id+"F0.imprint","IMPRINT",EDGE,{"derivedFrom":subQ0}),1.0]])]});}
            var Q44;
            {var subQ0=sQuery(id+"F0.wireOp",EDGE,"E25.14.17");Q44=makeQuery(id+"F0.imprint","IMPRINT",FACE,{"disambiguationData":[TD([[makeQuery(id+"F0.imprint","IMPRINT",EDGE,{"derivedFrom":subQ0}),1.0]])]});}
            var Q45;
            {var subQ0=sQuery(id+"F0.wireOp",EDGE,"E11.left");Q45=makeQuery(id+"F0.imprint","IMPRINT",FACE,{"disambiguationData":[TD([[makeQuery(id+"F0.imprint","IMPRINT",EDGE,{"derivedFrom":subQ0}),1.0]])]});}
            var Q46;
            Q46=makeQuery(id+"F0.imprint","IMPRINT",FACE,{"disambiguationData":[TD([[makeQuery(id+"F0.imprint","IMPRINT",EDGE,{"derivedFrom":sQuery(id+"F0.wireOp",EDGE,"E12")}),-1.0]])]});
            var Q47;
            Q47=makeQuery(id+"F0.imprint","IMPRINT",FACE,{"disambiguationData":[TD([[makeQuery(id+"F0.imprint","IMPRINT",EDGE,{"derivedFrom":sQuery(id+"F0.wireOp",EDGE,"E25.1.0")}),-1.0]])]});
            var Q48;
            Q48=makeQuery(id+"F0.imprint","IMPRINT",FACE,{"disambiguationData":[TD([[makeQuery(id+"F0.imprint","IMPRINT",EDGE,{"derivedFrom":sQuery(id+"F0.wireOp",EDGE,"E25.1.4")}),-1.0]])]});
            var Q49;
            Q49=makeQuery(id+"F0.imprint","IMPRINT",FACE,{"disambiguationData":[TD([[makeQuery(id+"F0.imprint","IMPRINT",EDGE,{"derivedFrom":sQuery(id+"F0.wireOp",EDGE,"E25.2.0")}),-1.0]])]});
            var Q50;
            Q50=makeQuery(id+"F0.imprint","IMPRINT",FACE,{"disambiguationData":[TD([[makeQuery(id+"F0.imprint","IMPRINT",EDGE,{"derivedFrom":sQuery(id+"F0.wireOp",EDGE,"E25.2.4")}),-1.0]])]});
            var Q51;
            Q51=makeQuery(id+"F0.imprint","IMPRINT",FACE,{"disambiguationData":[TD([[makeQuery(id+"F0.imprint","IMPRINT",EDGE,{"derivedFrom":sQuery(id+"F0.wireOp",EDGE,"E25.3.0")}),-1.0]])]});
            var Q52;
            Q52=makeQuery(id+"F0.imprint","IMPRINT",FACE,{"disambiguationData":[TD([[makeQuery(id+"F0.imprint","IMPRINT",EDGE,{"derivedFrom":sQuery(id+"F0.wireOp",EDGE,"E25.3.4")}),-1.0]])]});
            var Q53;
            Q53=makeQuery(id+"F0.imprint","IMPRINT",FACE,{"disambiguationData":[TD([[makeQuery(id+"F0.imprint","IMPRINT",EDGE,{"derivedFrom":sQuery(id+"F0.wireOp",EDGE,"E25.4.0")}),-1.0]])]});
            var Q54;
            Q54=makeQuery(id+"F0.imprint","IMPRINT",FACE,{"disambiguationData":[TD([[makeQuery(id+"F0.imprint","IMPRINT",EDGE,{"derivedFrom":sQuery(id+"F0.wireOp",EDGE,"E25.4.4")}),-1.0]])]});
            var Q55;
            Q55=makeQuery(id+"F0.imprint","IMPRINT",FACE,{"disambiguationData":[TD([[makeQuery(id+"F0.imprint","IMPRINT",EDGE,{"derivedFrom":sQuery(id+"F0.wireOp",EDGE,"E25.5.0")}),-1.0]])]});
            var Q56;
            Q56=makeQuery(id+"F0.imprint","IMPRINT",FACE,{"disambiguationData":[TD([[makeQuery(id+"F0.imprint","IMPRINT",EDGE,{"derivedFrom":sQuery(id+"F0.wireOp",EDGE,"E25.5.4")}),-1.0]])]});
            var Q57;
            Q57=makeQuery(id+"F0.imprint","IMPRINT",FACE,{"disambiguationData":[TD([[makeQuery(id+"F0.imprint","IMPRINT",EDGE,{"derivedFrom":sQuery(id+"F0.wireOp",EDGE,"E25.6.0")}),-1.0]])]});
            var Q58;
            Q58=makeQuery(id+"F0.imprint","IMPRINT",FACE,{"disambiguationData":[TD([[makeQuery(id+"F0.imprint","IMPRINT",EDGE,{"derivedFrom":sQuery(id+"F0.wireOp",EDGE,"E25.6.4")}),-1.0]])]});
            var Q59;
            Q59=makeQuery(id+"F0.imprint","IMPRINT",FACE,{"disambiguationData":[TD([[makeQuery(id+"F0.imprint","IMPRINT",EDGE,{"derivedFrom":sQuery(id+"F0.wireOp",EDGE,"E25.7.0")}),-1.0]])]});
            var Q60;
            Q60=makeQuery(id+"F0.imprint","IMPRINT",FACE,{"disambiguationData":[TD([[makeQuery(id+"F0.imprint","IMPRINT",EDGE,{"derivedFrom":sQuery(id+"F0.wireOp",EDGE,"E25.7.4")}),-1.0]])]});
            var Q61;
            Q61=makeQuery(id+"F0.imprint","IMPRINT",FACE,{"disambiguationData":[TD([[makeQuery(id+"F0.imprint","IMPRINT",EDGE,{"derivedFrom":sQuery(id+"F0.wireOp",EDGE,"E25.8.0")}),-1.0]])]});
            var Q62;
            Q62=makeQuery(id+"F0.imprint","IMPRINT",FACE,{"disambiguationData":[TD([[makeQuery(id+"F0.imprint","IMPRINT",EDGE,{"derivedFrom":sQuery(id+"F0.wireOp",EDGE,"E25.8.4")}),-1.0]])]});
            var Q63;
            Q63=makeQuery(id+"F0.imprint","IMPRINT",FACE,{"disambiguationData":[TD([[makeQuery(id+"F0.imprint","IMPRINT",EDGE,{"derivedFrom":sQuery(id+"F0.wireOp",EDGE,"E25.9.0")}),-1.0]])]});
            var Q64;
            Q64=makeQuery(id+"F0.imprint","IMPRINT",FACE,{"disambiguationData":[TD([[makeQuery(id+"F0.imprint","IMPRINT",EDGE,{"derivedFrom":sQuery(id+"F0.wireOp",EDGE,"E25.9.4")}),-1.0]])]});
            var Q65;
            Q65=makeQuery(id+"F0.imprint","IMPRINT",FACE,{"disambiguationData":[TD([[makeQuery(id+"F0.imprint","IMPRINT",EDGE,{"derivedFrom":sQuery(id+"F0.wireOp",EDGE,"E25.10.0")}),-1.0]])]});
            var Q66;
            Q66=makeQuery(id+"F0.imprint","IMPRINT",FACE,{"disambiguationData":[TD([[makeQuery(id+"F0.imprint","IMPRINT",EDGE,{"derivedFrom":sQuery(id+"F0.wireOp",EDGE,"E25.10.4")}),-1.0]])]});
            var Q67;
            Q67=makeQuery(id+"F0.imprint","IMPRINT",FACE,{"disambiguationData":[TD([[makeQuery(id+"F0.imprint","IMPRINT",EDGE,{"derivedFrom":sQuery(id+"F0.wireOp",EDGE,"E25.11.0")}),-1.0]])]});
            var Q68;
            Q68=makeQuery(id+"F0.imprint","IMPRINT",FACE,{"disambiguationData":[TD([[makeQuery(id+"F0.imprint","IMPRINT",EDGE,{"derivedFrom":sQuery(id+"F0.wireOp",EDGE,"E25.11.4")}),-1.0]])]});
            var Q69;
            Q69=makeQuery(id+"F0.imprint","IMPRINT",FACE,{"disambiguationData":[TD([[makeQuery(id+"F0.imprint","IMPRINT",EDGE,{"derivedFrom":sQuery(id+"F0.wireOp",EDGE,"E25.12.0")}),-1.0]])]});
            var Q70;
            Q70=makeQuery(id+"F0.imprint","IMPRINT",FACE,{"disambiguationData":[TD([[makeQuery(id+"F0.imprint","IMPRINT",EDGE,{"derivedFrom":sQuery(id+"F0.wireOp",EDGE,"E25.12.4")}),-1.0]])]});
            var Q71;
            Q71=makeQuery(id+"F0.imprint","IMPRINT",FACE,{"disambiguationData":[TD([[makeQuery(id+"F0.imprint","IMPRINT",EDGE,{"derivedFrom":sQuery(id+"F0.wireOp",EDGE,"E25.13.0")}),-1.0]])]});
            var Q72;
            Q72=makeQuery(id+"F0.imprint","IMPRINT",FACE,{"disambiguationData":[TD([[makeQuery(id+"F0.imprint","IMPRINT",EDGE,{"derivedFrom":sQuery(id+"F0.wireOp",EDGE,"E25.13.4")}),-1.0]])]});
            var Q73;
            Q73=makeQuery(id+"F0.imprint","IMPRINT",FACE,{"disambiguationData":[TD([[makeQuery(id+"F0.imprint","IMPRINT",EDGE,{"derivedFrom":sQuery(id+"F0.wireOp",EDGE,"E25.14.0")}),-1.0]])]});
            var Q74;
            Q74=makeQuery(id+"F0.imprint","IMPRINT",FACE,{"disambiguationData":[TD([[makeQuery(id+"F0.imprint","IMPRINT",EDGE,{"derivedFrom":sQuery(id+"F0.wireOp",EDGE,"E25.14.4")}),-1.0]])]});
            var Q75;
            Q75=makeQuery(id+"F0.imprint","IMPRINT",FACE,{"disambiguationData":[TD([[makeQuery(id+"F0.imprint","IMPRINT",EDGE,{"derivedFrom":sQuery(id+"F0.wireOp",EDGE,"E6.bottom")}),1.0]])]});
            extrude(context, id + "F10", {"entities" : qUnion([Q0, Q1, Q2, Q3, Q4, Q5, Q6, Q7, Q8, Q9, Q10, Q11, Q12, Q13, Q14, Q15, Q16, Q17, Q18, Q19, Q20, Q21, Q22, Q23, Q24, Q25, Q26, Q27, Q28, Q29, Q30, Q31, Q32, Q33, Q34, Q35, Q36, Q37, Q38, Q39, Q40, Q41, Q42, Q43, Q44, Q45, Q46, Q47, Q48, Q49, Q50, Q51, Q52, Q53, Q54, Q55, Q56, Q57, Q58, Q59, Q60, Q61, Q62, Q63, Q64, Q65, Q66, Q67, Q68, Q69, Q70, Q71, Q72, Q73, Q74, Q75]), "depth" : 5 * mm});
        }
        {
            var Q0;
            Q0=qCreatedBy(id+"F3.planeOp",FACE);
            var sketch = newSketch(context, id + "F11", { "sketchPlane" : qUnion([Q0])});
            skLineSegment(sketch, "E354", {"start": v(956.83, -275) * mm, "end": v(956.83, -445) * mm});
            skLineSegment(sketch, "E355", {"start": v(956.83, -445) * mm, "end": v(876.93, -445) * mm});
            skLineSegment(sketch, "E356", {"start": v(878.28, -442.12) * mm, "end": v(953.48, -282.12) * mm});
            skPoint(sketch, "E357.visualSharp", {"position": v(956.83, -275) * mm});
            skArc(sketch, "E357.filletArc", {"start": v(953.48, -282.12) * mm, "mid": v(953.18, -277.31) * mm, "end": v(948.96, -275) * mm});
            skLineSegment(sketch, "E358", {"start": v(948.96, -275) * mm, "end": v(956.83, -275) * mm});
            skPoint(sketch, "E359.visualSharp", {"position": v(876.93, -445) * mm});
            skArc(sketch, "E359.filletArc", {"start": v(873.76, -445) * mm, "mid": v(876.44, -444.22) * mm, "end": v(878.28, -442.12) * mm});
            skLineSegment(sketch, "E360", {"start": v(873.76, -445) * mm, "end": v(876.93, -445) * mm});
            skPoint(sketch, "E361", {"position": v(0, 0) * mm});
            skLineSegment(sketch, "E362.bottom", {"start": v(335.4, 217.97) * mm, "end": v(239.74, 320.2) * mm});
            skLineSegment(sketch, "E362.top", {"start": v(437.62, 313.62) * mm, "end": v(434.2, 317.28) * mm});
            skLineSegment(sketch, "E362.left", {"start": v(335.4, 217.97) * mm, "end": v(437.62, 313.62) * mm});
            skLineSegment(sketch, "E362.right", {"start": v(239.74, 320.2) * mm, "end": v(341.96, 415.85) * mm});
            skLineSegment(sketch, "E363", {"start": v(345.38, 412.2) * mm, "end": v(246.8, 319.96) * mm});
            skLineSegment(sketch, "E364", {"start": v(434.2, 317.28) * mm, "end": v(335.63, 225.04) * mm});
            skLineSegment(sketch, "E365", {"start": v(246.8, 319.96) * mm, "end": v(335.63, 225.04) * mm});
            skLineSegment(sketch, "E366.trimOffspring", {"start": v(345.38, 412.2) * mm, "end": v(341.96, 415.85) * mm});
            skPoint(sketch, "E367.orphan", {"position": v(243.16, 316.54) * mm});
            skPoint(sketch, "E368.orphan", {"position": v(331.98, 221.62) * mm});
            skLineSegment(sketch, "E369.1.0", {"start": v(395.41, 60.4) * mm, "end": v(527.97, 105.44) * mm});
            skPoint(sketch, "E369.1.1", {"position": v(351.98, 188.23) * mm});
            skLineSegment(sketch, "E369.1.2", {"start": v(484.54, 233.27) * mm, "end": v(356.72, 189.84) * mm});
            skLineSegment(sketch, "E369.1.3", {"start": v(526.36, 110.18) * mm, "end": v(398.54, 66.75) * mm});
            skLineSegment(sketch, "E369.1.4", {"start": v(350.38, 192.97) * mm, "end": v(482.93, 238) * mm});
            skPoint(sketch, "E369.1.5", {"position": v(393.8, 65.14) * mm});
            skLineSegment(sketch, "E369.1.6", {"start": v(395.41, 60.4) * mm, "end": v(350.38, 192.97) * mm});
            skLineSegment(sketch, "E369.1.7", {"start": v(356.72, 189.84) * mm, "end": v(398.54, 66.75) * mm});
            skLineSegment(sketch, "E369.1.8", {"start": v(527.97, 105.44) * mm, "end": v(526.36, 110.18) * mm});
            skLineSegment(sketch, "E369.1.9", {"start": v(484.54, 233.27) * mm, "end": v(482.93, 238) * mm});
            skLineSegment(sketch, "E369.2.0", {"start": v(385.18, -107.88) * mm, "end": v(524.52, -121.47) * mm});
            skPoint(sketch, "E369.2.1", {"position": v(398.28, 26.48) * mm});
            skLineSegment(sketch, "E369.2.2", {"start": v(537.62, 12.9) * mm, "end": v(403.25, 26) * mm});
            skLineSegment(sketch, "E369.2.3", {"start": v(525, -116.5) * mm, "end": v(390.64, -103.4) * mm});
            skLineSegment(sketch, "E369.2.4", {"start": v(398.76, 31.45) * mm, "end": v(538.1, 17.87) * mm});
            skPoint(sketch, "E369.2.5", {"position": v(385.66, -102.9) * mm});
            skLineSegment(sketch, "E369.2.6", {"start": v(385.18, -107.88) * mm, "end": v(398.76, 31.45) * mm});
            skLineSegment(sketch, "E369.2.7", {"start": v(403.25, 26) * mm, "end": v(390.64, -103.4) * mm});
            skLineSegment(sketch, "E369.2.8", {"start": v(524.52, -121.47) * mm, "end": v(525, -116.5) * mm});
            skLineSegment(sketch, "E369.2.9", {"start": v(537.62, 12.9) * mm, "end": v(538.1, 17.87) * mm});
            skLineSegment(sketch, "E369.3.0", {"start": v(306.5, -257.01) * mm, "end": v(427.87, -326.8) * mm});
            skPoint(sketch, "E369.3.1", {"position": v(373.8, -139.98) * mm});
            skLineSegment(sketch, "E369.3.2", {"start": v(495.17, -209.77) * mm, "end": v(378.14, -142.47) * mm});
            skLineSegment(sketch, "E369.3.3", {"start": v(430.36, -322.47) * mm, "end": v(313.33, -255.17) * mm});
            skLineSegment(sketch, "E369.3.4", {"start": v(376.3, -135.65) * mm, "end": v(497.66, -205.44) * mm});
            skPoint(sketch, "E369.3.5", {"position": v(309, -252.68) * mm});
            skLineSegment(sketch, "E369.3.6", {"start": v(306.5, -257.01) * mm, "end": v(376.3, -135.65) * mm});
            skLineSegment(sketch, "E369.3.7", {"start": v(378.14, -142.47) * mm, "end": v(313.33, -255.17) * mm});
            skLineSegment(sketch, "E369.3.8", {"start": v(427.87, -326.8) * mm, "end": v(430.36, -322.47) * mm});
            skLineSegment(sketch, "E369.3.9", {"start": v(495.17, -209.77) * mm, "end": v(497.66, -205.44) * mm});
            skLineSegment(sketch, "E369.anchor1", {"start": v(0, 0) * mm, "end": v(335.4, 217.97) * mm, "construction": true});
            skLineSegment(sketch, "E369.anchor2", {"start": v(0, 0) * mm, "end": v(306.5, -257.01) * mm, "construction": true});
            skSolve(sketch);
        }
        {
            var Q0;
            {var subQ0=sQuery(id+"F11.wireOp",EDGE,"735cf156-9751-47a4-8615-843c105e4f0b.left");Q0=makeQuery(id+"F11.imprint","IMPRINT",FACE,{"disambiguationData":[TD([[makeQuery(id+"F11.imprint","IMPRINT",EDGE,{"derivedFrom":subQ0}),1.0]])]});}
            var Q1;
            {var subQ0=sQuery(id+"F11.wireOp",EDGE,"735cf156-9751-47a4-8615-843c105e4f0b.right");Q1=makeQuery(id+"F11.imprint","IMPRINT",FACE,{"disambiguationData":[TD([[makeQuery(id+"F11.imprint","IMPRINT",EDGE,{"derivedFrom":subQ0}),-1.0]])]});}
            var Q2;
            {var subQ0=sQuery(id+"F11.wireOp",EDGE,"E362.left");Q2=makeQuery(id+"F11.imprint","IMPRINT",FACE,{"disambiguationData":[TD([[makeQuery(id+"F11.imprint","IMPRINT",EDGE,{"derivedFrom":subQ0}),1.0]])]});}
            var Q3;
            {var subQ0=sQuery(id+"F11.wireOp",EDGE,"E362.right");Q3=makeQuery(id+"F11.imprint","IMPRINT",FACE,{"disambiguationData":[TD([[makeQuery(id+"F11.imprint","IMPRINT",EDGE,{"derivedFrom":subQ0}),-1.0]])]});}
            var Q4;
            {var subQ0=sQuery(id+"F11.wireOp",EDGE,"cc90ada6-a46f-43f3-882d-84b4c27cf417.1.0");Q4=makeQuery(id+"F11.imprint","IMPRINT",FACE,{"disambiguationData":[TD([[makeQuery(id+"F11.imprint","IMPRINT",EDGE,{"derivedFrom":subQ0}),-1.0]])]});}
            var Q5;
            {var subQ0=sQuery(id+"F11.wireOp",EDGE,"cc90ada6-a46f-43f3-882d-84b4c27cf417.1.1");Q5=makeQuery(id+"F11.imprint","IMPRINT",FACE,{"disambiguationData":[TD([[makeQuery(id+"F11.imprint","IMPRINT",EDGE,{"derivedFrom":subQ0}),1.0]])]});}
            var Q6;
            {var subQ0=sQuery(id+"F11.wireOp",EDGE,"cc90ada6-a46f-43f3-882d-84b4c27cf417.2.0");Q6=makeQuery(id+"F11.imprint","IMPRINT",FACE,{"disambiguationData":[TD([[makeQuery(id+"F11.imprint","IMPRINT",EDGE,{"derivedFrom":subQ0}),-1.0]])]});}
            var Q7;
            {var subQ0=sQuery(id+"F11.wireOp",EDGE,"cc90ada6-a46f-43f3-882d-84b4c27cf417.2.1");Q7=makeQuery(id+"F11.imprint","IMPRINT",FACE,{"disambiguationData":[TD([[makeQuery(id+"F11.imprint","IMPRINT",EDGE,{"derivedFrom":subQ0}),1.0]])]});}
            var Q8;
            {var subQ0=sQuery(id+"F11.wireOp",EDGE,"r9zKdHIS-bUvo-AVlk-1P1l-eesWTHnGL4Qp");Q8=makeQuery(id+"F11.imprint","IMPRINT",FACE,{"disambiguationData":[TD([[makeQuery(id+"F11.imprint","IMPRINT",EDGE,{"derivedFrom":subQ0}),1.0]])]});}
            var Q9;
            {var subQ0=sQuery(id+"F11.wireOp",EDGE,"E363");Q9=makeQuery(id+"F11.imprint","IMPRINT",FACE,{"disambiguationData":[TD([[makeQuery(id+"F11.imprint","IMPRINT",EDGE,{"derivedFrom":subQ0}),1.0]])]});}
            var Q10;
            {var subQ0=sQuery(id+"F11.wireOp",EDGE,"cc90ada6-a46f-43f3-882d-84b4c27cf417.1.0");Q10=makeQuery(id+"F11.imprint","IMPRINT",FACE,{"disambiguationData":[TD([[makeQuery(id+"F11.imprint","IMPRINT",EDGE,{"derivedFrom":subQ0}),1.0]])]});}
            var Q11;
            {var subQ0=sQuery(id+"F11.wireOp",EDGE,"cc90ada6-a46f-43f3-882d-84b4c27cf417.2.0");Q11=makeQuery(id+"F11.imprint","IMPRINT",FACE,{"disambiguationData":[TD([[makeQuery(id+"F11.imprint","IMPRINT",EDGE,{"derivedFrom":subQ0}),1.0]])]});}
            var Q12;
            {var subQ0=sQuery(id+"F11.wireOp",EDGE,"29c5f27d-3468-4435-8365-3346e811c2e8.3.3.0");Q12=makeQuery(id+"F11.imprint","IMPRINT",FACE,{"disambiguationData":[TD([[makeQuery(id+"F11.imprint","IMPRINT",EDGE,{"derivedFrom":subQ0}),1.0]])]});}
            var Q13;
            {var subQ0=sQuery(id+"F11.wireOp",EDGE,"29c5f27d-3468-4435-8365-3346e811c2e8.3.3.0");Q13=makeQuery(id+"F11.imprint","IMPRINT",FACE,{"disambiguationData":[TD([[makeQuery(id+"F11.imprint","IMPRINT",EDGE,{"derivedFrom":subQ0}),-1.0]])]});}
            var Q14;
            {var subQ2=sQuery(id+"F11.wireOp",EDGE,"29c5f27d-3468-4435-8365-3346e811c2e8.7.3.0");Q14=makeQuery(id+"F11.imprint","IMPRINT",FACE,{"disambiguationData":[TD([[makeQuery(id+"F11.imprint","IMPRINT",EDGE,{"derivedFrom":subQ2}),-1.0]])]});}
            extrude(context, id + "F12", {"entities" : qUnion([Q0, Q1, Q2, Q3, Q4, Q5, Q6, Q7, Q8, Q9, Q10, Q11, Q12, Q13, Q14]), "operationType" : NewBodyOperationType.ADD, "oppositeDirection" : true, "depth" : 5 * mm});
        }
        {
            var Q0;
            Q0=makeQuery(id+"F11.imprint","IMPRINT",FACE,{"disambiguationData":[TD([[makeQuery(id+"F11.imprint","IMPRINT",EDGE,{"derivedFrom":sQuery(id+"F11.wireOp",EDGE,"E362.bottom")}),-1.0]])]});
            var Q1;
            Q1=makeQuery(id+"F11.imprint","IMPRINT",FACE,{"disambiguationData":[TD([[makeQuery(id+"F11.imprint","IMPRINT",EDGE,{"derivedFrom":sQuery(id+"F11.wireOp",EDGE,"E369.1.0")}),1.0]])]});
            var Q2;
            Q2=makeQuery(id+"F11.imprint","IMPRINT",FACE,{"disambiguationData":[TD([[makeQuery(id+"F11.imprint","IMPRINT",EDGE,{"derivedFrom":sQuery(id+"F11.wireOp",EDGE,"E369.2.0")}),1.0]])]});
            var Q3;
            Q3=makeQuery(id+"F11.imprint","IMPRINT",FACE,{"disambiguationData":[TD([[makeQuery(id+"F11.imprint","IMPRINT",EDGE,{"derivedFrom":sQuery(id+"F11.wireOp",EDGE,"E369.3.0")}),1.0]])]});
            extrude(context, id + "F13", {"entities" : qUnion([Q0, Q1, Q2, Q3]), "operationType" : NewBodyOperationType.ADD, "oppositeDirection" : true, "depth" : 170 * mm});
        }
        {
            var Q0;
            Q0=makeQuery(id+"F13.opExtrude","SWEPT_FACE",FACE,{"disambiguationData":[OSD([sQuery(id+"F11.wireOp",EDGE,"E369.3.0")])]});
            var sketch = newSketch(context, id + "F14", { "sketchPlane" : qUnion([Q0])});
            skLineSegment(sketch, "E370", {"start": v(533.83, -160) * mm, "end": v(533.83, -330) * mm});
            skLineSegment(sketch, "E371", {"start": v(533.83, -330) * mm, "end": v(453.93, -330) * mm});
            skLineSegment(sketch, "E372", {"start": v(455.28, -327.13) * mm, "end": v(530.48, -167.13) * mm});
            skPoint(sketch, "E373.visualSharp", {"position": v(533.83, -160) * mm});
            skArc(sketch, "E373.filletArc", {"start": v(530.48, -167.13) * mm, "mid": v(530.17, -162.32) * mm, "end": v(525.95, -160) * mm});
            skLineSegment(sketch, "E374", {"start": v(525.95, -160) * mm, "end": v(533.83, -160) * mm});
            skPoint(sketch, "E375.visualSharp", {"position": v(453.93, -330) * mm});
            skArc(sketch, "E375.filletArc", {"start": v(450.75, -330) * mm, "mid": v(453.43, -329.22) * mm, "end": v(455.28, -327.13) * mm});
            skLineSegment(sketch, "E376", {"start": v(450.75, -330) * mm, "end": v(453.93, -330) * mm});
            skSolve(sketch);
        }
        {
            var Q0;
            Q0=qCreatedBy(makeId("Front.planeOp"),FACE);
            var sketch = newSketch(context, id + "F15", { "sketchPlane" : qUnion([Q0])});
            skLineSegment(sketch, "E377", {"start": v(0, 0) * mm, "end": v(0, 50.55) * mm});
            skSolve(sketch);
        }
        {
            var Q0;
            Q0=makeQuery(id+"F14.imprint","IMPRINT",FACE,{"disambiguationData":[TD([[makeQuery(id+"F14.imprint","IMPRINT",EDGE,{"derivedFrom":sQuery(id+"F14.wireOp",EDGE,"E370")}),1.0]])]});
            var Q1;
            Q1=sQuery(id+"F15.wireOp",EDGE,"E377");
            revolve(context, id + "F16", {"operationType" : NewBodyOperationType.REMOVE, "entities" : qUnion([Q0]), "axis" : qUnion([Q1]), "revolveType" : RevolveType.FULL, "oppositeDirection" : true});
        }
    });
